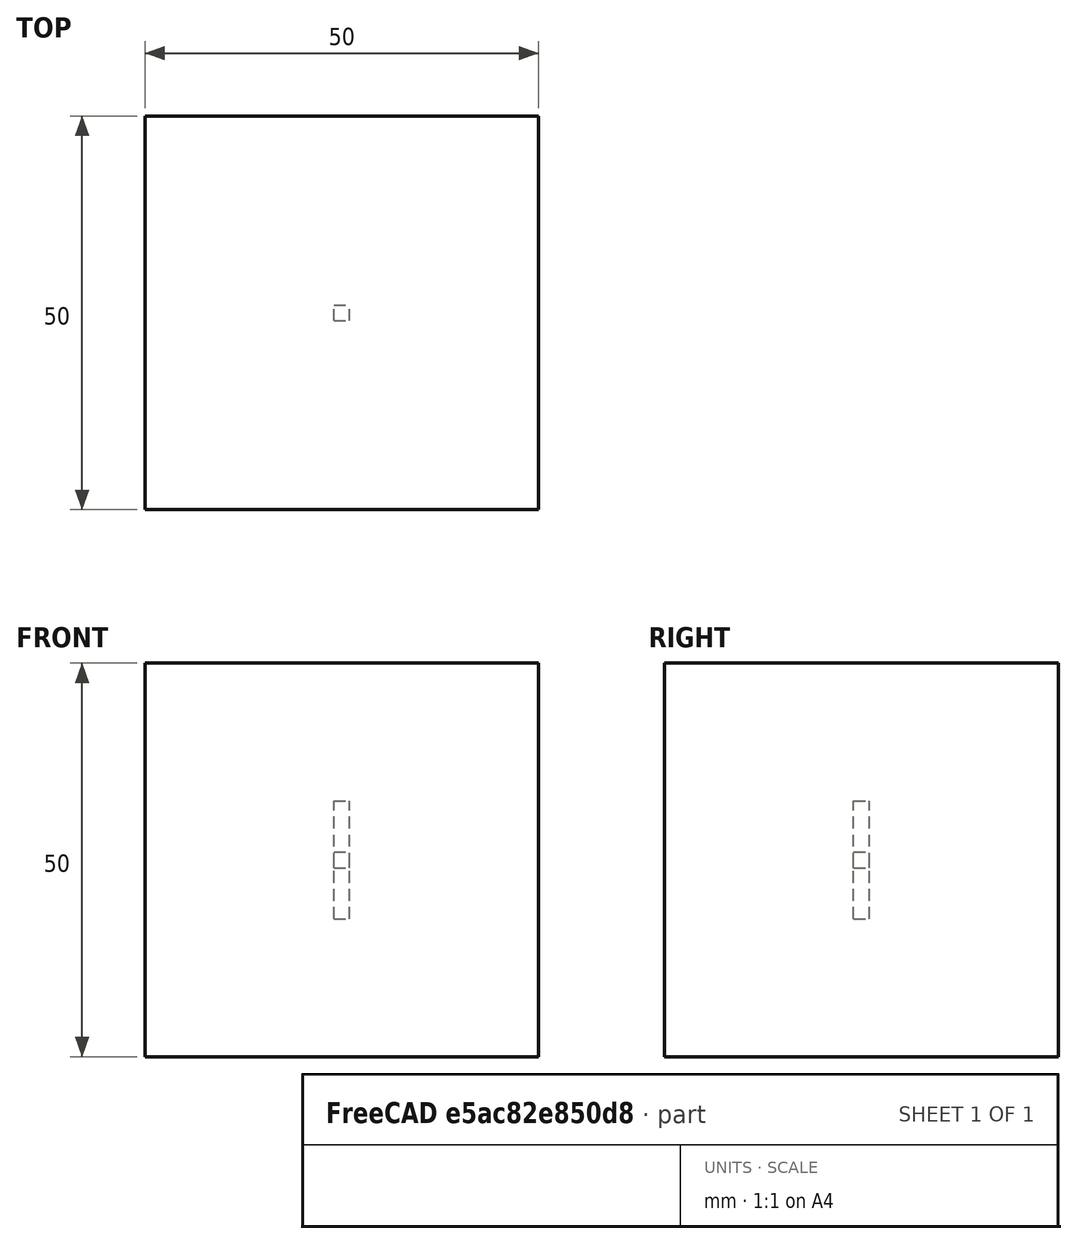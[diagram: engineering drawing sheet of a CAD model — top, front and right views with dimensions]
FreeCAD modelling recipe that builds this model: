
FCSTD DOCUMENT  (FreeCAD 1.0R39109 (Git))
Label: COG_Expanded_simple_array
License: All rights reserved
LicenseURL: http://en.wikipedia.org/wiki/All_rights_reserved
objects: App::DocumentObjectGroupPython×1269, App::Part×7, Part::FeaturePython×6, App::Link×4, App::FeaturePython×2
note: 5 computed .brp shape members not serialized (recipe doc carries the construction recipe); baked Part::Feature solids carry a one-line shape summary decoded from their .brp

FEATURE [App::DocumentObjectGroupPython] Constants  # scripted group (container) (typed FeaturePython)
FEATURE [App::DocumentObjectGroupPython] Variables  # scripted group (container) (typed FeaturePython)
FEATURE [App::DocumentObjectGroupPython] Quantities  # scripted group (container) (typed FeaturePython)
FEATURE [App::DocumentObjectGroupPython] Isotopes  # scripted group (container) (typed FeaturePython)
FEATURE [App::DocumentObjectGroupPython] Elements  # scripted group (container) (typed FeaturePython)
FEATURE [App::DocumentObjectGroupPython] G4_CESIUM_IODIDE  label="G4_CESIUM_IODIDE : 1.000"  # scripted group (container) (typed FeaturePython)
  n = 1
FEATURE [App::DocumentObjectGroupPython] LYSO  # scripted group (container) (typed FeaturePython)
  ABSLENGTH = ABSLENGTHLAR
  Dunit = g/cm3
  Dvalue = 7.1
  FASTCOMPONENT = SCINTLAR
  Group = -> [G4_CESIUM_IODIDE]
  RAYLEIGH = RAYLEIGHLAR
  REEMISSIONPROB = SCINTLAR
  RESOLUTIONSCALE = RS
  RINDEX = RINDEXLAR
  SCINTILLATIONCOMPONENT1 = SCINTLAR
  SCINTILLATIONCOMPONENT2 = SCINTLAR
  SCINTILLATIONTIMECONSTANT1 = FTC
  SCINTILLATIONTIMECONSTANT2 = STC
  SCINTILLATIONYIELD = SY
  SCINTILLATIONYIELD1 = RY1
  SCINTILLATIONYIELD2 = RY2
  SLOWCOMPONENT = SCINTLAR
  YIELDRATIO = YR
  conduct = 2
  density = 1
  expand = 3
  name = LYSO
  specific = 4
FEATURE [App::DocumentObjectGroupPython] G4_AIR  label="G4_AIR : 1.000"  # scripted group (container) (typed FeaturePython)
  n = 1
FEATURE [App::DocumentObjectGroupPython] Air  # scripted group (container) (typed FeaturePython)
  Dunit = mg/cm3
  Dvalue = 1.29
  Group = -> [G4_AIR]
  RINDEX = AirRINDEX
  conduct = 2
  density = 1
  expand = 3
  name = Air
  specific = 4
FEATURE [App::DocumentObjectGroupPython] G4_SILICON_DIOXIDE  label="G4_SILICON_DIOXIDE : 1.000"  # scripted group (container) (typed FeaturePython)
  n = 1
FEATURE [App::DocumentObjectGroupPython] Glass  # scripted group (container) (typed FeaturePython)
  Dunit = g/cm3
  Dvalue = 2.32
  Group = -> [G4_SILICON_DIOXIDE]
  RINDEX = RINDEXLAR
  conduct = 2
  density = 1
  expand = 3
  name = Glass
  specific = 4
FEATURE [App::DocumentObjectGroupPython] SY  # scripted group (container) (typed FeaturePython)
  coldim = 1
  values = 100000
FEATURE [App::DocumentObjectGroupPython] RS  # scripted group (container) (typed FeaturePython)
  coldim = 1
  values = 1
FEATURE [App::DocumentObjectGroupPython] FTC  # scripted group (container) (typed FeaturePython)
  coldim = 1
  values = 21.5*ns
FEATURE [App::DocumentObjectGroupPython] STC  # scripted group (container) (typed FeaturePython)
  coldim = 1
  values = 43.8*ns
FEATURE [App::DocumentObjectGroupPython] RY1  # scripted group (container) (typed FeaturePython)
  coldim = 1
  values = 95
FEATURE [App::DocumentObjectGroupPython] RY2  # scripted group (container) (typed FeaturePython)
  coldim = 1
  values = 5
FEATURE [App::DocumentObjectGroupPython] YR  # scripted group (container) (typed FeaturePython)
  coldim = 1
  values = 0.8
FEATURE [App::DocumentObjectGroupPython] SCINTLAR  # scripted group (container) (typed FeaturePython)
  coldim = 2
  values = <blob: 2358 chars omitted>
FEATURE [App::DocumentObjectGroupPython] RINDEXLAR  # scripted group (container) (typed FeaturePython)
  coldim = 2
  values = <blob: 9384 chars omitted>
FEATURE [App::DocumentObjectGroupPython] ABSLENGTHLAR  # scripted group (container) (typed FeaturePython)
  coldim = 2
  values = 7.74901*eV 10.0*m 7.77525*eV 10.0*m 7.80167*eV 10.0*m 7.82827*eV 10.0*m 7.85506*eV 10.0*m 7.88202*eV 10.0*m 7.90917*eV 10.0*m 7.93651*eV 10.0*m 7.96404*eV 10.0*m 7.99176*eV 10.0*m 8.01968*eV 10.0*m 8.04779*eV 10.0*m 8.07609*eV 10.0*m 8.1046*eV 10.0*m 8.13331*eV 10.0*m 8.16222*eV 10.0*m 8.19134*eV 10.0*m 8.22067*eV 10.0*m 8.25021*eV 10.0*m 8.27996*eV 10.0*m 8.30993*eV 10.0*m 8.34012*eV 10.0*m 8.37052*eV 10.0*m 8.40115*eV 10.0*m 8.432*eV 10.0*m 8.46308*eV 10.0*m 8.4944*eV 10.0*m 8.52594*eV 10.0*m 8.55772*eV 10.0*m 8.58973*eV 10.0*m 8.62199*eV 10.0*m 8.65449*eV 10.0*m 8.68723*eV 10.0*m 8.72023*eV 10.0*m 8.75347*eV 10.0*m 8.78697*eV 10.0*m 8.82073*eV 10.0*m 8.85475*eV 10.0*m 8.88903*eV 10.0*m 8.92358*eV 10.0*m 8.9584*eV 10.0*m 8.99349*eV 10.0*m 9.02885*eV 10.0*m 9.0645*eV 10.0*m 9.10043*eV 10.0*m 9.13664*eV 10.0*m 9.17314*eV 10.0*m 9.20994*eV 10.0*m 9.24703*eV 10.0*m 9.28442*eV 10.0*m 9.32212*eV 10.0*m 9.36012*eV 10.0*m 9.39844*eV 10.0*m 9.43707*eV 10.0*m 9.47602*eV 10.0*m 9.51529*eV 10.0*m 9.55489*eV 10.0*m 9.59481*eV 10.0*m 9.63508*eV 10.0*m 9.67568*eV 10.0*m 9.71663*eV 10.0*m 9.75792*eV 10.0*m 9.79957*eV 10.0*m 9.84158*eV 10.0*m 9.88394*eV 10.0*m 9.92668*eV 10.0*m 9.96978*eV 10.0*m 10.0133*eV 10.0*m 10.0571*eV 10.0*m 10.1014*eV 10.0*m 10.146*eV 10.0*m 10.191*eV 10.0*m 10.2365*eV 10.0*m 10.2823*eV 10.0*m 10.3286*eV 10.0*m 10.3752*eV 10.0*m 10.4223*eV 10.0*m 10.4699*eV 10.0*m 10.5178*eV 10.0*m 10.5662*eV 10.0*m 10.6151*eV 10.0*m 10.6644*eV 10.0*m 10.7142*eV 10.0*m 10.7644*eV 10.0*m 10.8151*eV 10.0*m 10.8663*eV 10.0*m 10.9179*eV 10.0*m 10.9701*eV 10.0*m 11.0228*eV 10.0*m 11.076*eV 10.0*m 11.1296*eV 10.0*m 11.1839*eV 10.0*m 11.2386*eV 10.0*m 11.2939*eV 10.0*m 11.3497*eV 10.0*m 11.4061*eV 10.0*m 11.463*eV 10.0*m 11.5206*eV 10.0*m 11.5787*eV 10.0*m 11.6373*eV 10.0*m
FEATURE [App::DocumentObjectGroupPython] RAYLEIGHLAR  # scripted group (container) (typed FeaturePython)
  coldim = 2
  values = 7.74901*eV 90.0*cm 7.77525*eV 90.0*cm 7.80167*eV 90.0*cm 7.82827*eV 90.0*cm 7.85506*eV 90.0*cm 7.88202*eV 90.0*cm 7.90917*eV 90.0*cm 7.93651*eV 90.0*cm 7.96404*eV 90.0*cm 7.99176*eV 90.0*cm 8.01968*eV 90.0*cm 8.04779*eV 90.0*cm 8.07609*eV 90.0*cm 8.1046*eV 90.0*cm 8.13331*eV 90.0*cm 8.16222*eV 90.0*cm 8.19134*eV 90.0*cm 8.22067*eV 90.0*cm 8.25021*eV 90.0*cm 8.27996*eV 90.0*cm 8.30993*eV 90.0*cm 8.34012*eV 90.0*cm 8.37052*eV 90.0*cm 8.40115*eV 90.0*cm 8.432*eV 90.0*cm 8.46308*eV 90.0*cm 8.4944*eV 90.0*cm 8.52594*eV 90.0*cm 8.55772*eV 90.0*cm 8.58973*eV 90.0*cm 8.62199*eV 90.0*cm 8.65449*eV 90.0*cm 8.68723*eV 90.0*cm 8.72023*eV 90.0*cm 8.75347*eV 90.0*cm 8.78697*eV 90.0*cm 8.82073*eV 90.0*cm 8.85475*eV 90.0*cm 8.88903*eV 90.0*cm 8.92358*eV 90.0*cm 8.9584*eV 90.0*cm 8.99349*eV 90.0*cm 9.02885*eV 90.0*cm 9.0645*eV 90.0*cm 9.10043*eV 90.0*cm 9.13664*eV 90.0*cm 9.17314*eV 90.0*cm 9.20994*eV 90.0*cm 9.24703*eV 90.0*cm 9.28442*eV 90.0*cm 9.32212*eV 90.0*cm 9.36012*eV 90.0*cm 9.39844*eV 90.0*cm 9.43707*eV 90.0*cm 9.47602*eV 90.0*cm 9.51529*eV 90.0*cm 9.55489*eV 90.0*cm 9.59481*eV 90.0*cm 9.63508*eV 90.0*cm 9.67568*eV 90.0*cm 9.71663*eV 90.0*cm 9.75792*eV 90.0*cm 9.79957*eV 90.0*cm 9.84158*eV 90.0*cm 9.88394*eV 90.0*cm 9.92668*eV 90.0*cm 9.96978*eV 90.0*cm 10.0133*eV 90.0*cm 10.0571*eV 90.0*cm 10.1014*eV 90.0*cm 10.146*eV 90.0*cm 10.191*eV 90.0*cm 10.2365*eV 90.0*cm 10.2823*eV 90.0*cm 10.3286*eV 90.0*cm 10.3752*eV 90.0*cm 10.4223*eV 90.0*cm 10.4699*eV 90.0*cm 10.5178*eV 90.0*cm 10.5662*eV 90.0*cm 10.6151*eV 90.0*cm 10.6644*eV 90.0*cm 10.7142*eV 90.0*cm 10.7644*eV 90.0*cm 10.8151*eV 90.0*cm 10.8663*eV 90.0*cm 10.9179*eV 90.0*cm 10.9701*eV 90.0*cm 11.0228*eV 90.0*cm 11.076*eV 90.0*cm 11.1296*eV 90.0*cm 11.1839*eV 90.0*cm 11.2386*eV 90.0*cm 11.2939*eV 90.0*cm 11.3497*eV 90.0*cm 11.4061*eV 90.0*cm 11.463*eV 90.0*cm 11.5206*eV 90.0*cm 11.5787*eV 90.0*cm 11.6373*eV 90.0*cm
FEATURE [App::DocumentObjectGroupPython] REFLECTIVITY  # scripted group (container) (typed FeaturePython)
  coldim = 2
  values = 2.034*eV 0.98 2.068*eV 0.98 2.103*eV 0.98 2.139*eV 0.98 2.177*eV 0.98 2.216*eV 0.98 2.256*eV 0.98 2.298*eV 0.98 2.341*eV 0.98 2.386*eV 0.98 2.433*eV 0.98 2.481*eV 0.98 2.532*eV 0.98 2.585*eV 0.98 2.64*eV 0.98 2.697*eV 0.98 2.757*eV 0.98 2.82*eV 0.98 2.885*eV 0.98 2.954*eV 0.98 3.026*eV 0.98 3.102*eV 0.98 3.181*eV 0.98 3.265*eV 0.98 3.353*eV 0.98 3.446*eV 0.98 3.545*eV 0.98 3.649*eV 0.98 3.76*eV 0.98 3.877*eV 0.98 4.002*eV 0.98 4.136*eV 0.98 5.0*eV 0.98 6.0*eV 0.98 7.0*eV 0.98 8.0*eV 0.98 9.0*eV 0.98 9.0*eV 0.98 10.0*eV 0.98 11.0*eV 0.98 11.6*eV 0.98
FEATURE [App::DocumentObjectGroupPython] EFFICIENCY  # scripted group (container) (typed FeaturePython)
  coldim = 2
  values = 2.034*eV 1 2.068*eV 1 2.103*eV 1 2.139*eV 1 2.177*eV 1 2.216*eV 1 2.256*eV 1 2.298*eV 1 2.341*eV 1 2.386*eV 1 2.433*eV 1 2.481*eV 1 2.532*eV 1 2.585*eV 1 2.64*eV 1 2.697*eV 1 2.757*eV 1 2.82*eV 1 2.885*eV 1 2.954*eV 1 3.026*eV 1 3.102*eV 1 3.181*eV  1 3.265*eV 1 3.353*eV 1 3.446*eV 1 3.545*eV 1 3.649*eV 1 3.76*eV 1 3.877*eV 1 4.002*eV 1 4.136*eV 1 5.0*eV 1 6.0*eV 1 7.0*eV 1 8.0*eV 1 9.0*eV 1 9.0*eV 1 10.0*eV 1 11.0*eV 1 11.6*eV 1
FEATURE [App::DocumentObjectGroupPython] AirRINDEX  # scripted group (container) (typed FeaturePython)
  coldim = 2
  values = 2.034*eV 1 2.068*eV 1 2.103*eV 1 2.139*eV 1 2.177*eV 1 2.216*eV 1 2.256*eV 1 2.298*eV 1 2.341*eV 1 2.386*eV 1 2.433*eV 1 2.481*eV 1 2.532*eV 1 2.585*eV 1 2.64*eV 1 2.697*eV 1 2.757*eV 1 2.82*eV 1 2.885*eV 1 2.954*eV 1 3.026*eV 1 3.102*eV 1 3.181*eV 1 3.265*eV 1 3.353*eV 1 3.446*eV 1 3.545*eV 1 3.649*eV 1 3.76*eV 1 3.877*eV 1 4.002*eV 1 4.136*eV 1 5.0*eV 1 6.0*eV 1 7.0*eV 1 8.0*eV 1 9.0*eV 1 10.0*eV 1 11.0*eV 1 11.6*eV 1
FEATURE [App::DocumentObjectGroupPython] Matrix  # scripted group (container) (typed FeaturePython)
  Group = -> [SY,RS,FTC,STC,RY1,RY2,YR,SCINTLAR,RINDEXLAR,ABSLENGTHLAR,RAYLEIGHLAR,REFLECTIVITY,EFFICIENCY,AirRINDEX]
FEATURE [App::DocumentObjectGroupPython] ScintWrap  # scripted group (container) (typed FeaturePython)
  EFFICIENCY = EFFICIENCY
  REFLECTIVITY = REFLECTIVITY
  finish = 39
  model = 0
  type = 2
  value = 1
FEATURE [App::DocumentObjectGroupPython] Surfaces  # scripted group (container) (typed FeaturePython)
  Group = -> [ScintWrap]
FEATURE [App::DocumentObjectGroupPython] Opticals  # scripted group (container) (typed FeaturePython)
  Group = -> [Matrix,Surfaces]
FEATURE [App::DocumentObjectGroupPython] G4Isotopes  # scripted group (container) (typed FeaturePython)
FEATURE [App::DocumentObjectGroupPython] H_element  # scripted group (container) (typed FeaturePython)
  Z = 1
  atom_value = 1.008
  formula = H
  name = H_element
FEATURE [App::DocumentObjectGroupPython] He_element  # scripted group (container) (typed FeaturePython)
  Z = 2
  atom_value = 4.0026
  formula = He
  name = He_element
FEATURE [App::DocumentObjectGroupPython] Li_element  # scripted group (container) (typed FeaturePython)
  Z = 3
  atom_value = 6.94
  formula = Li
  name = Li_element
FEATURE [App::DocumentObjectGroupPython] Be_element  # scripted group (container) (typed FeaturePython)
  Z = 4
  atom_value = 9.01218
  formula = Be
  name = Be_element
FEATURE [App::DocumentObjectGroupPython] B_element  # scripted group (container) (typed FeaturePython)
  Z = 5
  atom_value = 10.81
  formula = B
  name = B_element
FEATURE [App::DocumentObjectGroupPython] C_element  # scripted group (container) (typed FeaturePython)
  Z = 6
  atom_value = 12.011
  formula = C
  name = C_element
FEATURE [App::DocumentObjectGroupPython] N_element  # scripted group (container) (typed FeaturePython)
  Z = 7
  atom_value = 14.007
  formula = N
  name = N_element
FEATURE [App::DocumentObjectGroupPython] O_element  # scripted group (container) (typed FeaturePython)
  Z = 8
  atom_value = 15.999
  formula = O
  name = O_element
FEATURE [App::DocumentObjectGroupPython] F_element  # scripted group (container) (typed FeaturePython)
  Z = 9
  atom_value = 18.9984
  formula = F
  name = F_element
FEATURE [App::DocumentObjectGroupPython] Ne_element  # scripted group (container) (typed FeaturePython)
  Z = 10
  atom_value = 20.1797
  formula = Ne
  name = Ne_element
FEATURE [App::DocumentObjectGroupPython] Na_element  # scripted group (container) (typed FeaturePython)
  Z = 11
  atom_value = 22.9898
  formula = Na
  name = Na_element
FEATURE [App::DocumentObjectGroupPython] Mg_element  # scripted group (container) (typed FeaturePython)
  Z = 12
  atom_value = 24.305
  formula = Mg
  name = Mg_element
FEATURE [App::DocumentObjectGroupPython] Al_element  # scripted group (container) (typed FeaturePython)
  Z = 13
  atom_value = 26.9815
  formula = Al
  name = Al_element
FEATURE [App::DocumentObjectGroupPython] Si_element  # scripted group (container) (typed FeaturePython)
  Z = 14
  atom_value = 28.085
  formula = Si
  name = Si_element
FEATURE [App::DocumentObjectGroupPython] P_element  # scripted group (container) (typed FeaturePython)
  Z = 15
  atom_value = 30.9738
  formula = P
  name = P_element
FEATURE [App::DocumentObjectGroupPython] S_element  # scripted group (container) (typed FeaturePython)
  Z = 16
  atom_value = 32.06
  formula = S
  name = S_element
FEATURE [App::DocumentObjectGroupPython] Cl_element  # scripted group (container) (typed FeaturePython)
  Z = 17
  atom_value = 35.45
  formula = Cl
  name = Cl_element
FEATURE [App::DocumentObjectGroupPython] Ar_element  # scripted group (container) (typed FeaturePython)
  Z = 18
  atom_value = 39.95
  formula = Ar
  name = Ar_element
FEATURE [App::DocumentObjectGroupPython] K_element  # scripted group (container) (typed FeaturePython)
  Z = 19
  atom_value = 39.0983
  formula = K
  name = K_element
FEATURE [App::DocumentObjectGroupPython] Ca_element  # scripted group (container) (typed FeaturePython)
  Z = 20
  atom_value = 40.078
  formula = Ca
  name = Ca_element
FEATURE [App::DocumentObjectGroupPython] Sc_element  # scripted group (container) (typed FeaturePython)
  Z = 21
  atom_value = 44.9559
  formula = Sc
  name = Sc_element
FEATURE [App::DocumentObjectGroupPython] Ti_element  # scripted group (container) (typed FeaturePython)
  Z = 22
  atom_value = 47.867
  formula = Ti
  name = Ti_element
FEATURE [App::DocumentObjectGroupPython] V_element  # scripted group (container) (typed FeaturePython)
  Z = 23
  atom_value = 50.9415
  formula = V
  name = V_element
FEATURE [App::DocumentObjectGroupPython] Cr_element  # scripted group (container) (typed FeaturePython)
  Z = 24
  atom_value = 51.9961
  formula = Cr
  name = Cr_element
FEATURE [App::DocumentObjectGroupPython] Mn_element  # scripted group (container) (typed FeaturePython)
  Z = 25
  atom_value = 54.938
  formula = Mn
  name = Mn_element
FEATURE [App::DocumentObjectGroupPython] Fe_element  # scripted group (container) (typed FeaturePython)
  Z = 26
  atom_value = 55.845
  formula = Fe
  name = Fe_element
FEATURE [App::DocumentObjectGroupPython] Co_element  # scripted group (container) (typed FeaturePython)
  Z = 27
  atom_value = 58.9332
  formula = Co
  name = Co_element
FEATURE [App::DocumentObjectGroupPython] Ni_element  # scripted group (container) (typed FeaturePython)
  Z = 28
  atom_value = 58.6934
  formula = Ni
  name = Ni_element
FEATURE [App::DocumentObjectGroupPython] Cu_element  # scripted group (container) (typed FeaturePython)
  Z = 29
  atom_value = 63.546
  formula = Cu
  name = Cu_element
FEATURE [App::DocumentObjectGroupPython] Zn_element  # scripted group (container) (typed FeaturePython)
  Z = 30
  atom_value = 65.38
  formula = Zn
  name = Zn_element
FEATURE [App::DocumentObjectGroupPython] Ga_element  # scripted group (container) (typed FeaturePython)
  Z = 31
  atom_value = 69.723
  formula = Ga
  name = Ga_element
FEATURE [App::DocumentObjectGroupPython] Ge_element  # scripted group (container) (typed FeaturePython)
  Z = 32
  atom_value = 72.63
  formula = Ge
  name = Ge_element
FEATURE [App::DocumentObjectGroupPython] As_element  # scripted group (container) (typed FeaturePython)
  Z = 33
  atom_value = 74.9216
  formula = As
  name = As_element
FEATURE [App::DocumentObjectGroupPython] Se_element  # scripted group (container) (typed FeaturePython)
  Z = 34
  atom_value = 78.971
  formula = Se
  name = Se_element
FEATURE [App::DocumentObjectGroupPython] Br_element  # scripted group (container) (typed FeaturePython)
  Z = 35
  atom_value = 79.904
  formula = Br
  name = Br_element
FEATURE [App::DocumentObjectGroupPython] Kr_element  # scripted group (container) (typed FeaturePython)
  Z = 36
  atom_value = 83.798
  formula = Kr
  name = Kr_element
FEATURE [App::DocumentObjectGroupPython] Rb_element  # scripted group (container) (typed FeaturePython)
  Z = 37
  atom_value = 85.4678
  formula = Rb
  name = Rb_element
FEATURE [App::DocumentObjectGroupPython] Sr_element  # scripted group (container) (typed FeaturePython)
  Z = 38
  atom_value = 87.62
  formula = Sr
  name = Sr_element
FEATURE [App::DocumentObjectGroupPython] Y_element  # scripted group (container) (typed FeaturePython)
  Z = 39
  atom_value = 88.9058
  formula = Y
  name = Y_element
FEATURE [App::DocumentObjectGroupPython] Zr_element  # scripted group (container) (typed FeaturePython)
  Z = 40
  atom_value = 91.224
  formula = Zr
  name = Zr_element
FEATURE [App::DocumentObjectGroupPython] Nb_element  # scripted group (container) (typed FeaturePython)
  Z = 41
  atom_value = 92.9064
  formula = Nb
  name = Nb_element
FEATURE [App::DocumentObjectGroupPython] Mo_element  # scripted group (container) (typed FeaturePython)
  Z = 42
  atom_value = 95.95
  formula = Mo
  name = Mo_element
FEATURE [App::DocumentObjectGroupPython] Tc_element  # scripted group (container) (typed FeaturePython)
  Z = 43
  atom_value = 97
  formula = Tc
  name = Tc_element
FEATURE [App::DocumentObjectGroupPython] Ru_element  # scripted group (container) (typed FeaturePython)
  Z = 44
  atom_value = 101.07
  formula = Ru
  name = Ru_element
FEATURE [App::DocumentObjectGroupPython] Rh_element  # scripted group (container) (typed FeaturePython)
  Z = 45
  atom_value = 102.905
  formula = Rh
  name = Rh_element
FEATURE [App::DocumentObjectGroupPython] Pd_element  # scripted group (container) (typed FeaturePython)
  Z = 46
  atom_value = 106.42
  formula = Pd
  name = Pd_element
FEATURE [App::DocumentObjectGroupPython] Ag_element  # scripted group (container) (typed FeaturePython)
  Z = 47
  atom_value = 107.868
  formula = Ag
  name = Ag_element
FEATURE [App::DocumentObjectGroupPython] Cd_element  # scripted group (container) (typed FeaturePython)
  Z = 48
  atom_value = 112.414
  formula = Cd
  name = Cd_element
FEATURE [App::DocumentObjectGroupPython] In_element  # scripted group (container) (typed FeaturePython)
  Z = 49
  atom_value = 114.818
  formula = In
  name = In_element
FEATURE [App::DocumentObjectGroupPython] Sn_element  # scripted group (container) (typed FeaturePython)
  Z = 50
  atom_value = 118.71
  formula = Sn
  name = Sn_element
FEATURE [App::DocumentObjectGroupPython] Sb_element  # scripted group (container) (typed FeaturePython)
  Z = 51
  atom_value = 121.76
  formula = Sb
  name = Sb_element
FEATURE [App::DocumentObjectGroupPython] Te_element  # scripted group (container) (typed FeaturePython)
  Z = 52
  atom_value = 127.6
  formula = Te
  name = Te_element
FEATURE [App::DocumentObjectGroupPython] I_element  # scripted group (container) (typed FeaturePython)
  Z = 53
  atom_value = 126.904
  formula = I
  name = I_element
FEATURE [App::DocumentObjectGroupPython] Xe_element  # scripted group (container) (typed FeaturePython)
  Z = 54
  atom_value = 131.293
  formula = Xe
  name = Xe_element
FEATURE [App::DocumentObjectGroupPython] Cs_element  # scripted group (container) (typed FeaturePython)
  Z = 55
  atom_value = 132.905
  formula = Cs
  name = Cs_element
FEATURE [App::DocumentObjectGroupPython] Ba_element  # scripted group (container) (typed FeaturePython)
  Z = 56
  atom_value = 137.327
  formula = Ba
  name = Ba_element
FEATURE [App::DocumentObjectGroupPython] La_element  # scripted group (container) (typed FeaturePython)
  Z = 57
  atom_value = 138.905
  formula = La
  name = La_element
FEATURE [App::DocumentObjectGroupPython] Ce_element  # scripted group (container) (typed FeaturePython)
  Z = 58
  atom_value = 140.116
  formula = Ce
  name = Ce_element
FEATURE [App::DocumentObjectGroupPython] Pr_element  # scripted group (container) (typed FeaturePython)
  Z = 59
  atom_value = 140.908
  formula = Pr
  name = Pr_element
FEATURE [App::DocumentObjectGroupPython] Nd_element  # scripted group (container) (typed FeaturePython)
  Z = 60
  atom_value = 144.242
  formula = Nd
  name = Nd_element
FEATURE [App::DocumentObjectGroupPython] Pm_element  # scripted group (container) (typed FeaturePython)
  Z = 61
  atom_value = 145
  formula = Pm
  name = Pm_element
FEATURE [App::DocumentObjectGroupPython] Sm_element  # scripted group (container) (typed FeaturePython)
  Z = 62
  atom_value = 150.36
  formula = Sm
  name = Sm_element
FEATURE [App::DocumentObjectGroupPython] Eu_element  # scripted group (container) (typed FeaturePython)
  Z = 63
  atom_value = 151.964
  formula = Eu
  name = Eu_element
FEATURE [App::DocumentObjectGroupPython] Gd_element  # scripted group (container) (typed FeaturePython)
  Z = 64
  atom_value = 157.25
  formula = Gd
  name = Gd_element
FEATURE [App::DocumentObjectGroupPython] Tb_element  # scripted group (container) (typed FeaturePython)
  Z = 65
  atom_value = 158.925
  formula = Tb
  name = Tb_element
FEATURE [App::DocumentObjectGroupPython] Dy_element  # scripted group (container) (typed FeaturePython)
  Z = 66
  atom_value = 162.5
  formula = Dy
  name = Dy_element
FEATURE [App::DocumentObjectGroupPython] Ho_element  # scripted group (container) (typed FeaturePython)
  Z = 67
  atom_value = 164.93
  formula = Ho
  name = Ho_element
FEATURE [App::DocumentObjectGroupPython] Er_element  # scripted group (container) (typed FeaturePython)
  Z = 68
  atom_value = 167.259
  formula = Er
  name = Er_element
FEATURE [App::DocumentObjectGroupPython] Tm_element  # scripted group (container) (typed FeaturePython)
  Z = 69
  atom_value = 168.934
  formula = Tm
  name = Tm_element
FEATURE [App::DocumentObjectGroupPython] Yb_element  # scripted group (container) (typed FeaturePython)
  Z = 70
  atom_value = 173.045
  formula = Yb
  name = Yb_element
FEATURE [App::DocumentObjectGroupPython] Lu_element  # scripted group (container) (typed FeaturePython)
  Z = 71
  atom_value = 174.967
  formula = Lu
  name = Lu_element
FEATURE [App::DocumentObjectGroupPython] Hf_element  # scripted group (container) (typed FeaturePython)
  Z = 72
  atom_value = 178.49
  formula = Hf
  name = Hf_element
FEATURE [App::DocumentObjectGroupPython] Ta_element  # scripted group (container) (typed FeaturePython)
  Z = 73
  atom_value = 180.948
  formula = Ta
  name = Ta_element
FEATURE [App::DocumentObjectGroupPython] W_element  # scripted group (container) (typed FeaturePython)
  Z = 74
  atom_value = 183.84
  formula = W
  name = W_element
FEATURE [App::DocumentObjectGroupPython] Re_element  # scripted group (container) (typed FeaturePython)
  Z = 75
  atom_value = 186.207
  formula = Re
  name = Re_element
FEATURE [App::DocumentObjectGroupPython] Os_element  # scripted group (container) (typed FeaturePython)
  Z = 76
  atom_value = 190.23
  formula = Os
  name = Os_element
FEATURE [App::DocumentObjectGroupPython] Ir_element  # scripted group (container) (typed FeaturePython)
  Z = 77
  atom_value = 192.217
  formula = Ir
  name = Ir_element
FEATURE [App::DocumentObjectGroupPython] Pt_element  # scripted group (container) (typed FeaturePython)
  Z = 78
  atom_value = 195.084
  formula = Pt
  name = Pt_element
FEATURE [App::DocumentObjectGroupPython] Au_element  # scripted group (container) (typed FeaturePython)
  Z = 79
  atom_value = 196.967
  formula = Au
  name = Au_element
FEATURE [App::DocumentObjectGroupPython] Hg_element  # scripted group (container) (typed FeaturePython)
  Z = 80
  atom_value = 200.592
  formula = Hg
  name = Hg_element
FEATURE [App::DocumentObjectGroupPython] Tl_element  # scripted group (container) (typed FeaturePython)
  Z = 81
  atom_value = 204.38
  formula = Tl
  name = Tl_element
FEATURE [App::DocumentObjectGroupPython] Pb_element  # scripted group (container) (typed FeaturePython)
  Z = 82
  atom_value = 207.2
  formula = Pb
  name = Pb_element
FEATURE [App::DocumentObjectGroupPython] Bi_element  # scripted group (container) (typed FeaturePython)
  Z = 83
  atom_value = 208.98
  formula = Bi
  name = Bi_element
FEATURE [App::DocumentObjectGroupPython] Po_element  # scripted group (container) (typed FeaturePython)
  Z = 84
  atom_value = 209
  formula = Po
  name = Po_element
FEATURE [App::DocumentObjectGroupPython] At_element  # scripted group (container) (typed FeaturePython)
  Z = 85
  atom_value = 210
  formula = At
  name = At_element
FEATURE [App::DocumentObjectGroupPython] Rn_element  # scripted group (container) (typed FeaturePython)
  Z = 86
  atom_value = 222
  formula = Rn
  name = Rn_element
FEATURE [App::DocumentObjectGroupPython] Fr_element  # scripted group (container) (typed FeaturePython)
  Z = 87
  atom_value = 223
  formula = Fr
  name = Fr_element
FEATURE [App::DocumentObjectGroupPython] Ra_element  # scripted group (container) (typed FeaturePython)
  Z = 88
  atom_value = 226
  formula = Ra
  name = Ra_element
FEATURE [App::DocumentObjectGroupPython] Ac_element  # scripted group (container) (typed FeaturePython)
  Z = 89
  atom_value = 227
  formula = Ac
  name = Ac_element
FEATURE [App::DocumentObjectGroupPython] Th_element  # scripted group (container) (typed FeaturePython)
  Z = 90
  atom_value = 232.038
  formula = Th
  name = Th_element
FEATURE [App::DocumentObjectGroupPython] Pa_element  # scripted group (container) (typed FeaturePython)
  Z = 91
  atom_value = 231.036
  formula = Pa
  name = Pa_element
FEATURE [App::DocumentObjectGroupPython] U_element  # scripted group (container) (typed FeaturePython)
  Z = 92
  atom_value = 238.029
  formula = U
  name = U_element
FEATURE [App::DocumentObjectGroupPython] Np_element  # scripted group (container) (typed FeaturePython)
  Z = 93
  atom_value = 237
  formula = Np
  name = Np_element
FEATURE [App::DocumentObjectGroupPython] Pu_element  # scripted group (container) (typed FeaturePython)
  Z = 94
  atom_value = 244
  formula = Pu
  name = Pu_element
FEATURE [App::DocumentObjectGroupPython] Am_element  # scripted group (container) (typed FeaturePython)
  Z = 95
  atom_value = 243
  formula = Am
  name = Am_element
FEATURE [App::DocumentObjectGroupPython] Cm_element  # scripted group (container) (typed FeaturePython)
  Z = 96
  atom_value = 247
  formula = Cm
  name = Cm_element
FEATURE [App::DocumentObjectGroupPython] Bk_element  # scripted group (container) (typed FeaturePython)
  Z = 97
  atom_value = 247
  formula = Bk
  name = Bk_element
FEATURE [App::DocumentObjectGroupPython] Cf_element  # scripted group (container) (typed FeaturePython)
  Z = 98
  atom_value = 251
  formula = Cf
  name = Cf_element
FEATURE [App::DocumentObjectGroupPython] G4Elements  # scripted group (container) (typed FeaturePython)
  Group = -> [H_element,He_element,Li_element,Be_element,B_element,C_element,N_element,O_element,F_element,Ne_element,Na_element,Mg_element,Al_element,Si_element,P_element,S_element,Cl_element,Ar_element,K_element,Ca_element,Sc_element,Ti_element,V_element,Cr_element,Mn_element,Fe_element,Co_element,Ni_element,Cu_element,Zn_element,Ga_element,Ge_element,As_element,Se_element,Br_element,Kr_element,Rb_element,+61 more]
FEATURE [App::DocumentObjectGroupPython] H_element001  label="H_element : 0.101"  # scripted group (container) (typed FeaturePython)
  n = 0.101327
FEATURE [App::DocumentObjectGroupPython] C_element001  label="C_element : 0.775"  # scripted group (container) (typed FeaturePython)
  n = 0.7755
FEATURE [App::DocumentObjectGroupPython] N_element001  label="N_element : 0.035"  # scripted group (container) (typed FeaturePython)
  n = 0.035057
FEATURE [App::DocumentObjectGroupPython] O_element001  label="O_element : 0.052"  # scripted group (container) (typed FeaturePython)
  n = 0.0523159
FEATURE [App::DocumentObjectGroupPython] F_element001  label="F_element : 0.017"  # scripted group (container) (typed FeaturePython)
  n = 0.017422
FEATURE [App::DocumentObjectGroupPython] Ca_element001  label="Ca_element : 0.018"  # scripted group (container) (typed FeaturePython)
  n = 0.018378
FEATURE [App::DocumentObjectGroupPython] G4_A_150_TISSUE  label="G4_A-150_TISSUE"  # scripted group (container) (typed FeaturePython)
  Dunit = g/cm3
  Dvalue = 1.127
  Group = -> [H_element001,C_element001,N_element001,O_element001,F_element001,Ca_element001]
  conduct = 2
  density = 1
  expand = 3
  formula = G4_A-150_TISSUE
  name = G4_A-150_TISSUE
  specific = 4
FEATURE [App::DocumentObjectGroupPython] C_element002  label="C_element : 3"  # scripted group (container) (typed FeaturePython)
  n = 3
  ref = C_element
FEATURE [App::DocumentObjectGroupPython] H_element002  label="H_element : 6"  # scripted group (container) (typed FeaturePython)
  n = 6
  ref = H_element
FEATURE [App::DocumentObjectGroupPython] O_element002  label="O_element : 1"  # scripted group (container) (typed FeaturePython)
  n = 1
  ref = O_element
FEATURE [App::DocumentObjectGroupPython] G4_ACETONE  # scripted group (container) (typed FeaturePython)
  Dunit = g/cm3
  Dvalue = 0.7899
  Group = -> [C_element002,H_element002,O_element002]
  conduct = 2
  density = 1
  expand = 3
  formula = G4_ACETONE
  name = G4_ACETONE
  specific = 4
FEATURE [App::DocumentObjectGroupPython] C_element003  label="C_element : 2"  # scripted group (container) (typed FeaturePython)
  n = 2
  ref = C_element
FEATURE [App::DocumentObjectGroupPython] H_element003  label="H_element : 2"  # scripted group (container) (typed FeaturePython)
  n = 2
  ref = H_element
FEATURE [App::DocumentObjectGroupPython] G4_ACETYLENE  # scripted group (container) (typed FeaturePython)
  Dunit = g/cm3
  Dvalue = 0.0010967
  Group = -> [C_element003,H_element003]
  conduct = 2
  density = 1
  expand = 3
  formula = G4_ACETYLENE
  name = G4_ACETYLENE
  specific = 4
FEATURE [App::DocumentObjectGroupPython] C_element004  label="C_element : 5"  # scripted group (container) (typed FeaturePython)
  n = 5
  ref = C_element
FEATURE [App::DocumentObjectGroupPython] H_element004  label="H_element : 5"  # scripted group (container) (typed FeaturePython)
  n = 5
  ref = H_element
FEATURE [App::DocumentObjectGroupPython] N_element002  label="N_element : 5"  # scripted group (container) (typed FeaturePython)
  n = 5
  ref = N_element
FEATURE [App::DocumentObjectGroupPython] G4_ADENINE  # scripted group (container) (typed FeaturePython)
  Dunit = g/cm3
  Dvalue = 1.6
  Group = -> [C_element004,H_element004,N_element002]
  conduct = 2
  density = 1
  expand = 3
  formula = G4_ADENINE
  name = G4_ADENINE
  specific = 4
FEATURE [App::DocumentObjectGroupPython] H_element005  label="H_element : 0.114"  # scripted group (container) (typed FeaturePython)
  n = 0.114
FEATURE [App::DocumentObjectGroupPython] C_element005  label="C_element : 0.598"  # scripted group (container) (typed FeaturePython)
  n = 0.598
FEATURE [App::DocumentObjectGroupPython] N_element003  label="N_element : 0.007"  # scripted group (container) (typed FeaturePython)
  n = 0.007
FEATURE [App::DocumentObjectGroupPython] O_element003  label="O_element : 0.278"  # scripted group (container) (typed FeaturePython)
  n = 0.278
FEATURE [App::DocumentObjectGroupPython] Na_element001  label="Na_element : 0.001"  # scripted group (container) (typed FeaturePython)
  n = 0.001
FEATURE [App::DocumentObjectGroupPython] S_element001  label="S_element : 0.001"  # scripted group (container) (typed FeaturePython)
  n = 0.001
FEATURE [App::DocumentObjectGroupPython] Cl_element001  label="Cl_element : 0.001"  # scripted group (container) (typed FeaturePython)
  n = 0.001
FEATURE [App::DocumentObjectGroupPython] G4_ADIPOSE_TISSUE_ICRP  # scripted group (container) (typed FeaturePython)
  Dunit = g/cm3
  Dvalue = 0.95
  Group = -> [H_element005,C_element005,N_element003,O_element003,Na_element001,S_element001,Cl_element001]
  conduct = 2
  density = 1
  expand = 3
  formula = G4_ADIPOSE_TISSUE_ICRP
  name = G4_ADIPOSE_TISSUE_ICRP
  specific = 4
FEATURE [App::DocumentObjectGroupPython] C_element006  label="C_element : 0.000"  # scripted group (container) (typed FeaturePython)
  n = 0.000124
FEATURE [App::DocumentObjectGroupPython] N_element004  label="N_element : 0.755"  # scripted group (container) (typed FeaturePython)
  n = 0.755268
FEATURE [App::DocumentObjectGroupPython] O_element004  label="O_element : 0.232"  # scripted group (container) (typed FeaturePython)
  n = 0.231781
FEATURE [App::DocumentObjectGroupPython] Ar_element001  label="Ar_element : 0.013"  # scripted group (container) (typed FeaturePython)
  n = 0.012827
FEATURE [App::DocumentObjectGroupPython] G4_AIR001  label="G4_AIR"  # scripted group (container) (typed FeaturePython)
  Dunit = g/cm3
  Dvalue = 0.00120479
  Group = -> [C_element006,N_element004,O_element004,Ar_element001]
  conduct = 2
  density = 1
  expand = 3
  formula = G4_AIR
  name = G4_AIR
  specific = 4
FEATURE [App::DocumentObjectGroupPython] C_element007  label="C_element : 006"  # scripted group (container) (typed FeaturePython)
  n = 3
  ref = C_element
FEATURE [App::DocumentObjectGroupPython] H_element006  label="H_element : 7"  # scripted group (container) (typed FeaturePython)
  n = 7
  ref = H_element
FEATURE [App::DocumentObjectGroupPython] N_element005  label="N_element : 1"  # scripted group (container) (typed FeaturePython)
  n = 1
  ref = N_element
FEATURE [App::DocumentObjectGroupPython] O_element005  label="O_element : 2"  # scripted group (container) (typed FeaturePython)
  n = 2
  ref = O_element
FEATURE [App::DocumentObjectGroupPython] G4_ALANINE  # scripted group (container) (typed FeaturePython)
  Dunit = g/cm3
  Dvalue = 1.42
  Group = -> [C_element007,H_element006,N_element005,O_element005]
  conduct = 2
  density = 1
  expand = 3
  formula = G4_ALANINE
  name = G4_ALANINE
  specific = 4
FEATURE [App::DocumentObjectGroupPython] Al_element001  label="Al_element : 2"  # scripted group (container) (typed FeaturePython)
  n = 2
  ref = Al_element
FEATURE [App::DocumentObjectGroupPython] O_element006  label="O_element : 3"  # scripted group (container) (typed FeaturePython)
  n = 3
  ref = O_element
FEATURE [App::DocumentObjectGroupPython] G4_ALUMINUM_OXIDE  # scripted group (container) (typed FeaturePython)
  Dunit = g/cm3
  Dvalue = 3.97
  Group = -> [Al_element001,O_element006]
  conduct = 2
  density = 1
  expand = 3
  formula = G4_ALUMINUM_OXIDE
  name = G4_ALUMINUM_OXIDE
  specific = 4
FEATURE [App::DocumentObjectGroupPython] H_element007  label="H_element : 0.106"  # scripted group (container) (typed FeaturePython)
  n = 0.10593
FEATURE [App::DocumentObjectGroupPython] C_element008  label="C_element : 0.789"  # scripted group (container) (typed FeaturePython)
  n = 0.788974
FEATURE [App::DocumentObjectGroupPython] O_element007  label="O_element : 0.105"  # scripted group (container) (typed FeaturePython)
  n = 0.105096
FEATURE [App::DocumentObjectGroupPython] G4_AMBER  # scripted group (container) (typed FeaturePython)
  Dunit = g/cm3
  Dvalue = 1.1
  Group = -> [H_element007,C_element008,O_element007]
  conduct = 2
  density = 1
  expand = 3
  formula = G4_AMBER
  name = G4_AMBER
  specific = 4
FEATURE [App::DocumentObjectGroupPython] N_element006  label="N_element : 006"  # scripted group (container) (typed FeaturePython)
  n = 1
  ref = N_element
FEATURE [App::DocumentObjectGroupPython] H_element008  label="H_element : 3"  # scripted group (container) (typed FeaturePython)
  n = 3
  ref = H_element
FEATURE [App::DocumentObjectGroupPython] G4_AMMONIA  # scripted group (container) (typed FeaturePython)
  Dunit = g/cm3
  Dvalue = 0.000826019
  Group = -> [N_element006,H_element008]
  conduct = 2
  density = 1
  expand = 3
  formula = G4_AMMONIA
  name = G4_AMMONIA
  specific = 4
FEATURE [App::DocumentObjectGroupPython] C_element009  label="C_element : 6"  # scripted group (container) (typed FeaturePython)
  n = 6
  ref = C_element
FEATURE [App::DocumentObjectGroupPython] H_element009  label="H_element : 008"  # scripted group (container) (typed FeaturePython)
  n = 7
  ref = H_element
FEATURE [App::DocumentObjectGroupPython] N_element007  label="N_element : 007"  # scripted group (container) (typed FeaturePython)
  n = 1
  ref = N_element
FEATURE [App::DocumentObjectGroupPython] G4_ANILINE  # scripted group (container) (typed FeaturePython)
  Dunit = g/cm3
  Dvalue = 1.0235
  Group = -> [C_element009,H_element009,N_element007]
  conduct = 2
  density = 1
  expand = 3
  formula = G4_ANILINE
  name = G4_ANILINE
  specific = 4
FEATURE [App::DocumentObjectGroupPython] C_element010  label="C_element : 14"  # scripted group (container) (typed FeaturePython)
  n = 14
  ref = C_element
FEATURE [App::DocumentObjectGroupPython] H_element010  label="H_element : 10"  # scripted group (container) (typed FeaturePython)
  n = 10
  ref = H_element
FEATURE [App::DocumentObjectGroupPython] G4_ANTHRACENE  # scripted group (container) (typed FeaturePython)
  Dunit = g/cm3
  Dvalue = 1.283
  Group = -> [C_element010,H_element010]
  conduct = 2
  density = 1
  expand = 3
  formula = G4_ANTHRACENE
  name = G4_ANTHRACENE
  specific = 4
FEATURE [App::DocumentObjectGroupPython] H_element011  label="H_element : 0.065"  # scripted group (container) (typed FeaturePython)
  n = 0.0654709
FEATURE [App::DocumentObjectGroupPython] C_element011  label="C_element : 0.537"  # scripted group (container) (typed FeaturePython)
  n = 0.536944
FEATURE [App::DocumentObjectGroupPython] N_element008  label="N_element : 0.021"  # scripted group (container) (typed FeaturePython)
  n = 0.0215
FEATURE [App::DocumentObjectGroupPython] O_element008  label="O_element : 0.032"  # scripted group (container) (typed FeaturePython)
  n = 0.032085
FEATURE [App::DocumentObjectGroupPython] F_element002  label="F_element : 0.167"  # scripted group (container) (typed FeaturePython)
  n = 0.167411
FEATURE [App::DocumentObjectGroupPython] Ca_element002  label="Ca_element : 0.177"  # scripted group (container) (typed FeaturePython)
  n = 0.176589
FEATURE [App::DocumentObjectGroupPython] G4_B_100_BONE  label="G4_B-100_BONE"  # scripted group (container) (typed FeaturePython)
  Dunit = g/cm3
  Dvalue = 1.45
  Group = -> [H_element011,C_element011,N_element008,O_element008,F_element002,Ca_element002]
  conduct = 2
  density = 1
  expand = 3
  formula = G4_B-100_BONE
  name = G4_B-100_BONE
  specific = 4
FEATURE [App::DocumentObjectGroupPython] H_element012  label="H_element : 0.057"  # scripted group (container) (typed FeaturePython)
  n = 0.057441
FEATURE [App::DocumentObjectGroupPython] C_element012  label="C_element : 0.790"  # scripted group (container) (typed FeaturePython)
  n = 0.774591
FEATURE [App::DocumentObjectGroupPython] O_element009  label="O_element : 0.168"  # scripted group (container) (typed FeaturePython)
  n = 0.167968
FEATURE [App::DocumentObjectGroupPython] G4_BAKELITE  # scripted group (container) (typed FeaturePython)
  Dunit = g/cm3
  Dvalue = 1.25
  Group = -> [H_element012,C_element012,O_element009]
  conduct = 2
  density = 1
  expand = 3
  formula = G4_BAKELITE
  name = G4_BAKELITE
  specific = 4
FEATURE [App::DocumentObjectGroupPython] Ba_element001  label="Ba_element : 1"  # scripted group (container) (typed FeaturePython)
  n = 1
  ref = Ba_element
FEATURE [App::DocumentObjectGroupPython] F_element003  label="F_element : 2"  # scripted group (container) (typed FeaturePython)
  n = 2
  ref = F_element
FEATURE [App::DocumentObjectGroupPython] G4_BARIUM_FLUORIDE  # scripted group (container) (typed FeaturePython)
  Dunit = g/cm3
  Dvalue = 4.89
  Group = -> [Ba_element001,F_element003]
  conduct = 2
  density = 1
  expand = 3
  formula = G4_BARIUM_FLUORIDE
  name = G4_BARIUM_FLUORIDE
  specific = 4
FEATURE [App::DocumentObjectGroupPython] Ba_element002  label="Ba_element : 002"  # scripted group (container) (typed FeaturePython)
  n = 1
  ref = Ba_element
FEATURE [App::DocumentObjectGroupPython] S_element002  label="S_element : 1"  # scripted group (container) (typed FeaturePython)
  n = 1
  ref = S_element
FEATURE [App::DocumentObjectGroupPython] O_element010  label="O_element : 4"  # scripted group (container) (typed FeaturePython)
  n = 4
  ref = O_element
FEATURE [App::DocumentObjectGroupPython] G4_BARIUM_SULFATE  # scripted group (container) (typed FeaturePython)
  Dunit = g/cm3
  Dvalue = 4.5
  Group = -> [Ba_element002,S_element002,O_element010]
  conduct = 2
  density = 1
  expand = 3
  formula = G4_BARIUM_SULFATE
  name = G4_BARIUM_SULFATE
  specific = 4
FEATURE [App::DocumentObjectGroupPython] C_element013  label="C_element : 007"  # scripted group (container) (typed FeaturePython)
  n = 6
  ref = C_element
FEATURE [App::DocumentObjectGroupPython] H_element013  label="H_element : 009"  # scripted group (container) (typed FeaturePython)
  n = 6
  ref = H_element
FEATURE [App::DocumentObjectGroupPython] G4_BENZENE  # scripted group (container) (typed FeaturePython)
  Dunit = g/cm3
  Dvalue = 0.87865
  Group = -> [C_element013,H_element013]
  conduct = 2
  density = 1
  expand = 3
  formula = G4_BENZENE
  name = G4_BENZENE
  specific = 4
FEATURE [App::DocumentObjectGroupPython] Be_element001  label="Be_element : 1"  # scripted group (container) (typed FeaturePython)
  n = 1
  ref = Be_element
FEATURE [App::DocumentObjectGroupPython] O_element011  label="O_element : 005"  # scripted group (container) (typed FeaturePython)
  n = 1
  ref = O_element
FEATURE [App::DocumentObjectGroupPython] G4_BERYLLIUM_OXIDE  # scripted group (container) (typed FeaturePython)
  Dunit = g/cm3
  Dvalue = 3.01
  Group = -> [Be_element001,O_element011]
  conduct = 2
  density = 1
  expand = 3
  formula = G4_BERYLLIUM_OXIDE
  name = G4_BERYLLIUM_OXIDE
  specific = 4
FEATURE [App::DocumentObjectGroupPython] Bi_element001  label="Bi_element : 4"  # scripted group (container) (typed FeaturePython)
  n = 4
  ref = Bi_element
FEATURE [App::DocumentObjectGroupPython] Ge_element001  label="Ge_element : 3"  # scripted group (container) (typed FeaturePython)
  n = 3
  ref = Ge_element
FEATURE [App::DocumentObjectGroupPython] O_element012  label="O_element : 12"  # scripted group (container) (typed FeaturePython)
  n = 12
  ref = O_element
FEATURE [App::DocumentObjectGroupPython] G4_BGO  # scripted group (container) (typed FeaturePython)
  Dunit = g/cm3
  Dvalue = 7.13
  Group = -> [Bi_element001,Ge_element001,O_element012]
  conduct = 2
  density = 1
  expand = 3
  formula = G4_BGO
  name = G4_BGO
  specific = 4
FEATURE [App::DocumentObjectGroupPython] H_element014  label="H_element : 0.102"  # scripted group (container) (typed FeaturePython)
  n = 0.102
FEATURE [App::DocumentObjectGroupPython] C_element014  label="C_element : 0.110"  # scripted group (container) (typed FeaturePython)
  n = 0.11
FEATURE [App::DocumentObjectGroupPython] N_element009  label="N_element : 0.033"  # scripted group (container) (typed FeaturePython)
  n = 0.033
FEATURE [App::DocumentObjectGroupPython] O_element013  label="O_element : 0.745"  # scripted group (container) (typed FeaturePython)
  n = 0.745
FEATURE [App::DocumentObjectGroupPython] Na_element002  label="Na_element : 0.002"  # scripted group (container) (typed FeaturePython)
  n = 0.001
FEATURE [App::DocumentObjectGroupPython] P_element001  label="P_element : 0.001"  # scripted group (container) (typed FeaturePython)
  n = 0.001
FEATURE [App::DocumentObjectGroupPython] S_element003  label="S_element : 0.002"  # scripted group (container) (typed FeaturePython)
  n = 0.002
FEATURE [App::DocumentObjectGroupPython] Cl_element002  label="Cl_element : 0.003"  # scripted group (container) (typed FeaturePython)
  n = 0.003
FEATURE [App::DocumentObjectGroupPython] K_element001  label="K_element : 0.002"  # scripted group (container) (typed FeaturePython)
  n = 0.002
FEATURE [App::DocumentObjectGroupPython] Fe_element001  label="Fe_element : 0.001"  # scripted group (container) (typed FeaturePython)
  n = 0.001
FEATURE [App::DocumentObjectGroupPython] G4_BLOOD_ICRP  # scripted group (container) (typed FeaturePython)
  Dunit = g/cm3
  Dvalue = 1.06
  Group = -> [H_element014,C_element014,N_element009,O_element013,Na_element002,P_element001,S_element003,Cl_element002,K_element001,Fe_element001]
  conduct = 2
  density = 1
  expand = 3
  formula = G4_BLOOD_ICRP
  name = G4_BLOOD_ICRP
  specific = 4
FEATURE [App::DocumentObjectGroupPython] H_element015  label="H_element : 0.064"  # scripted group (container) (typed FeaturePython)
  n = 0.064
FEATURE [App::DocumentObjectGroupPython] C_element015  label="C_element : 0.278"  # scripted group (container) (typed FeaturePython)
  n = 0.278
FEATURE [App::DocumentObjectGroupPython] N_element010  label="N_element : 0.027"  # scripted group (container) (typed FeaturePython)
  n = 0.027
FEATURE [App::DocumentObjectGroupPython] O_element014  label="O_element : 0.410"  # scripted group (container) (typed FeaturePython)
  n = 0.41
FEATURE [App::DocumentObjectGroupPython] Mg_element001  label="Mg_element : 0.002"  # scripted group (container) (typed FeaturePython)
  n = 0.002
FEATURE [App::DocumentObjectGroupPython] P_element002  label="P_element : 0.070"  # scripted group (container) (typed FeaturePython)
  n = 0.07
FEATURE [App::DocumentObjectGroupPython] S_element004  label="S_element : 0.003"  # scripted group (container) (typed FeaturePython)
  n = 0.002
FEATURE [App::DocumentObjectGroupPython] Ca_element003  label="Ca_element : 0.147"  # scripted group (container) (typed FeaturePython)
  n = 0.147
FEATURE [App::DocumentObjectGroupPython] G4_BONE_COMPACT_ICRU  # scripted group (container) (typed FeaturePython)
  Dunit = g/cm3
  Dvalue = 1.85
  Group = -> [H_element015,C_element015,N_element010,O_element014,Mg_element001,P_element002,S_element004,Ca_element003]
  conduct = 2
  density = 1
  expand = 3
  formula = G4_BONE_COMPACT_ICRU
  name = G4_BONE_COMPACT_ICRU
  specific = 4
FEATURE [App::DocumentObjectGroupPython] H_element016  label="H_element : 0.034"  # scripted group (container) (typed FeaturePython)
  n = 0.034
FEATURE [App::DocumentObjectGroupPython] C_element016  label="C_element : 0.155"  # scripted group (container) (typed FeaturePython)
  n = 0.155
FEATURE [App::DocumentObjectGroupPython] N_element011  label="N_element : 0.042"  # scripted group (container) (typed FeaturePython)
  n = 0.042
FEATURE [App::DocumentObjectGroupPython] O_element015  label="O_element : 0.435"  # scripted group (container) (typed FeaturePython)
  n = 0.435
FEATURE [App::DocumentObjectGroupPython] Na_element003  label="Na_element : 0.003"  # scripted group (container) (typed FeaturePython)
  n = 0.001
FEATURE [App::DocumentObjectGroupPython] Mg_element002  label="Mg_element : 0.003"  # scripted group (container) (typed FeaturePython)
  n = 0.002
FEATURE [App::DocumentObjectGroupPython] P_element003  label="P_element : 0.103"  # scripted group (container) (typed FeaturePython)
  n = 0.103
FEATURE [App::DocumentObjectGroupPython] S_element005  label="S_element : 0.004"  # scripted group (container) (typed FeaturePython)
  n = 0.003
FEATURE [App::DocumentObjectGroupPython] Ca_element004  label="Ca_element : 0.225"  # scripted group (container) (typed FeaturePython)
  n = 0.225
FEATURE [App::DocumentObjectGroupPython] G4_BONE_CORTICAL_ICRP  # scripted group (container) (typed FeaturePython)
  Dunit = g/cm3
  Dvalue = 1.92
  Group = -> [H_element016,C_element016,N_element011,O_element015,Na_element003,Mg_element002,P_element003,S_element005,Ca_element004]
  conduct = 2
  density = 1
  expand = 3
  formula = G4_BONE_CORTICAL_ICRP
  name = G4_BONE_CORTICAL_ICRP
  specific = 4
FEATURE [App::DocumentObjectGroupPython] B_element001  label="B_element : 4"  # scripted group (container) (typed FeaturePython)
  n = 4
  ref = B_element
FEATURE [App::DocumentObjectGroupPython] C_element017  label="C_element : 1"  # scripted group (container) (typed FeaturePython)
  n = 1
  ref = C_element
FEATURE [App::DocumentObjectGroupPython] G4_BORON_CARBIDE  # scripted group (container) (typed FeaturePython)
  Dunit = g/cm3
  Dvalue = 2.52
  Group = -> [B_element001,C_element017]
  conduct = 2
  density = 1
  expand = 3
  formula = G4_BORON_CARBIDE
  name = G4_BORON_CARBIDE
  specific = 4
FEATURE [App::DocumentObjectGroupPython] B_element002  label="B_element : 2"  # scripted group (container) (typed FeaturePython)
  n = 2
  ref = B_element
FEATURE [App::DocumentObjectGroupPython] O_element016  label="O_element : 006"  # scripted group (container) (typed FeaturePython)
  n = 3
  ref = O_element
FEATURE [App::DocumentObjectGroupPython] G4_BORON_OXIDE  # scripted group (container) (typed FeaturePython)
  Dunit = g/cm3
  Dvalue = 1.812
  Group = -> [B_element002,O_element016]
  conduct = 2
  density = 1
  expand = 3
  formula = G4_BORON_OXIDE
  name = G4_BORON_OXIDE
  specific = 4
FEATURE [App::DocumentObjectGroupPython] H_element017  label="H_element : 0.107"  # scripted group (container) (typed FeaturePython)
  n = 0.107
FEATURE [App::DocumentObjectGroupPython] C_element018  label="C_element : 0.145"  # scripted group (container) (typed FeaturePython)
  n = 0.145
FEATURE [App::DocumentObjectGroupPython] N_element012  label="N_element : 0.022"  # scripted group (container) (typed FeaturePython)
  n = 0.022
FEATURE [App::DocumentObjectGroupPython] O_element017  label="O_element : 0.712"  # scripted group (container) (typed FeaturePython)
  n = 0.712
FEATURE [App::DocumentObjectGroupPython] Na_element004  label="Na_element : 0.004"  # scripted group (container) (typed FeaturePython)
  n = 0.002
FEATURE [App::DocumentObjectGroupPython] P_element004  label="P_element : 0.004"  # scripted group (container) (typed FeaturePython)
  n = 0.004
FEATURE [App::DocumentObjectGroupPython] S_element006  label="S_element : 0.005"  # scripted group (container) (typed FeaturePython)
  n = 0.002
FEATURE [App::DocumentObjectGroupPython] Cl_element003  label="Cl_element : 0.004"  # scripted group (container) (typed FeaturePython)
  n = 0.003
FEATURE [App::DocumentObjectGroupPython] K_element002  label="K_element : 0.003"  # scripted group (container) (typed FeaturePython)
  n = 0.003
FEATURE [App::DocumentObjectGroupPython] G4_BRAIN_ICRP  # scripted group (container) (typed FeaturePython)
  Dunit = g/cm3
  Dvalue = 1.04
  Group = -> [H_element017,C_element018,N_element012,O_element017,Na_element004,P_element004,S_element006,Cl_element003,K_element002]
  conduct = 2
  density = 1
  expand = 3
  formula = G4_BRAIN_ICRP
  name = G4_BRAIN_ICRP
  specific = 4
FEATURE [App::DocumentObjectGroupPython] C_element019  label="C_element : 4"  # scripted group (container) (typed FeaturePython)
  n = 4
  ref = C_element
FEATURE [App::DocumentObjectGroupPython] H_element018  label="H_element : 010"  # scripted group (container) (typed FeaturePython)
  n = 10
  ref = H_element
FEATURE [App::DocumentObjectGroupPython] G4_BUTANE  # scripted group (container) (typed FeaturePython)
  Dunit = g/cm3
  Dvalue = 0.00249343
  Group = -> [C_element019,H_element018]
  conduct = 2
  density = 1
  expand = 3
  formula = G4_BUTANE
  name = G4_BUTANE
  specific = 4
FEATURE [App::DocumentObjectGroupPython] C_element020  label="C_element : 008"  # scripted group (container) (typed FeaturePython)
  n = 4
  ref = C_element
FEATURE [App::DocumentObjectGroupPython] H_element019  label="H_element : 011"  # scripted group (container) (typed FeaturePython)
  n = 10
  ref = H_element
FEATURE [App::DocumentObjectGroupPython] O_element018  label="O_element : 007"  # scripted group (container) (typed FeaturePython)
  n = 1
  ref = O_element
FEATURE [App::DocumentObjectGroupPython] G4_N_BUTYL_ALCOHOL  label="G4_N-BUTYL_ALCOHOL"  # scripted group (container) (typed FeaturePython)
  Dunit = g/cm3
  Dvalue = 0.8098
  Group = -> [C_element020,H_element019,O_element018]
  conduct = 2
  density = 1
  expand = 3
  formula = G4_N-BUTYL_ALCOHOL
  name = G4_N-BUTYL_ALCOHOL
  specific = 4
FEATURE [App::DocumentObjectGroupPython] H_element020  label="H_element : 0.025"  # scripted group (container) (typed FeaturePython)
  n = 0.02468
FEATURE [App::DocumentObjectGroupPython] C_element021  label="C_element : 0.502"  # scripted group (container) (typed FeaturePython)
  n = 0.501611
FEATURE [App::DocumentObjectGroupPython] O_element019  label="O_element : 0.005"  # scripted group (container) (typed FeaturePython)
  n = 0.004527
FEATURE [App::DocumentObjectGroupPython] F_element004  label="F_element : 0.465"  # scripted group (container) (typed FeaturePython)
  n = 0.465209
FEATURE [App::DocumentObjectGroupPython] Si_element001  label="Si_element : 0.004"  # scripted group (container) (typed FeaturePython)
  n = 0.003973
FEATURE [App::DocumentObjectGroupPython] G4_C_552  label="G4_C-552"  # scripted group (container) (typed FeaturePython)
  Dunit = g/cm3
  Dvalue = 1.76
  Group = -> [H_element020,C_element021,O_element019,F_element004,Si_element001]
  conduct = 2
  density = 1
  expand = 3
  formula = G4_C-552
  name = G4_C-552
  specific = 4
FEATURE [App::DocumentObjectGroupPython] Cd_element001  label="Cd_element : 1"  # scripted group (container) (typed FeaturePython)
  n = 1
  ref = Cd_element
FEATURE [App::DocumentObjectGroupPython] Te_element001  label="Te_element : 1"  # scripted group (container) (typed FeaturePython)
  n = 1
  ref = Te_element
FEATURE [App::DocumentObjectGroupPython] G4_CADMIUM_TELLURIDE  # scripted group (container) (typed FeaturePython)
  Dunit = g/cm3
  Dvalue = 6.2
  Group = -> [Cd_element001,Te_element001]
  conduct = 2
  density = 1
  expand = 3
  formula = G4_CADMIUM_TELLURIDE
  name = G4_CADMIUM_TELLURIDE
  specific = 4
FEATURE [App::DocumentObjectGroupPython] Cd_element002  label="Cd_element : 002"  # scripted group (container) (typed FeaturePython)
  n = 1
  ref = Cd_element
FEATURE [App::DocumentObjectGroupPython] W_element001  label="W_element : 1"  # scripted group (container) (typed FeaturePython)
  n = 1
  ref = W_element
FEATURE [App::DocumentObjectGroupPython] O_element020  label="O_element : 008"  # scripted group (container) (typed FeaturePython)
  n = 4
  ref = O_element
FEATURE [App::DocumentObjectGroupPython] G4_CADMIUM_TUNGSTATE  # scripted group (container) (typed FeaturePython)
  Dunit = g/cm3
  Dvalue = 7.9
  Group = -> [Cd_element002,W_element001,O_element020]
  conduct = 2
  density = 1
  expand = 3
  formula = G4_CADMIUM_TUNGSTATE
  name = G4_CADMIUM_TUNGSTATE
  specific = 4
FEATURE [App::DocumentObjectGroupPython] Ca_element005  label="Ca_element : 1"  # scripted group (container) (typed FeaturePython)
  n = 1
  ref = Ca_element
FEATURE [App::DocumentObjectGroupPython] C_element022  label="C_element : 009"  # scripted group (container) (typed FeaturePython)
  n = 1
  ref = C_element
FEATURE [App::DocumentObjectGroupPython] O_element021  label="O_element : 009"  # scripted group (container) (typed FeaturePython)
  n = 3
  ref = O_element
FEATURE [App::DocumentObjectGroupPython] G4_CALCIUM_CARBONATE  # scripted group (container) (typed FeaturePython)
  Dunit = g/cm3
  Dvalue = 2.8
  Group = -> [Ca_element005,C_element022,O_element021]
  conduct = 2
  density = 1
  expand = 3
  formula = G4_CALCIUM_CARBONATE
  name = G4_CALCIUM_CARBONATE
  specific = 4
FEATURE [App::DocumentObjectGroupPython] Ca_element006  label="Ca_element : 002"  # scripted group (container) (typed FeaturePython)
  n = 1
  ref = Ca_element
FEATURE [App::DocumentObjectGroupPython] F_element005  label="F_element : 003"  # scripted group (container) (typed FeaturePython)
  n = 2
  ref = F_element
FEATURE [App::DocumentObjectGroupPython] G4_CALCIUM_FLUORIDE  # scripted group (container) (typed FeaturePython)
  Dunit = g/cm3
  Dvalue = 3.18
  Group = -> [Ca_element006,F_element005]
  conduct = 2
  density = 1
  expand = 3
  formula = G4_CALCIUM_FLUORIDE
  name = G4_CALCIUM_FLUORIDE
  specific = 4
FEATURE [App::DocumentObjectGroupPython] Ca_element007  label="Ca_element : 003"  # scripted group (container) (typed FeaturePython)
  n = 1
  ref = Ca_element
FEATURE [App::DocumentObjectGroupPython] O_element022  label="O_element : 010"  # scripted group (container) (typed FeaturePython)
  n = 1
  ref = O_element
FEATURE [App::DocumentObjectGroupPython] G4_CALCIUM_OXIDE  # scripted group (container) (typed FeaturePython)
  Dunit = g/cm3
  Dvalue = 3.3
  Group = -> [Ca_element007,O_element022]
  conduct = 2
  density = 1
  expand = 3
  formula = G4_CALCIUM_OXIDE
  name = G4_CALCIUM_OXIDE
  specific = 4
FEATURE [App::DocumentObjectGroupPython] Ca_element008  label="Ca_element : 004"  # scripted group (container) (typed FeaturePython)
  n = 1
  ref = Ca_element
FEATURE [App::DocumentObjectGroupPython] S_element007  label="S_element : 002"  # scripted group (container) (typed FeaturePython)
  n = 1
  ref = S_element
FEATURE [App::DocumentObjectGroupPython] O_element023  label="O_element : 011"  # scripted group (container) (typed FeaturePython)
  n = 4
  ref = O_element
FEATURE [App::DocumentObjectGroupPython] G4_CALCIUM_SULFATE  # scripted group (container) (typed FeaturePython)
  Dunit = g/cm3
  Dvalue = 2.96
  Group = -> [Ca_element008,S_element007,O_element023]
  conduct = 2
  density = 1
  expand = 3
  formula = G4_CALCIUM_SULFATE
  name = G4_CALCIUM_SULFATE
  specific = 4
FEATURE [App::DocumentObjectGroupPython] Ca_element009  label="Ca_element : 005"  # scripted group (container) (typed FeaturePython)
  n = 1
  ref = Ca_element
FEATURE [App::DocumentObjectGroupPython] W_element002  label="W_element : 002"  # scripted group (container) (typed FeaturePython)
  n = 1
  ref = W_element
FEATURE [App::DocumentObjectGroupPython] O_element024  label="O_element : 012"  # scripted group (container) (typed FeaturePython)
  n = 4
  ref = O_element
FEATURE [App::DocumentObjectGroupPython] G4_CALCIUM_TUNGSTATE  # scripted group (container) (typed FeaturePython)
  Dunit = g/cm3
  Dvalue = 6.062
  Group = -> [Ca_element009,W_element002,O_element024]
  conduct = 2
  density = 1
  expand = 3
  formula = G4_CALCIUM_TUNGSTATE
  name = G4_CALCIUM_TUNGSTATE
  specific = 4
FEATURE [App::DocumentObjectGroupPython] C_element023  label="C_element : 010"  # scripted group (container) (typed FeaturePython)
  n = 1
  ref = C_element
FEATURE [App::DocumentObjectGroupPython] O_element025  label="O_element : 013"  # scripted group (container) (typed FeaturePython)
  n = 2
  ref = O_element
FEATURE [App::DocumentObjectGroupPython] G4_CARBON_DIOXIDE  # scripted group (container) (typed FeaturePython)
  Dunit = g/cm3
  Dvalue = 0.00184212
  Group = -> [C_element023,O_element025]
  conduct = 2
  density = 1
  expand = 3
  formula = G4_CARBON_DIOXIDE
  name = G4_CARBON_DIOXIDE
  specific = 4
FEATURE [App::DocumentObjectGroupPython] C_element024  label="C_element : 011"  # scripted group (container) (typed FeaturePython)
  n = 1
  ref = C_element
FEATURE [App::DocumentObjectGroupPython] Cl_element004  label="Cl_element : 4"  # scripted group (container) (typed FeaturePython)
  n = 4
  ref = Cl_element
FEATURE [App::DocumentObjectGroupPython] G4_CARBON_TETRACHLORIDE  # scripted group (container) (typed FeaturePython)
  Dunit = g/cm3
  Dvalue = 1.594
  Group = -> [C_element024,Cl_element004]
  conduct = 2
  density = 1
  expand = 3
  formula = G4_CARBON_TETRACHLORIDE
  name = G4_CARBON_TETRACHLORIDE
  specific = 4
FEATURE [App::DocumentObjectGroupPython] C_element025  label="C_element : 012"  # scripted group (container) (typed FeaturePython)
  n = 6
  ref = C_element
FEATURE [App::DocumentObjectGroupPython] H_element021  label="H_element : 012"  # scripted group (container) (typed FeaturePython)
  n = 10
  ref = H_element
FEATURE [App::DocumentObjectGroupPython] O_element026  label="O_element : 5"  # scripted group (container) (typed FeaturePython)
  n = 5
  ref = O_element
FEATURE [App::DocumentObjectGroupPython] G4_CELLULOSE_CELLOPHANE  # scripted group (container) (typed FeaturePython)
  Dunit = g/cm3
  Dvalue = 1.42
  Group = -> [C_element025,H_element021,O_element026]
  conduct = 2
  density = 1
  expand = 3
  formula = G4_CELLULOSE_CELLOPHANE
  name = G4_CELLULOSE_CELLOPHANE
  specific = 4
FEATURE [App::DocumentObjectGroupPython] H_element022  label="H_element : 0.067"  # scripted group (container) (typed FeaturePython)
  n = 0.067125
FEATURE [App::DocumentObjectGroupPython] C_element026  label="C_element : 0.545"  # scripted group (container) (typed FeaturePython)
  n = 0.545403
FEATURE [App::DocumentObjectGroupPython] O_element027  label="O_element : 0.387"  # scripted group (container) (typed FeaturePython)
  n = 0.387472
FEATURE [App::DocumentObjectGroupPython] G4_CELLULOSE_BUTYRATE  # scripted group (container) (typed FeaturePython)
  Dunit = g/cm3
  Dvalue = 1.2
  Group = -> [H_element022,C_element026,O_element027]
  conduct = 2
  density = 1
  expand = 3
  formula = G4_CELLULOSE_BUTYRATE
  name = G4_CELLULOSE_BUTYRATE
  specific = 4
FEATURE [App::DocumentObjectGroupPython] H_element023  label="H_element : 0.029"  # scripted group (container) (typed FeaturePython)
  n = 0.029216
FEATURE [App::DocumentObjectGroupPython] C_element027  label="C_element : 0.271"  # scripted group (container) (typed FeaturePython)
  n = 0.271296
FEATURE [App::DocumentObjectGroupPython] N_element013  label="N_element : 0.121"  # scripted group (container) (typed FeaturePython)
  n = 0.121276
FEATURE [App::DocumentObjectGroupPython] O_element028  label="O_element : 0.578"  # scripted group (container) (typed FeaturePython)
  n = 0.578212
FEATURE [App::DocumentObjectGroupPython] G4_CELLULOSE_NITRATE  # scripted group (container) (typed FeaturePython)
  Dunit = g/cm3
  Dvalue = 1.49
  Group = -> [H_element023,C_element027,N_element013,O_element028]
  conduct = 2
  density = 1
  expand = 3
  formula = G4_CELLULOSE_NITRATE
  name = G4_CELLULOSE_NITRATE
  specific = 4
FEATURE [App::DocumentObjectGroupPython] H_element024  label="H_element : 0.108"  # scripted group (container) (typed FeaturePython)
  n = 0.107596
FEATURE [App::DocumentObjectGroupPython] N_element014  label="N_element : 0.001"  # scripted group (container) (typed FeaturePython)
  n = 0.0008
FEATURE [App::DocumentObjectGroupPython] O_element029  label="O_element : 0.875"  # scripted group (container) (typed FeaturePython)
  n = 0.874976
FEATURE [App::DocumentObjectGroupPython] S_element008  label="S_element : 0.015"  # scripted group (container) (typed FeaturePython)
  n = 0.014627
FEATURE [App::DocumentObjectGroupPython] Ce_element001  label="Ce_element : 0.002"  # scripted group (container) (typed FeaturePython)
  n = 0.002001
FEATURE [App::DocumentObjectGroupPython] G4_CERIC_SULFATE  # scripted group (container) (typed FeaturePython)
  Dunit = g/cm3
  Dvalue = 1.03
  Group = -> [H_element024,N_element014,O_element029,S_element008,Ce_element001]
  conduct = 2
  density = 1
  expand = 3
  formula = G4_CERIC_SULFATE
  name = G4_CERIC_SULFATE
  specific = 4
FEATURE [App::DocumentObjectGroupPython] Cs_element001  label="Cs_element : 1"  # scripted group (container) (typed FeaturePython)
  n = 1
  ref = Cs_element
FEATURE [App::DocumentObjectGroupPython] F_element006  label="F_element : 1"  # scripted group (container) (typed FeaturePython)
  n = 1
  ref = F_element
FEATURE [App::DocumentObjectGroupPython] G4_CESIUM_FLUORIDE  # scripted group (container) (typed FeaturePython)
  Dunit = g/cm3
  Dvalue = 4.115
  Group = -> [Cs_element001,F_element006]
  conduct = 2
  density = 1
  expand = 3
  formula = G4_CESIUM_FLUORIDE
  name = G4_CESIUM_FLUORIDE
  specific = 4
FEATURE [App::DocumentObjectGroupPython] Cs_element002  label="Cs_element : 002"  # scripted group (container) (typed FeaturePython)
  n = 1
  ref = Cs_element
FEATURE [App::DocumentObjectGroupPython] I_element001  label="I_element : 1"  # scripted group (container) (typed FeaturePython)
  n = 1
  ref = I_element
FEATURE [App::DocumentObjectGroupPython] G4_CESIUM_IODIDE001  label="G4_CESIUM_IODIDE"  # scripted group (container) (typed FeaturePython)
  Dunit = g/cm3
  Dvalue = 4.51
  Group = -> [Cs_element002,I_element001]
  conduct = 2
  density = 1
  expand = 3
  formula = G4_CESIUM_IODIDE
  name = G4_CESIUM_IODIDE
  specific = 4
FEATURE [App::DocumentObjectGroupPython] C_element028  label="C_element : 013"  # scripted group (container) (typed FeaturePython)
  n = 6
  ref = C_element
FEATURE [App::DocumentObjectGroupPython] H_element025  label="H_element : 013"  # scripted group (container) (typed FeaturePython)
  n = 5
  ref = H_element
FEATURE [App::DocumentObjectGroupPython] Cl_element005  label="Cl_element : 1"  # scripted group (container) (typed FeaturePython)
  n = 1
  ref = Cl_element
FEATURE [App::DocumentObjectGroupPython] G4_CHLOROBENZENE  # scripted group (container) (typed FeaturePython)
  Dunit = g/cm3
  Dvalue = 1.1058
  Group = -> [C_element028,H_element025,Cl_element005]
  conduct = 2
  density = 1
  expand = 3
  formula = G4_CHLOROBENZENE
  name = G4_CHLOROBENZENE
  specific = 4
FEATURE [App::DocumentObjectGroupPython] C_element029  label="C_element : 014"  # scripted group (container) (typed FeaturePython)
  n = 1
  ref = C_element
FEATURE [App::DocumentObjectGroupPython] H_element026  label="H_element : 1"  # scripted group (container) (typed FeaturePython)
  n = 1
  ref = H_element
FEATURE [App::DocumentObjectGroupPython] Cl_element006  label="Cl_element : 3"  # scripted group (container) (typed FeaturePython)
  n = 3
  ref = Cl_element
FEATURE [App::DocumentObjectGroupPython] G4_CHLOROFORM  # scripted group (container) (typed FeaturePython)
  Dunit = g/cm3
  Dvalue = 1.4832
  Group = -> [C_element029,H_element026,Cl_element006]
  conduct = 2
  density = 1
  expand = 3
  formula = G4_CHLOROFORM
  name = G4_CHLOROFORM
  specific = 4
FEATURE [App::DocumentObjectGroupPython] H_element027  label="H_element : 0.010"  # scripted group (container) (typed FeaturePython)
  n = 0.01
FEATURE [App::DocumentObjectGroupPython] C_element030  label="C_element : 0.001"  # scripted group (container) (typed FeaturePython)
  n = 0.001
FEATURE [App::DocumentObjectGroupPython] O_element030  label="O_element : 0.529"  # scripted group (container) (typed FeaturePython)
  n = 0.529107
FEATURE [App::DocumentObjectGroupPython] Na_element005  label="Na_element : 0.016"  # scripted group (container) (typed FeaturePython)
  n = 0.016
FEATURE [App::DocumentObjectGroupPython] Mg_element003  label="Mg_element : 0.004"  # scripted group (container) (typed FeaturePython)
  n = 0.002
FEATURE [App::DocumentObjectGroupPython] Al_element002  label="Al_element : 0.034"  # scripted group (container) (typed FeaturePython)
  n = 0.033872
FEATURE [App::DocumentObjectGroupPython] Si_element002  label="Si_element : 0.337"  # scripted group (container) (typed FeaturePython)
  n = 0.337021
FEATURE [App::DocumentObjectGroupPython] K_element003  label="K_element : 0.013"  # scripted group (container) (typed FeaturePython)
  n = 0.013
FEATURE [App::DocumentObjectGroupPython] Ca_element010  label="Ca_element : 0.044"  # scripted group (container) (typed FeaturePython)
  n = 0.044
FEATURE [App::DocumentObjectGroupPython] Fe_element002  label="Fe_element : 0.014"  # scripted group (container) (typed FeaturePython)
  n = 0.014
FEATURE [App::DocumentObjectGroupPython] G4_CONCRETE  # scripted group (container) (typed FeaturePython)
  Dunit = g/cm3
  Dvalue = 2.3
  Group = -> [H_element027,C_element030,O_element030,Na_element005,Mg_element003,Al_element002,Si_element002,K_element003,Ca_element010,Fe_element002]
  conduct = 2
  density = 1
  expand = 3
  formula = G4_CONCRETE
  name = G4_CONCRETE
  specific = 4
FEATURE [App::DocumentObjectGroupPython] C_element031  label="C_element : 015"  # scripted group (container) (typed FeaturePython)
  n = 6
  ref = C_element
FEATURE [App::DocumentObjectGroupPython] H_element028  label="H_element : 12"  # scripted group (container) (typed FeaturePython)
  n = 12
  ref = H_element
FEATURE [App::DocumentObjectGroupPython] G4_CYCLOHEXANE  # scripted group (container) (typed FeaturePython)
  Dunit = g/cm3
  Dvalue = 0.779
  Group = -> [C_element031,H_element028]
  conduct = 2
  density = 1
  expand = 3
  formula = G4_CYCLOHEXANE
  name = G4_CYCLOHEXANE
  specific = 4
FEATURE [App::DocumentObjectGroupPython] C_element032  label="C_element : 016"  # scripted group (container) (typed FeaturePython)
  n = 6
  ref = C_element
FEATURE [App::DocumentObjectGroupPython] H_element029  label="H_element : 4"  # scripted group (container) (typed FeaturePython)
  n = 4
  ref = H_element
FEATURE [App::DocumentObjectGroupPython] Cl_element007  label="Cl_element : 2"  # scripted group (container) (typed FeaturePython)
  n = 2
  ref = Cl_element
FEATURE [App::DocumentObjectGroupPython] G4_1_2_DICHLOROBENZENE  label="G4_1.2-DICHLOROBENZENE"  # scripted group (container) (typed FeaturePython)
  Dunit = g/cm3
  Dvalue = 1.3048
  Group = -> [C_element032,H_element029,Cl_element007]
  conduct = 2
  density = 1
  expand = 3
  formula = G4_1.2-DICHLOROBENZENE
  name = G4_1.2-DICHLOROBENZENE
  specific = 4
FEATURE [App::DocumentObjectGroupPython] C_element033  label="C_element : 017"  # scripted group (container) (typed FeaturePython)
  n = 4
  ref = C_element
FEATURE [App::DocumentObjectGroupPython] H_element030  label="H_element : 8"  # scripted group (container) (typed FeaturePython)
  n = 8
  ref = H_element
FEATURE [App::DocumentObjectGroupPython] O_element031  label="O_element : 014"  # scripted group (container) (typed FeaturePython)
  n = 1
  ref = O_element
FEATURE [App::DocumentObjectGroupPython] Cl_element008  label="Cl_element : 005"  # scripted group (container) (typed FeaturePython)
  n = 2
  ref = Cl_element
FEATURE [App::DocumentObjectGroupPython] G4_DICHLORODIETHYL_ETHER  # scripted group (container) (typed FeaturePython)
  Dunit = g/cm3
  Dvalue = 1.2199
  Group = -> [C_element033,H_element030,O_element031,Cl_element008]
  conduct = 2
  density = 1
  expand = 3
  formula = G4_DICHLORODIETHYL_ETHER
  name = G4_DICHLORODIETHYL_ETHER
  specific = 4
FEATURE [App::DocumentObjectGroupPython] C_element034  label="C_element : 018"  # scripted group (container) (typed FeaturePython)
  n = 2
  ref = C_element
FEATURE [App::DocumentObjectGroupPython] H_element031  label="H_element : 014"  # scripted group (container) (typed FeaturePython)
  n = 4
  ref = H_element
FEATURE [App::DocumentObjectGroupPython] Cl_element009  label="Cl_element : 006"  # scripted group (container) (typed FeaturePython)
  n = 2
  ref = Cl_element
FEATURE [App::DocumentObjectGroupPython] G4_1_2_DICHLOROETHANE  label="G4_1.2-DICHLOROETHANE"  # scripted group (container) (typed FeaturePython)
  Dunit = g/cm3
  Dvalue = 1.2351
  Group = -> [C_element034,H_element031,Cl_element009]
  conduct = 2
  density = 1
  expand = 3
  formula = G4_1.2-DICHLOROETHANE
  name = G4_1.2-DICHLOROETHANE
  specific = 4
FEATURE [App::DocumentObjectGroupPython] C_element035  label="C_element : 019"  # scripted group (container) (typed FeaturePython)
  n = 4
  ref = C_element
FEATURE [App::DocumentObjectGroupPython] H_element032  label="H_element : 015"  # scripted group (container) (typed FeaturePython)
  n = 10
  ref = H_element
FEATURE [App::DocumentObjectGroupPython] O_element032  label="O_element : 015"  # scripted group (container) (typed FeaturePython)
  n = 1
  ref = O_element
FEATURE [App::DocumentObjectGroupPython] G4_DIETHYL_ETHER  # scripted group (container) (typed FeaturePython)
  Dunit = g/cm3
  Dvalue = 0.71378
  Group = -> [C_element035,H_element032,O_element032]
  conduct = 2
  density = 1
  expand = 3
  formula = G4_DIETHYL_ETHER
  name = G4_DIETHYL_ETHER
  specific = 4
FEATURE [App::DocumentObjectGroupPython] C_element036  label="C_element : 020"  # scripted group (container) (typed FeaturePython)
  n = 3
  ref = C_element
FEATURE [App::DocumentObjectGroupPython] H_element033  label="H_element : 016"  # scripted group (container) (typed FeaturePython)
  n = 7
  ref = H_element
FEATURE [App::DocumentObjectGroupPython] N_element015  label="N_element : 008"  # scripted group (container) (typed FeaturePython)
  n = 1
  ref = N_element
FEATURE [App::DocumentObjectGroupPython] O_element033  label="O_element : 016"  # scripted group (container) (typed FeaturePython)
  n = 1
  ref = O_element
FEATURE [App::DocumentObjectGroupPython] G4_N_N_DIMETHYL_FORMAMIDE  label="G4_N.N-DIMETHYL_FORMAMIDE"  # scripted group (container) (typed FeaturePython)
  Dunit = g/cm3
  Dvalue = 0.9487
  Group = -> [C_element036,H_element033,N_element015,O_element033]
  conduct = 2
  density = 1
  expand = 3
  formula = G4_N.N-DIMETHYL_FORMAMIDE
  name = G4_N.N-DIMETHYL_FORMAMIDE
  specific = 4
FEATURE [App::DocumentObjectGroupPython] C_element037  label="C_element : 021"  # scripted group (container) (typed FeaturePython)
  n = 2
  ref = C_element
FEATURE [App::DocumentObjectGroupPython] H_element034  label="H_element : 017"  # scripted group (container) (typed FeaturePython)
  n = 6
  ref = H_element
FEATURE [App::DocumentObjectGroupPython] O_element034  label="O_element : 017"  # scripted group (container) (typed FeaturePython)
  n = 1
  ref = O_element
FEATURE [App::DocumentObjectGroupPython] S_element009  label="S_element : 003"  # scripted group (container) (typed FeaturePython)
  n = 1
  ref = S_element
FEATURE [App::DocumentObjectGroupPython] G4_DIMETHYL_SULFOXIDE  # scripted group (container) (typed FeaturePython)
  Dunit = g/cm3
  Dvalue = 1.1014
  Group = -> [C_element037,H_element034,O_element034,S_element009]
  conduct = 2
  density = 1
  expand = 3
  formula = G4_DIMETHYL_SULFOXIDE
  name = G4_DIMETHYL_SULFOXIDE
  specific = 4
FEATURE [App::DocumentObjectGroupPython] C_element038  label="C_element : 022"  # scripted group (container) (typed FeaturePython)
  n = 2
  ref = C_element
FEATURE [App::DocumentObjectGroupPython] H_element035  label="H_element : 018"  # scripted group (container) (typed FeaturePython)
  n = 6
  ref = H_element
FEATURE [App::DocumentObjectGroupPython] G4_ETHANE  # scripted group (container) (typed FeaturePython)
  Dunit = g/cm3
  Dvalue = 0.00125324
  Group = -> [C_element038,H_element035]
  conduct = 2
  density = 1
  expand = 3
  formula = G4_ETHANE
  name = G4_ETHANE
  specific = 4
FEATURE [App::DocumentObjectGroupPython] C_element039  label="C_element : 023"  # scripted group (container) (typed FeaturePython)
  n = 2
  ref = C_element
FEATURE [App::DocumentObjectGroupPython] H_element036  label="H_element : 019"  # scripted group (container) (typed FeaturePython)
  n = 6
  ref = H_element
FEATURE [App::DocumentObjectGroupPython] O_element035  label="O_element : 018"  # scripted group (container) (typed FeaturePython)
  n = 1
  ref = O_element
FEATURE [App::DocumentObjectGroupPython] G4_ETHYL_ALCOHOL  # scripted group (container) (typed FeaturePython)
  Dunit = g/cm3
  Dvalue = 0.7893
  Group = -> [C_element039,H_element036,O_element035]
  conduct = 2
  density = 1
  expand = 3
  formula = G4_ETHYL_ALCOHOL
  name = G4_ETHYL_ALCOHOL
  specific = 4
FEATURE [App::DocumentObjectGroupPython] H_element037  label="H_element : 0.090"  # scripted group (container) (typed FeaturePython)
  n = 0.090027
FEATURE [App::DocumentObjectGroupPython] C_element040  label="C_element : 0.585"  # scripted group (container) (typed FeaturePython)
  n = 0.585182
FEATURE [App::DocumentObjectGroupPython] O_element036  label="O_element : 0.325"  # scripted group (container) (typed FeaturePython)
  n = 0.324791
FEATURE [App::DocumentObjectGroupPython] G4_ETHYL_CELLULOSE  # scripted group (container) (typed FeaturePython)
  Dunit = g/cm3
  Dvalue = 1.13
  Group = -> [H_element037,C_element040,O_element036]
  conduct = 2
  density = 1
  expand = 3
  formula = G4_ETHYL_CELLULOSE
  name = G4_ETHYL_CELLULOSE
  specific = 4
FEATURE [App::DocumentObjectGroupPython] C_element041  label="C_element : 024"  # scripted group (container) (typed FeaturePython)
  n = 2
  ref = C_element
FEATURE [App::DocumentObjectGroupPython] H_element038  label="H_element : 020"  # scripted group (container) (typed FeaturePython)
  n = 4
  ref = H_element
FEATURE [App::DocumentObjectGroupPython] G4_ETHYLENE  # scripted group (container) (typed FeaturePython)
  Dunit = g/cm3
  Dvalue = 0.00117497
  Group = -> [C_element041,H_element038]
  conduct = 2
  density = 1
  expand = 3
  formula = G4_ETHYLENE
  name = G4_ETHYLENE
  specific = 4
FEATURE [App::DocumentObjectGroupPython] H_element039  label="H_element : 0.096"  # scripted group (container) (typed FeaturePython)
  n = 0.096
FEATURE [App::DocumentObjectGroupPython] C_element042  label="C_element : 0.195"  # scripted group (container) (typed FeaturePython)
  n = 0.195
FEATURE [App::DocumentObjectGroupPython] N_element016  label="N_element : 0.057"  # scripted group (container) (typed FeaturePython)
  n = 0.057
FEATURE [App::DocumentObjectGroupPython] O_element037  label="O_element : 0.646"  # scripted group (container) (typed FeaturePython)
  n = 0.646
FEATURE [App::DocumentObjectGroupPython] Na_element006  label="Na_element : 0.017"  # scripted group (container) (typed FeaturePython)
  n = 0.001
FEATURE [App::DocumentObjectGroupPython] P_element005  label="P_element : 0.104"  # scripted group (container) (typed FeaturePython)
  n = 0.001
FEATURE [App::DocumentObjectGroupPython] S_element010  label="S_element : 0.016"  # scripted group (container) (typed FeaturePython)
  n = 0.003
FEATURE [App::DocumentObjectGroupPython] Cl_element010  label="Cl_element : 0.005"  # scripted group (container) (typed FeaturePython)
  n = 0.001
FEATURE [App::DocumentObjectGroupPython] G4_EYE_LENS_ICRP  # scripted group (container) (typed FeaturePython)
  Dunit = g/cm3
  Dvalue = 1.07
  Group = -> [H_element039,C_element042,N_element016,O_element037,Na_element006,P_element005,S_element010,Cl_element010]
  conduct = 2
  density = 1
  expand = 3
  formula = G4_EYE_LENS_ICRP
  name = G4_EYE_LENS_ICRP
  specific = 4
FEATURE [App::DocumentObjectGroupPython] Fe_element003  label="Fe_element : 2"  # scripted group (container) (typed FeaturePython)
  n = 2
  ref = Fe_element
FEATURE [App::DocumentObjectGroupPython] O_element038  label="O_element : 019"  # scripted group (container) (typed FeaturePython)
  n = 3
  ref = O_element
FEATURE [App::DocumentObjectGroupPython] G4_FERRIC_OXIDE  # scripted group (container) (typed FeaturePython)
  Dunit = g/cm3
  Dvalue = 5.2
  Group = -> [Fe_element003,O_element038]
  conduct = 2
  density = 1
  expand = 3
  formula = G4_FERRIC_OXIDE
  name = G4_FERRIC_OXIDE
  specific = 4
FEATURE [App::DocumentObjectGroupPython] Fe_element004  label="Fe_element : 1"  # scripted group (container) (typed FeaturePython)
  n = 1
  ref = Fe_element
FEATURE [App::DocumentObjectGroupPython] B_element003  label="B_element : 1"  # scripted group (container) (typed FeaturePython)
  n = 1
  ref = B_element
FEATURE [App::DocumentObjectGroupPython] G4_FERROBORIDE  # scripted group (container) (typed FeaturePython)
  Dunit = g/cm3
  Dvalue = 7.15
  Group = -> [Fe_element004,B_element003]
  conduct = 2
  density = 1
  expand = 3
  formula = G4_FERROBORIDE
  name = G4_FERROBORIDE
  specific = 4
FEATURE [App::DocumentObjectGroupPython] Fe_element005  label="Fe_element : 003"  # scripted group (container) (typed FeaturePython)
  n = 1
  ref = Fe_element
FEATURE [App::DocumentObjectGroupPython] O_element039  label="O_element : 020"  # scripted group (container) (typed FeaturePython)
  n = 1
  ref = O_element
FEATURE [App::DocumentObjectGroupPython] G4_FERROUS_OXIDE  # scripted group (container) (typed FeaturePython)
  Dunit = g/cm3
  Dvalue = 5.7
  Group = -> [Fe_element005,O_element039]
  conduct = 2
  density = 1
  expand = 3
  formula = G4_FERROUS_OXIDE
  name = G4_FERROUS_OXIDE
  specific = 4
FEATURE [App::DocumentObjectGroupPython] H_element040  label="H_element : 0.115"  # scripted group (container) (typed FeaturePython)
  n = 0.108259
FEATURE [App::DocumentObjectGroupPython] N_element017  label="N_element : 0.000"  # scripted group (container) (typed FeaturePython)
  n = 2.7e-05
FEATURE [App::DocumentObjectGroupPython] O_element040  label="O_element : 0.879"  # scripted group (container) (typed FeaturePython)
  n = 0.878636
FEATURE [App::DocumentObjectGroupPython] Na_element007  label="Na_element : 0.000"  # scripted group (container) (typed FeaturePython)
  n = 2.2e-05
FEATURE [App::DocumentObjectGroupPython] S_element011  label="S_element : 0.013"  # scripted group (container) (typed FeaturePython)
  n = 0.012968
FEATURE [App::DocumentObjectGroupPython] Cl_element011  label="Cl_element : 0.000"  # scripted group (container) (typed FeaturePython)
  n = 3.4e-05
FEATURE [App::DocumentObjectGroupPython] Fe_element006  label="Fe_element : 0.000"  # scripted group (container) (typed FeaturePython)
  n = 5.4e-05
FEATURE [App::DocumentObjectGroupPython] G4_FERROUS_SULFATE  # scripted group (container) (typed FeaturePython)
  Dunit = g/cm3
  Dvalue = 1.024
  Group = -> [H_element040,N_element017,O_element040,Na_element007,S_element011,Cl_element011,Fe_element006]
  conduct = 2
  density = 1
  expand = 3
  formula = G4_FERROUS_SULFATE
  name = G4_FERROUS_SULFATE
  specific = 4
FEATURE [App::DocumentObjectGroupPython] C_element043  label="C_element : 0.099"  # scripted group (container) (typed FeaturePython)
  n = 0.099335
FEATURE [App::DocumentObjectGroupPython] F_element007  label="F_element : 0.314"  # scripted group (container) (typed FeaturePython)
  n = 0.314247
FEATURE [App::DocumentObjectGroupPython] Cl_element012  label="Cl_element : 0.586"  # scripted group (container) (typed FeaturePython)
  n = 0.586418
FEATURE [App::DocumentObjectGroupPython] G4_FREON_12  label="G4_FREON-12"  # scripted group (container) (typed FeaturePython)
  Dunit = g/cm3
  Dvalue = 1.12
  Group = -> [C_element043,F_element007,Cl_element012]
  conduct = 2
  density = 1
  expand = 3
  formula = G4_FREON-12
  name = G4_FREON-12
  specific = 4
FEATURE [App::DocumentObjectGroupPython] C_element044  label="C_element : 0.057"  # scripted group (container) (typed FeaturePython)
  n = 0.057245
FEATURE [App::DocumentObjectGroupPython] F_element008  label="F_element : 0.181"  # scripted group (container) (typed FeaturePython)
  n = 0.181096
FEATURE [App::DocumentObjectGroupPython] Br_element001  label="Br_element : 0.762"  # scripted group (container) (typed FeaturePython)
  n = 0.761659
FEATURE [App::DocumentObjectGroupPython] G4_FREON_12B2  label="G4_FREON-12B2"  # scripted group (container) (typed FeaturePython)
  Dunit = g/cm3
  Dvalue = 1.8
  Group = -> [C_element044,F_element008,Br_element001]
  conduct = 2
  density = 1
  expand = 3
  formula = G4_FREON-12B2
  name = G4_FREON-12B2
  specific = 4
FEATURE [App::DocumentObjectGroupPython] C_element045  label="C_element : 0.115"  # scripted group (container) (typed FeaturePython)
  n = 0.114983
FEATURE [App::DocumentObjectGroupPython] F_element009  label="F_element : 0.546"  # scripted group (container) (typed FeaturePython)
  n = 0.545621
FEATURE [App::DocumentObjectGroupPython] Cl_element013  label="Cl_element : 0.339"  # scripted group (container) (typed FeaturePython)
  n = 0.339396
FEATURE [App::DocumentObjectGroupPython] G4_FREON_13  label="G4_FREON-13"  # scripted group (container) (typed FeaturePython)
  Dunit = g/cm3
  Dvalue = 0.95
  Group = -> [C_element045,F_element009,Cl_element013]
  conduct = 2
  density = 1
  expand = 3
  formula = G4_FREON-13
  name = G4_FREON-13
  specific = 4
FEATURE [App::DocumentObjectGroupPython] C_element046  label="C_element : 025"  # scripted group (container) (typed FeaturePython)
  n = 1
  ref = C_element
FEATURE [App::DocumentObjectGroupPython] F_element010  label="F_element : 3"  # scripted group (container) (typed FeaturePython)
  n = 3
  ref = F_element
FEATURE [App::DocumentObjectGroupPython] Br_element002  label="Br_element : 1"  # scripted group (container) (typed FeaturePython)
  n = 1
  ref = Br_element
FEATURE [App::DocumentObjectGroupPython] G4_FREON_13B1  label="G4_FREON-13B1"  # scripted group (container) (typed FeaturePython)
  Dunit = g/cm3
  Dvalue = 1.5
  Group = -> [C_element046,F_element010,Br_element002]
  conduct = 2
  density = 1
  expand = 3
  formula = G4_FREON-13B1
  name = G4_FREON-13B1
  specific = 4
FEATURE [App::DocumentObjectGroupPython] C_element047  label="C_element : 0.061"  # scripted group (container) (typed FeaturePython)
  n = 0.061309
FEATURE [App::DocumentObjectGroupPython] F_element011  label="F_element : 0.291"  # scripted group (container) (typed FeaturePython)
  n = 0.290924
FEATURE [App::DocumentObjectGroupPython] I_element002  label="I_element : 0.648"  # scripted group (container) (typed FeaturePython)
  n = 0.647767
FEATURE [App::DocumentObjectGroupPython] G4_FREON_13I1  label="G4_FREON-13I1"  # scripted group (container) (typed FeaturePython)
  Dunit = g/cm3
  Dvalue = 1.8
  Group = -> [C_element047,F_element011,I_element002]
  conduct = 2
  density = 1
  expand = 3
  formula = G4_FREON-13I1
  name = G4_FREON-13I1
  specific = 4
FEATURE [App::DocumentObjectGroupPython] Gd_element001  label="Gd_element : 2"  # scripted group (container) (typed FeaturePython)
  n = 2
  ref = Gd_element
FEATURE [App::DocumentObjectGroupPython] O_element041  label="O_element : 021"  # scripted group (container) (typed FeaturePython)
  n = 2
  ref = O_element
FEATURE [App::DocumentObjectGroupPython] S_element012  label="S_element : 004"  # scripted group (container) (typed FeaturePython)
  n = 1
  ref = S_element
FEATURE [App::DocumentObjectGroupPython] G4_GADOLINIUM_OXYSULFIDE  # scripted group (container) (typed FeaturePython)
  Dunit = g/cm3
  Dvalue = 7.44
  Group = -> [Gd_element001,O_element041,S_element012]
  conduct = 2
  density = 1
  expand = 3
  formula = G4_GADOLINIUM_OXYSULFIDE
  name = G4_GADOLINIUM_OXYSULFIDE
  specific = 4
FEATURE [App::DocumentObjectGroupPython] Ga_element001  label="Ga_element : 1"  # scripted group (container) (typed FeaturePython)
  n = 1
  ref = Ga_element
FEATURE [App::DocumentObjectGroupPython] As_element001  label="As_element : 1"  # scripted group (container) (typed FeaturePython)
  n = 1
  ref = As_element
FEATURE [App::DocumentObjectGroupPython] G4_GALLIUM_ARSENIDE  # scripted group (container) (typed FeaturePython)
  Dunit = g/cm3
  Dvalue = 5.31
  Group = -> [Ga_element001,As_element001]
  conduct = 2
  density = 1
  expand = 3
  formula = G4_GALLIUM_ARSENIDE
  name = G4_GALLIUM_ARSENIDE
  specific = 4
FEATURE [App::DocumentObjectGroupPython] H_element041  label="H_element : 0.081"  # scripted group (container) (typed FeaturePython)
  n = 0.08118
FEATURE [App::DocumentObjectGroupPython] C_element048  label="C_element : 0.416"  # scripted group (container) (typed FeaturePython)
  n = 0.41606
FEATURE [App::DocumentObjectGroupPython] N_element018  label="N_element : 0.111"  # scripted group (container) (typed FeaturePython)
  n = 0.11124
FEATURE [App::DocumentObjectGroupPython] O_element042  label="O_element : 0.381"  # scripted group (container) (typed FeaturePython)
  n = 0.38064
FEATURE [App::DocumentObjectGroupPython] S_element013  label="S_element : 0.011"  # scripted group (container) (typed FeaturePython)
  n = 0.01088
FEATURE [App::DocumentObjectGroupPython] G4_GEL_PHOTO_EMULSION  # scripted group (container) (typed FeaturePython)
  Dunit = g/cm3
  Dvalue = 1.2914
  Group = -> [H_element041,C_element048,N_element018,O_element042,S_element013]
  conduct = 2
  density = 1
  expand = 3
  formula = G4_GEL_PHOTO_EMULSION
  name = G4_GEL_PHOTO_EMULSION
  specific = 4
FEATURE [App::DocumentObjectGroupPython] B_element004  label="B_element : 0.040"  # scripted group (container) (typed FeaturePython)
  n = 0.0400639
FEATURE [App::DocumentObjectGroupPython] O_element043  label="O_element : 0.540"  # scripted group (container) (typed FeaturePython)
  n = 0.539561
FEATURE [App::DocumentObjectGroupPython] Na_element008  label="Na_element : 0.028"  # scripted group (container) (typed FeaturePython)
  n = 0.0281909
FEATURE [App::DocumentObjectGroupPython] Al_element003  label="Al_element : 0.012"  # scripted group (container) (typed FeaturePython)
  n = 0.011644
FEATURE [App::DocumentObjectGroupPython] Si_element003  label="Si_element : 0.377"  # scripted group (container) (typed FeaturePython)
  n = 0.377219
FEATURE [App::DocumentObjectGroupPython] K_element004  label="K_element : 0.014"  # scripted group (container) (typed FeaturePython)
  n = 0.00332099
FEATURE [App::DocumentObjectGroupPython] G4_Pyrex_Glass  # scripted group (container) (typed FeaturePython)
  Dunit = g/cm3
  Dvalue = 2.23
  Group = -> [B_element004,O_element043,Na_element008,Al_element003,Si_element003,K_element004]
  conduct = 2
  density = 1
  expand = 3
  formula = G4_Pyrex_Glass
  name = G4_Pyrex_Glass
  specific = 4
FEATURE [App::DocumentObjectGroupPython] O_element044  label="O_element : 0.156"  # scripted group (container) (typed FeaturePython)
  n = 0.156453
FEATURE [App::DocumentObjectGroupPython] Si_element004  label="Si_element : 0.081"  # scripted group (container) (typed FeaturePython)
  n = 0.080866
FEATURE [App::DocumentObjectGroupPython] Ti_element001  label="Ti_element : 0.008"  # scripted group (container) (typed FeaturePython)
  n = 0.008092
FEATURE [App::DocumentObjectGroupPython] As_element002  label="As_element : 0.003"  # scripted group (container) (typed FeaturePython)
  n = 0.002651
FEATURE [App::DocumentObjectGroupPython] Pb_element001  label="Pb_element : 0.752"  # scripted group (container) (typed FeaturePython)
  n = 0.751938
FEATURE [App::DocumentObjectGroupPython] G4_GLASS_LEAD  # scripted group (container) (typed FeaturePython)
  Dunit = g/cm3
  Dvalue = 6.22
  Group = -> [O_element044,Si_element004,Ti_element001,As_element002,Pb_element001]
  conduct = 2
  density = 1
  expand = 3
  formula = G4_GLASS_LEAD
  name = G4_GLASS_LEAD
  specific = 4
FEATURE [App::DocumentObjectGroupPython] O_element045  label="O_element : 0.460"  # scripted group (container) (typed FeaturePython)
  n = 0.4598
FEATURE [App::DocumentObjectGroupPython] Na_element009  label="Na_element : 0.096"  # scripted group (container) (typed FeaturePython)
  n = 0.0964411
FEATURE [App::DocumentObjectGroupPython] Si_element005  label="Si_element : 0.378"  # scripted group (container) (typed FeaturePython)
  n = 0.336553
FEATURE [App::DocumentObjectGroupPython] Ca_element011  label="Ca_element : 0.107"  # scripted group (container) (typed FeaturePython)
  n = 0.107205
FEATURE [App::DocumentObjectGroupPython] G4_GLASS_PLATE  # scripted group (container) (typed FeaturePython)
  Dunit = g/cm3
  Dvalue = 2.4
  Group = -> [O_element045,Na_element009,Si_element005,Ca_element011]
  conduct = 2
  density = 1
  expand = 3
  formula = G4_GLASS_PLATE
  name = G4_GLASS_PLATE
  specific = 4
FEATURE [App::DocumentObjectGroupPython] C_element049  label="C_element : 026"  # scripted group (container) (typed FeaturePython)
  n = 5
  ref = C_element
FEATURE [App::DocumentObjectGroupPython] H_element042  label="H_element : 021"  # scripted group (container) (typed FeaturePython)
  n = 10
  ref = H_element
FEATURE [App::DocumentObjectGroupPython] N_element019  label="N_element : 2"  # scripted group (container) (typed FeaturePython)
  n = 2
  ref = N_element
FEATURE [App::DocumentObjectGroupPython] O_element046  label="O_element : 022"  # scripted group (container) (typed FeaturePython)
  n = 3
  ref = O_element
FEATURE [App::DocumentObjectGroupPython] G4_GLUTAMINE  # scripted group (container) (typed FeaturePython)
  Dunit = g/cm3
  Dvalue = 1.46
  Group = -> [C_element049,H_element042,N_element019,O_element046]
  conduct = 2
  density = 1
  expand = 3
  formula = G4_GLUTAMINE
  name = G4_GLUTAMINE
  specific = 4
FEATURE [App::DocumentObjectGroupPython] C_element050  label="C_element : 027"  # scripted group (container) (typed FeaturePython)
  n = 3
  ref = C_element
FEATURE [App::DocumentObjectGroupPython] H_element043  label="H_element : 022"  # scripted group (container) (typed FeaturePython)
  n = 8
  ref = H_element
FEATURE [App::DocumentObjectGroupPython] O_element047  label="O_element : 023"  # scripted group (container) (typed FeaturePython)
  n = 3
  ref = O_element
FEATURE [App::DocumentObjectGroupPython] G4_GLYCEROL  # scripted group (container) (typed FeaturePython)
  Dunit = g/cm3
  Dvalue = 1.2613
  Group = -> [C_element050,H_element043,O_element047]
  conduct = 2
  density = 1
  expand = 3
  formula = G4_GLYCEROL
  name = G4_GLYCEROL
  specific = 4
FEATURE [App::DocumentObjectGroupPython] C_element051  label="C_element : 028"  # scripted group (container) (typed FeaturePython)
  n = 5
  ref = C_element
FEATURE [App::DocumentObjectGroupPython] H_element044  label="H_element : 023"  # scripted group (container) (typed FeaturePython)
  n = 5
  ref = H_element
FEATURE [App::DocumentObjectGroupPython] N_element020  label="N_element : 009"  # scripted group (container) (typed FeaturePython)
  n = 5
  ref = N_element
FEATURE [App::DocumentObjectGroupPython] O_element048  label="O_element : 024"  # scripted group (container) (typed FeaturePython)
  n = 1
  ref = O_element
FEATURE [App::DocumentObjectGroupPython] G4_GUANINE  # scripted group (container) (typed FeaturePython)
  Dunit = g/cm3
  Dvalue = 2.2
  Group = -> [C_element051,H_element044,N_element020,O_element048]
  conduct = 2
  density = 1
  expand = 3
  formula = G4_GUANINE
  name = G4_GUANINE
  specific = 4
FEATURE [App::DocumentObjectGroupPython] Ca_element012  label="Ca_element : 006"  # scripted group (container) (typed FeaturePython)
  n = 1
  ref = Ca_element
FEATURE [App::DocumentObjectGroupPython] S_element014  label="S_element : 005"  # scripted group (container) (typed FeaturePython)
  n = 1
  ref = S_element
FEATURE [App::DocumentObjectGroupPython] O_element049  label="O_element : 6"  # scripted group (container) (typed FeaturePython)
  n = 6
  ref = O_element
FEATURE [App::DocumentObjectGroupPython] H_element045  label="H_element : 024"  # scripted group (container) (typed FeaturePython)
  n = 4
  ref = H_element
FEATURE [App::DocumentObjectGroupPython] G4_GYPSUM  # scripted group (container) (typed FeaturePython)
  Dunit = g/cm3
  Dvalue = 2.32
  Group = -> [Ca_element012,S_element014,O_element049,H_element045]
  conduct = 2
  density = 1
  expand = 3
  formula = G4_GYPSUM
  name = G4_GYPSUM
  specific = 4
FEATURE [App::DocumentObjectGroupPython] C_element052  label="C_element : 7"  # scripted group (container) (typed FeaturePython)
  n = 7
  ref = C_element
FEATURE [App::DocumentObjectGroupPython] H_element046  label="H_element : 16"  # scripted group (container) (typed FeaturePython)
  n = 16
  ref = H_element
FEATURE [App::DocumentObjectGroupPython] G4_N_HEPTANE  label="G4_N-HEPTANE"  # scripted group (container) (typed FeaturePython)
  Dunit = g/cm3
  Dvalue = 0.68376
  Group = -> [C_element052,H_element046]
  conduct = 2
  density = 1
  expand = 3
  formula = G4_N-HEPTANE
  name = G4_N-HEPTANE
  specific = 4
FEATURE [App::DocumentObjectGroupPython] C_element053  label="C_element : 029"  # scripted group (container) (typed FeaturePython)
  n = 6
  ref = C_element
FEATURE [App::DocumentObjectGroupPython] H_element047  label="H_element : 14"  # scripted group (container) (typed FeaturePython)
  n = 14
  ref = H_element
FEATURE [App::DocumentObjectGroupPython] G4_N_HEXANE  label="G4_N-HEXANE"  # scripted group (container) (typed FeaturePython)
  Dunit = g/cm3
  Dvalue = 0.6603
  Group = -> [C_element053,H_element047]
  conduct = 2
  density = 1
  expand = 3
  formula = G4_N-HEXANE
  name = G4_N-HEXANE
  specific = 4
FEATURE [App::DocumentObjectGroupPython] C_element054  label="C_element : 22"  # scripted group (container) (typed FeaturePython)
  n = 22
  ref = C_element
FEATURE [App::DocumentObjectGroupPython] H_element048  label="H_element : 025"  # scripted group (container) (typed FeaturePython)
  n = 10
  ref = H_element
FEATURE [App::DocumentObjectGroupPython] N_element021  label="N_element : 010"  # scripted group (container) (typed FeaturePython)
  n = 2
  ref = N_element
FEATURE [App::DocumentObjectGroupPython] O_element050  label="O_element : 025"  # scripted group (container) (typed FeaturePython)
  n = 5
  ref = O_element
FEATURE [App::DocumentObjectGroupPython] G4_KAPTON  # scripted group (container) (typed FeaturePython)
  Dunit = g/cm3
  Dvalue = 1.42
  Group = -> [C_element054,H_element048,N_element021,O_element050]
  conduct = 2
  density = 1
  expand = 3
  formula = G4_KAPTON
  name = G4_KAPTON
  specific = 4
FEATURE [App::DocumentObjectGroupPython] La_element001  label="La_element : 1"  # scripted group (container) (typed FeaturePython)
  n = 1
  ref = La_element
FEATURE [App::DocumentObjectGroupPython] Br_element003  label="Br_element : 002"  # scripted group (container) (typed FeaturePython)
  n = 1
  ref = Br_element
FEATURE [App::DocumentObjectGroupPython] O_element051  label="O_element : 026"  # scripted group (container) (typed FeaturePython)
  n = 1
  ref = O_element
FEATURE [App::DocumentObjectGroupPython] G4_LANTHANUM_OXYBROMIDE  # scripted group (container) (typed FeaturePython)
  Dunit = g/cm3
  Dvalue = 6.28
  Group = -> [La_element001,Br_element003,O_element051]
  conduct = 2
  density = 1
  expand = 3
  formula = G4_LANTHANUM_OXYBROMIDE
  name = G4_LANTHANUM_OXYBROMIDE
  specific = 4
FEATURE [App::DocumentObjectGroupPython] La_element002  label="La_element : 2"  # scripted group (container) (typed FeaturePython)
  n = 2
  ref = La_element
FEATURE [App::DocumentObjectGroupPython] O_element052  label="O_element : 027"  # scripted group (container) (typed FeaturePython)
  n = 2
  ref = O_element
FEATURE [App::DocumentObjectGroupPython] S_element015  label="S_element : 006"  # scripted group (container) (typed FeaturePython)
  n = 1
  ref = S_element
FEATURE [App::DocumentObjectGroupPython] G4_LANTHANUM_OXYSULFIDE  # scripted group (container) (typed FeaturePython)
  Dunit = g/cm3
  Dvalue = 5.86
  Group = -> [La_element002,O_element052,S_element015]
  conduct = 2
  density = 1
  expand = 3
  formula = G4_LANTHANUM_OXYSULFIDE
  name = G4_LANTHANUM_OXYSULFIDE
  specific = 4
FEATURE [App::DocumentObjectGroupPython] O_element053  label="O_element : 0.072"  # scripted group (container) (typed FeaturePython)
  n = 0.071682
FEATURE [App::DocumentObjectGroupPython] Pb_element002  label="Pb_element : 0.928"  # scripted group (container) (typed FeaturePython)
  n = 0.928318
FEATURE [App::DocumentObjectGroupPython] G4_LEAD_OXIDE  # scripted group (container) (typed FeaturePython)
  Dunit = g/cm3
  Dvalue = 9.53
  Group = -> [O_element053,Pb_element002]
  conduct = 2
  density = 1
  expand = 3
  formula = G4_LEAD_OXIDE
  name = G4_LEAD_OXIDE
  specific = 4
FEATURE [App::DocumentObjectGroupPython] Li_element001  label="Li_element : 1"  # scripted group (container) (typed FeaturePython)
  n = 1
  ref = Li_element
FEATURE [App::DocumentObjectGroupPython] N_element022  label="N_element : 011"  # scripted group (container) (typed FeaturePython)
  n = 1
  ref = N_element
FEATURE [App::DocumentObjectGroupPython] H_element049  label="H_element : 026"  # scripted group (container) (typed FeaturePython)
  n = 2
  ref = H_element
FEATURE [App::DocumentObjectGroupPython] G4_LITHIUM_AMIDE  # scripted group (container) (typed FeaturePython)
  Dunit = g/cm3
  Dvalue = 1.178
  Group = -> [Li_element001,N_element022,H_element049]
  conduct = 2
  density = 1
  expand = 3
  formula = G4_LITHIUM_AMIDE
  name = G4_LITHIUM_AMIDE
  specific = 4
FEATURE [App::DocumentObjectGroupPython] Li_element002  label="Li_element : 2"  # scripted group (container) (typed FeaturePython)
  n = 2
  ref = Li_element
FEATURE [App::DocumentObjectGroupPython] C_element055  label="C_element : 030"  # scripted group (container) (typed FeaturePython)
  n = 1
  ref = C_element
FEATURE [App::DocumentObjectGroupPython] O_element054  label="O_element : 028"  # scripted group (container) (typed FeaturePython)
  n = 3
  ref = O_element
FEATURE [App::DocumentObjectGroupPython] G4_LITHIUM_CARBONATE  # scripted group (container) (typed FeaturePython)
  Dunit = g/cm3
  Dvalue = 2.11
  Group = -> [Li_element002,C_element055,O_element054]
  conduct = 2
  density = 1
  expand = 3
  formula = G4_LITHIUM_CARBONATE
  name = G4_LITHIUM_CARBONATE
  specific = 4
FEATURE [App::DocumentObjectGroupPython] Li_element003  label="Li_element : 003"  # scripted group (container) (typed FeaturePython)
  n = 1
  ref = Li_element
FEATURE [App::DocumentObjectGroupPython] F_element012  label="F_element : 004"  # scripted group (container) (typed FeaturePython)
  n = 1
  ref = F_element
FEATURE [App::DocumentObjectGroupPython] G4_LITHIUM_FLUORIDE  # scripted group (container) (typed FeaturePython)
  Dunit = g/cm3
  Dvalue = 2.635
  Group = -> [Li_element003,F_element012]
  conduct = 2
  density = 1
  expand = 3
  formula = G4_LITHIUM_FLUORIDE
  name = G4_LITHIUM_FLUORIDE
  specific = 4
FEATURE [App::DocumentObjectGroupPython] Li_element004  label="Li_element : 004"  # scripted group (container) (typed FeaturePython)
  n = 1
  ref = Li_element
FEATURE [App::DocumentObjectGroupPython] H_element050  label="H_element : 027"  # scripted group (container) (typed FeaturePython)
  n = 1
  ref = H_element
FEATURE [App::DocumentObjectGroupPython] G4_LITHIUM_HYDRIDE  # scripted group (container) (typed FeaturePython)
  Dunit = g/cm3
  Dvalue = 0.82
  Group = -> [Li_element004,H_element050]
  conduct = 2
  density = 1
  expand = 3
  formula = G4_LITHIUM_HYDRIDE
  name = G4_LITHIUM_HYDRIDE
  specific = 4
FEATURE [App::DocumentObjectGroupPython] Li_element005  label="Li_element : 005"  # scripted group (container) (typed FeaturePython)
  n = 1
  ref = Li_element
FEATURE [App::DocumentObjectGroupPython] I_element003  label="I_element : 002"  # scripted group (container) (typed FeaturePython)
  n = 1
  ref = I_element
FEATURE [App::DocumentObjectGroupPython] G4_LITHIUM_IODIDE  # scripted group (container) (typed FeaturePython)
  Dunit = g/cm3
  Dvalue = 3.494
  Group = -> [Li_element005,I_element003]
  conduct = 2
  density = 1
  expand = 3
  formula = G4_LITHIUM_IODIDE
  name = G4_LITHIUM_IODIDE
  specific = 4
FEATURE [App::DocumentObjectGroupPython] Li_element006  label="Li_element : 006"  # scripted group (container) (typed FeaturePython)
  n = 2
  ref = Li_element
FEATURE [App::DocumentObjectGroupPython] O_element055  label="O_element : 029"  # scripted group (container) (typed FeaturePython)
  n = 1
  ref = O_element
FEATURE [App::DocumentObjectGroupPython] G4_LITHIUM_OXIDE  # scripted group (container) (typed FeaturePython)
  Dunit = g/cm3
  Dvalue = 2.013
  Group = -> [Li_element006,O_element055]
  conduct = 2
  density = 1
  expand = 3
  formula = G4_LITHIUM_OXIDE
  name = G4_LITHIUM_OXIDE
  specific = 4
FEATURE [App::DocumentObjectGroupPython] Li_element007  label="Li_element : 007"  # scripted group (container) (typed FeaturePython)
  n = 2
  ref = Li_element
FEATURE [App::DocumentObjectGroupPython] B_element005  label="B_element : 005"  # scripted group (container) (typed FeaturePython)
  n = 4
  ref = B_element
FEATURE [App::DocumentObjectGroupPython] O_element056  label="O_element : 7"  # scripted group (container) (typed FeaturePython)
  n = 7
  ref = O_element
FEATURE [App::DocumentObjectGroupPython] G4_LITHIUM_TETRABORATE  # scripted group (container) (typed FeaturePython)
  Dunit = g/cm3
  Dvalue = 2.44
  Group = -> [Li_element007,B_element005,O_element056]
  conduct = 2
  density = 1
  expand = 3
  formula = G4_LITHIUM_TETRABORATE
  name = G4_LITHIUM_TETRABORATE
  specific = 4
FEATURE [App::DocumentObjectGroupPython] H_element051  label="H_element : 0.105"  # scripted group (container) (typed FeaturePython)
  n = 0.105
FEATURE [App::DocumentObjectGroupPython] C_element056  label="C_element : 0.083"  # scripted group (container) (typed FeaturePython)
  n = 0.083
FEATURE [App::DocumentObjectGroupPython] N_element023  label="N_element : 0.023"  # scripted group (container) (typed FeaturePython)
  n = 0.023
FEATURE [App::DocumentObjectGroupPython] O_element057  label="O_element : 0.779"  # scripted group (container) (typed FeaturePython)
  n = 0.779
FEATURE [App::DocumentObjectGroupPython] Na_element010  label="Na_element : 0.097"  # scripted group (container) (typed FeaturePython)
  n = 0.002
FEATURE [App::DocumentObjectGroupPython] P_element006  label="P_element : 0.105"  # scripted group (container) (typed FeaturePython)
  n = 0.001
FEATURE [App::DocumentObjectGroupPython] S_element016  label="S_element : 0.017"  # scripted group (container) (typed FeaturePython)
  n = 0.002
FEATURE [App::DocumentObjectGroupPython] Cl_element014  label="Cl_element : 0.587"  # scripted group (container) (typed FeaturePython)
  n = 0.003
FEATURE [App::DocumentObjectGroupPython] K_element005  label="K_element : 0.015"  # scripted group (container) (typed FeaturePython)
  n = 0.002
FEATURE [App::DocumentObjectGroupPython] G4_LUNG_ICRP  # scripted group (container) (typed FeaturePython)
  Dunit = g/cm3
  Dvalue = 1.04
  Group = -> [H_element051,C_element056,N_element023,O_element057,Na_element010,P_element006,S_element016,Cl_element014,K_element005]
  conduct = 2
  density = 1
  expand = 3
  formula = G4_LUNG_ICRP
  name = G4_LUNG_ICRP
  specific = 4
FEATURE [App::DocumentObjectGroupPython] H_element052  label="H_element : 0.116"  # scripted group (container) (typed FeaturePython)
  n = 0.114318
FEATURE [App::DocumentObjectGroupPython] C_element057  label="C_element : 0.656"  # scripted group (container) (typed FeaturePython)
  n = 0.655824
FEATURE [App::DocumentObjectGroupPython] O_element058  label="O_element : 0.092"  # scripted group (container) (typed FeaturePython)
  n = 0.0921831
FEATURE [App::DocumentObjectGroupPython] Mg_element004  label="Mg_element : 0.135"  # scripted group (container) (typed FeaturePython)
  n = 0.134792
FEATURE [App::DocumentObjectGroupPython] Ca_element013  label="Ca_element : 0.003"  # scripted group (container) (typed FeaturePython)
  n = 0.002883
FEATURE [App::DocumentObjectGroupPython] G4_M3_WAX  # scripted group (container) (typed FeaturePython)
  Dunit = g/cm3
  Dvalue = 1.05
  Group = -> [H_element052,C_element057,O_element058,Mg_element004,Ca_element013]
  conduct = 2
  density = 1
  expand = 3
  formula = G4_M3_WAX
  name = G4_M3_WAX
  specific = 4
FEATURE [App::DocumentObjectGroupPython] Mg_element005  label="Mg_element : 1"  # scripted group (container) (typed FeaturePython)
  n = 1
  ref = Mg_element
FEATURE [App::DocumentObjectGroupPython] C_element058  label="C_element : 031"  # scripted group (container) (typed FeaturePython)
  n = 1
  ref = C_element
FEATURE [App::DocumentObjectGroupPython] O_element059  label="O_element : 030"  # scripted group (container) (typed FeaturePython)
  n = 3
  ref = O_element
FEATURE [App::DocumentObjectGroupPython] G4_MAGNESIUM_CARBONATE  # scripted group (container) (typed FeaturePython)
  Dunit = g/cm3
  Dvalue = 2.958
  Group = -> [Mg_element005,C_element058,O_element059]
  conduct = 2
  density = 1
  expand = 3
  formula = G4_MAGNESIUM_CARBONATE
  name = G4_MAGNESIUM_CARBONATE
  specific = 4
FEATURE [App::DocumentObjectGroupPython] Mg_element006  label="Mg_element : 002"  # scripted group (container) (typed FeaturePython)
  n = 1
  ref = Mg_element
FEATURE [App::DocumentObjectGroupPython] F_element013  label="F_element : 005"  # scripted group (container) (typed FeaturePython)
  n = 2
  ref = F_element
FEATURE [App::DocumentObjectGroupPython] G4_MAGNESIUM_FLUORIDE  # scripted group (container) (typed FeaturePython)
  Dunit = g/cm3
  Dvalue = 3
  Group = -> [Mg_element006,F_element013]
  conduct = 2
  density = 1
  expand = 3
  formula = G4_MAGNESIUM_FLUORIDE
  name = G4_MAGNESIUM_FLUORIDE
  specific = 4
FEATURE [App::DocumentObjectGroupPython] Mg_element007  label="Mg_element : 003"  # scripted group (container) (typed FeaturePython)
  n = 1
  ref = Mg_element
FEATURE [App::DocumentObjectGroupPython] O_element060  label="O_element : 031"  # scripted group (container) (typed FeaturePython)
  n = 1
  ref = O_element
FEATURE [App::DocumentObjectGroupPython] G4_MAGNESIUM_OXIDE  # scripted group (container) (typed FeaturePython)
  Dunit = g/cm3
  Dvalue = 3.58
  Group = -> [Mg_element007,O_element060]
  conduct = 2
  density = 1
  expand = 3
  formula = G4_MAGNESIUM_OXIDE
  name = G4_MAGNESIUM_OXIDE
  specific = 4
FEATURE [App::DocumentObjectGroupPython] Mg_element008  label="Mg_element : 004"  # scripted group (container) (typed FeaturePython)
  n = 1
  ref = Mg_element
FEATURE [App::DocumentObjectGroupPython] B_element006  label="B_element : 006"  # scripted group (container) (typed FeaturePython)
  n = 4
  ref = B_element
FEATURE [App::DocumentObjectGroupPython] O_element061  label="O_element : 032"  # scripted group (container) (typed FeaturePython)
  n = 7
  ref = O_element
FEATURE [App::DocumentObjectGroupPython] G4_MAGNESIUM_TETRABORATE  # scripted group (container) (typed FeaturePython)
  Dunit = g/cm3
  Dvalue = 2.53
  Group = -> [Mg_element008,B_element006,O_element061]
  conduct = 2
  density = 1
  expand = 3
  formula = G4_MAGNESIUM_TETRABORATE
  name = G4_MAGNESIUM_TETRABORATE
  specific = 4
FEATURE [App::DocumentObjectGroupPython] Hg_element001  label="Hg_element : 1"  # scripted group (container) (typed FeaturePython)
  n = 1
  ref = Hg_element
FEATURE [App::DocumentObjectGroupPython] I_element004  label="I_element : 2"  # scripted group (container) (typed FeaturePython)
  n = 2
  ref = I_element
FEATURE [App::DocumentObjectGroupPython] G4_MERCURIC_IODIDE  # scripted group (container) (typed FeaturePython)
  Dunit = g/cm3
  Dvalue = 6.36
  Group = -> [Hg_element001,I_element004]
  conduct = 2
  density = 1
  expand = 3
  formula = G4_MERCURIC_IODIDE
  name = G4_MERCURIC_IODIDE
  specific = 4
FEATURE [App::DocumentObjectGroupPython] C_element059  label="C_element : 032"  # scripted group (container) (typed FeaturePython)
  n = 1
  ref = C_element
FEATURE [App::DocumentObjectGroupPython] H_element053  label="H_element : 028"  # scripted group (container) (typed FeaturePython)
  n = 4
  ref = H_element
FEATURE [App::DocumentObjectGroupPython] G4_METHANE  # scripted group (container) (typed FeaturePython)
  Dunit = g/cm3
  Dvalue = 0.000667151
  Group = -> [C_element059,H_element053]
  conduct = 2
  density = 1
  expand = 3
  formula = G4_METHANE
  name = G4_METHANE
  specific = 4
FEATURE [App::DocumentObjectGroupPython] C_element060  label="C_element : 033"  # scripted group (container) (typed FeaturePython)
  n = 1
  ref = C_element
FEATURE [App::DocumentObjectGroupPython] H_element054  label="H_element : 029"  # scripted group (container) (typed FeaturePython)
  n = 4
  ref = H_element
FEATURE [App::DocumentObjectGroupPython] O_element062  label="O_element : 033"  # scripted group (container) (typed FeaturePython)
  n = 1
  ref = O_element
FEATURE [App::DocumentObjectGroupPython] G4_METHANOL  # scripted group (container) (typed FeaturePython)
  Dunit = g/cm3
  Dvalue = 0.7914
  Group = -> [C_element060,H_element054,O_element062]
  conduct = 2
  density = 1
  expand = 3
  formula = G4_METHANOL
  name = G4_METHANOL
  specific = 4
FEATURE [App::DocumentObjectGroupPython] H_element055  label="H_element : 0.134"  # scripted group (container) (typed FeaturePython)
  n = 0.13404
FEATURE [App::DocumentObjectGroupPython] C_element061  label="C_element : 0.778"  # scripted group (container) (typed FeaturePython)
  n = 0.77796
FEATURE [App::DocumentObjectGroupPython] O_element063  label="O_element : 0.035"  # scripted group (container) (typed FeaturePython)
  n = 0.03502
FEATURE [App::DocumentObjectGroupPython] Mg_element009  label="Mg_element : 0.039"  # scripted group (container) (typed FeaturePython)
  n = 0.038594
FEATURE [App::DocumentObjectGroupPython] Ti_element002  label="Ti_element : 0.014"  # scripted group (container) (typed FeaturePython)
  n = 0.014386
FEATURE [App::DocumentObjectGroupPython] G4_MIX_D_WAX  # scripted group (container) (typed FeaturePython)
  Dunit = g/cm3
  Dvalue = 0.99
  Group = -> [H_element055,C_element061,O_element063,Mg_element009,Ti_element002]
  conduct = 2
  density = 1
  expand = 3
  formula = G4_MIX_D_WAX
  name = G4_MIX_D_WAX
  specific = 4
FEATURE [App::DocumentObjectGroupPython] H_element056  label="H_element : 0.135"  # scripted group (container) (typed FeaturePython)
  n = 0.081192
FEATURE [App::DocumentObjectGroupPython] C_element062  label="C_element : 0.583"  # scripted group (container) (typed FeaturePython)
  n = 0.583442
FEATURE [App::DocumentObjectGroupPython] N_element024  label="N_element : 0.018"  # scripted group (container) (typed FeaturePython)
  n = 0.017798
FEATURE [App::DocumentObjectGroupPython] O_element064  label="O_element : 0.186"  # scripted group (container) (typed FeaturePython)
  n = 0.186381
FEATURE [App::DocumentObjectGroupPython] Mg_element010  label="Mg_element : 0.130"  # scripted group (container) (typed FeaturePython)
  n = 0.130287
FEATURE [App::DocumentObjectGroupPython] Cl_element015  label="Cl_element : 0.588"  # scripted group (container) (typed FeaturePython)
  n = 0.0009
FEATURE [App::DocumentObjectGroupPython] G4_MS20_TISSUE  # scripted group (container) (typed FeaturePython)
  Dunit = g/cm3
  Dvalue = 1
  Group = -> [H_element056,C_element062,N_element024,O_element064,Mg_element010,Cl_element015]
  conduct = 2
  density = 1
  expand = 3
  formula = G4_MS20_TISSUE
  name = G4_MS20_TISSUE
  specific = 4
FEATURE [App::DocumentObjectGroupPython] H_element057  label="H_element : 0.136"  # scripted group (container) (typed FeaturePython)
  n = 0.102
FEATURE [App::DocumentObjectGroupPython] C_element063  label="C_element : 0.143"  # scripted group (container) (typed FeaturePython)
  n = 0.143
FEATURE [App::DocumentObjectGroupPython] N_element025  label="N_element : 0.034"  # scripted group (container) (typed FeaturePython)
  n = 0.034
FEATURE [App::DocumentObjectGroupPython] O_element065  label="O_element : 0.710"  # scripted group (container) (typed FeaturePython)
  n = 0.71
FEATURE [App::DocumentObjectGroupPython] Na_element011  label="Na_element : 0.098"  # scripted group (container) (typed FeaturePython)
  n = 0.001
FEATURE [App::DocumentObjectGroupPython] P_element007  label="P_element : 0.002"  # scripted group (container) (typed FeaturePython)
  n = 0.002
FEATURE [App::DocumentObjectGroupPython] S_element017  label="S_element : 0.018"  # scripted group (container) (typed FeaturePython)
  n = 0.003
FEATURE [App::DocumentObjectGroupPython] Cl_element016  label="Cl_element : 0.589"  # scripted group (container) (typed FeaturePython)
  n = 0.001
FEATURE [App::DocumentObjectGroupPython] K_element006  label="K_element : 0.004"  # scripted group (container) (typed FeaturePython)
  n = 0.004
FEATURE [App::DocumentObjectGroupPython] G4_MUSCLE_SKELETAL_ICRP  # scripted group (container) (typed FeaturePython)
  Dunit = g/cm3
  Dvalue = 1.05
  Group = -> [H_element057,C_element063,N_element025,O_element065,Na_element011,P_element007,S_element017,Cl_element016,K_element006]
  conduct = 2
  density = 1
  expand = 3
  formula = G4_MUSCLE_SKELETAL_ICRP
  name = G4_MUSCLE_SKELETAL_ICRP
  specific = 4
FEATURE [App::DocumentObjectGroupPython] H_element058  label="H_element : 0.137"  # scripted group (container) (typed FeaturePython)
  n = 0.102102
FEATURE [App::DocumentObjectGroupPython] C_element064  label="C_element : 0.123"  # scripted group (container) (typed FeaturePython)
  n = 0.123123
FEATURE [App::DocumentObjectGroupPython] N_element026  label="N_element : 0.756"  # scripted group (container) (typed FeaturePython)
  n = 0.035035
FEATURE [App::DocumentObjectGroupPython] O_element066  label="O_element : 0.730"  # scripted group (container) (typed FeaturePython)
  n = 0.72973
FEATURE [App::DocumentObjectGroupPython] Na_element012  label="Na_element : 0.099"  # scripted group (container) (typed FeaturePython)
  n = 0.001001
FEATURE [App::DocumentObjectGroupPython] P_element008  label="P_element : 0.106"  # scripted group (container) (typed FeaturePython)
  n = 0.002002
FEATURE [App::DocumentObjectGroupPython] S_element018  label="S_element : 0.019"  # scripted group (container) (typed FeaturePython)
  n = 0.004004
FEATURE [App::DocumentObjectGroupPython] K_element007  label="K_element : 0.016"  # scripted group (container) (typed FeaturePython)
  n = 0.003003
FEATURE [App::DocumentObjectGroupPython] G4_MUSCLE_STRIATED_ICRU  # scripted group (container) (typed FeaturePython)
  Dunit = g/cm3
  Dvalue = 1.04
  Group = -> [H_element058,C_element064,N_element026,O_element066,Na_element012,P_element008,S_element018,K_element007]
  conduct = 2
  density = 1
  expand = 3
  formula = G4_MUSCLE_STRIATED_ICRU
  name = G4_MUSCLE_STRIATED_ICRU
  specific = 4
FEATURE [App::DocumentObjectGroupPython] H_element059  label="H_element : 0.098"  # scripted group (container) (typed FeaturePython)
  n = 0.0982341
FEATURE [App::DocumentObjectGroupPython] C_element065  label="C_element : 0.156"  # scripted group (container) (typed FeaturePython)
  n = 0.156214
FEATURE [App::DocumentObjectGroupPython] N_element027  label="N_element : 0.757"  # scripted group (container) (typed FeaturePython)
  n = 0.035451
FEATURE [App::DocumentObjectGroupPython] O_element067  label="O_element : 0.880"  # scripted group (container) (typed FeaturePython)
  n = 0.710101
FEATURE [App::DocumentObjectGroupPython] G4_MUSCLE_WITH_SUCROSE  # scripted group (container) (typed FeaturePython)
  Dunit = g/cm3
  Dvalue = 1.11
  Group = -> [H_element059,C_element065,N_element027,O_element067]
  conduct = 2
  density = 1
  expand = 3
  formula = G4_MUSCLE_WITH_SUCROSE
  name = G4_MUSCLE_WITH_SUCROSE
  specific = 4
FEATURE [App::DocumentObjectGroupPython] H_element060  label="H_element : 0.138"  # scripted group (container) (typed FeaturePython)
  n = 0.101969
FEATURE [App::DocumentObjectGroupPython] C_element066  label="C_element : 0.120"  # scripted group (container) (typed FeaturePython)
  n = 0.120058
FEATURE [App::DocumentObjectGroupPython] N_element028  label="N_element : 0.758"  # scripted group (container) (typed FeaturePython)
  n = 0.035451
FEATURE [App::DocumentObjectGroupPython] O_element068  label="O_element : 0.743"  # scripted group (container) (typed FeaturePython)
  n = 0.742522
FEATURE [App::DocumentObjectGroupPython] G4_MUSCLE_WITHOUT_SUCROSE  # scripted group (container) (typed FeaturePython)
  Dunit = g/cm3
  Dvalue = 1.07
  Group = -> [H_element060,C_element066,N_element028,O_element068]
  conduct = 2
  density = 1
  expand = 3
  formula = G4_MUSCLE_WITHOUT_SUCROSE
  name = G4_MUSCLE_WITHOUT_SUCROSE
  specific = 4
FEATURE [App::DocumentObjectGroupPython] C_element067  label="C_element : 10"  # scripted group (container) (typed FeaturePython)
  n = 10
  ref = C_element
FEATURE [App::DocumentObjectGroupPython] H_element061  label="H_element : 030"  # scripted group (container) (typed FeaturePython)
  n = 8
  ref = H_element
FEATURE [App::DocumentObjectGroupPython] G4_NAPHTHALENE  # scripted group (container) (typed FeaturePython)
  Dunit = g/cm3
  Dvalue = 1.145
  Group = -> [C_element067,H_element061]
  conduct = 2
  density = 1
  expand = 3
  formula = G4_NAPHTHALENE
  name = G4_NAPHTHALENE
  specific = 4
FEATURE [App::DocumentObjectGroupPython] C_element068  label="C_element : 034"  # scripted group (container) (typed FeaturePython)
  n = 6
  ref = C_element
FEATURE [App::DocumentObjectGroupPython] H_element062  label="H_element : 031"  # scripted group (container) (typed FeaturePython)
  n = 5
  ref = H_element
FEATURE [App::DocumentObjectGroupPython] N_element029  label="N_element : 012"  # scripted group (container) (typed FeaturePython)
  n = 1
  ref = N_element
FEATURE [App::DocumentObjectGroupPython] O_element069  label="O_element : 034"  # scripted group (container) (typed FeaturePython)
  n = 2
  ref = O_element
FEATURE [App::DocumentObjectGroupPython] G4_NITROBENZENE  # scripted group (container) (typed FeaturePython)
  Dunit = g/cm3
  Dvalue = 1.19867
  Group = -> [C_element068,H_element062,N_element029,O_element069]
  conduct = 2
  density = 1
  expand = 3
  formula = G4_NITROBENZENE
  name = G4_NITROBENZENE
  specific = 4
FEATURE [App::DocumentObjectGroupPython] N_element030  label="N_element : 013"  # scripted group (container) (typed FeaturePython)
  n = 2
  ref = N_element
FEATURE [App::DocumentObjectGroupPython] O_element070  label="O_element : 035"  # scripted group (container) (typed FeaturePython)
  n = 1
  ref = O_element
FEATURE [App::DocumentObjectGroupPython] G4_NITROUS_OXIDE  # scripted group (container) (typed FeaturePython)
  Dunit = g/cm3
  Dvalue = 0.00183094
  Group = -> [N_element030,O_element070]
  conduct = 2
  density = 1
  expand = 3
  formula = G4_NITROUS_OXIDE
  name = G4_NITROUS_OXIDE
  specific = 4
FEATURE [App::DocumentObjectGroupPython] H_element063  label="H_element : 0.104"  # scripted group (container) (typed FeaturePython)
  n = 0.103509
FEATURE [App::DocumentObjectGroupPython] C_element069  label="C_element : 0.648"  # scripted group (container) (typed FeaturePython)
  n = 0.648416
FEATURE [App::DocumentObjectGroupPython] N_element031  label="N_element : 0.100"  # scripted group (container) (typed FeaturePython)
  n = 0.0995361
FEATURE [App::DocumentObjectGroupPython] O_element071  label="O_element : 0.149"  # scripted group (container) (typed FeaturePython)
  n = 0.148539
FEATURE [App::DocumentObjectGroupPython] G4_NYLON_8062  label="G4_NYLON-8062"  # scripted group (container) (typed FeaturePython)
  Dunit = g/cm3
  Dvalue = 1.08
  Group = -> [H_element063,C_element069,N_element031,O_element071]
  conduct = 2
  density = 1
  expand = 3
  formula = G4_NYLON-8062
  name = G4_NYLON-8062
  specific = 4
FEATURE [App::DocumentObjectGroupPython] C_element070  label="C_element : 035"  # scripted group (container) (typed FeaturePython)
  n = 6
  ref = C_element
FEATURE [App::DocumentObjectGroupPython] H_element064  label="H_element : 11"  # scripted group (container) (typed FeaturePython)
  n = 11
  ref = H_element
FEATURE [App::DocumentObjectGroupPython] N_element032  label="N_element : 014"  # scripted group (container) (typed FeaturePython)
  n = 1
  ref = N_element
FEATURE [App::DocumentObjectGroupPython] O_element072  label="O_element : 036"  # scripted group (container) (typed FeaturePython)
  n = 1
  ref = O_element
FEATURE [App::DocumentObjectGroupPython] G4_NYLON_6_6  label="G4_NYLON-6-6"  # scripted group (container) (typed FeaturePython)
  Dunit = g/cm3
  Dvalue = 1.14
  Group = -> [C_element070,H_element064,N_element032,O_element072]
  conduct = 2
  density = 1
  expand = 3
  formula = G4_NYLON-6-6
  name = G4_NYLON-6-6
  specific = 4
FEATURE [App::DocumentObjectGroupPython] H_element065  label="H_element : 0.139"  # scripted group (container) (typed FeaturePython)
  n = 0.107062
FEATURE [App::DocumentObjectGroupPython] C_element071  label="C_element : 0.680"  # scripted group (container) (typed FeaturePython)
  n = 0.680449
FEATURE [App::DocumentObjectGroupPython] N_element033  label="N_element : 0.099"  # scripted group (container) (typed FeaturePython)
  n = 0.099189
FEATURE [App::DocumentObjectGroupPython] O_element073  label="O_element : 0.113"  # scripted group (container) (typed FeaturePython)
  n = 0.1133
FEATURE [App::DocumentObjectGroupPython] G4_NYLON_6_10  label="G4_NYLON-6-10"  # scripted group (container) (typed FeaturePython)
  Dunit = g/cm3
  Dvalue = 1.14
  Group = -> [H_element065,C_element071,N_element033,O_element073]
  conduct = 2
  density = 1
  expand = 3
  formula = G4_NYLON-6-10
  name = G4_NYLON-6-10
  specific = 4
FEATURE [App::DocumentObjectGroupPython] H_element066  label="H_element : 0.140"  # scripted group (container) (typed FeaturePython)
  n = 0.115476
FEATURE [App::DocumentObjectGroupPython] C_element072  label="C_element : 0.721"  # scripted group (container) (typed FeaturePython)
  n = 0.720818
FEATURE [App::DocumentObjectGroupPython] N_element034  label="N_element : 0.076"  # scripted group (container) (typed FeaturePython)
  n = 0.0764169
FEATURE [App::DocumentObjectGroupPython] O_element074  label="O_element : 0.087"  # scripted group (container) (typed FeaturePython)
  n = 0.0872889
FEATURE [App::DocumentObjectGroupPython] G4_NYLON_11_RILSAN  label="G4_NYLON-11_RILSAN"  # scripted group (container) (typed FeaturePython)
  Dunit = g/cm3
  Dvalue = 1.425
  Group = -> [H_element066,C_element072,N_element034,O_element074]
  conduct = 2
  density = 1
  expand = 3
  formula = G4_NYLON-11_RILSAN
  name = G4_NYLON-11_RILSAN
  specific = 4
FEATURE [App::DocumentObjectGroupPython] C_element073  label="C_element : 8"  # scripted group (container) (typed FeaturePython)
  n = 8
  ref = C_element
FEATURE [App::DocumentObjectGroupPython] H_element067  label="H_element : 18"  # scripted group (container) (typed FeaturePython)
  n = 18
  ref = H_element
FEATURE [App::DocumentObjectGroupPython] G4_OCTANE  # scripted group (container) (typed FeaturePython)
  Dunit = g/cm3
  Dvalue = 0.7026
  Group = -> [C_element073,H_element067]
  conduct = 2
  density = 1
  expand = 3
  formula = G4_OCTANE
  name = G4_OCTANE
  specific = 4
FEATURE [App::DocumentObjectGroupPython] C_element074  label="C_element : 25"  # scripted group (container) (typed FeaturePython)
  n = 25
  ref = C_element
FEATURE [App::DocumentObjectGroupPython] H_element068  label="H_element : 52"  # scripted group (container) (typed FeaturePython)
  n = 52
  ref = H_element
FEATURE [App::DocumentObjectGroupPython] G4_PARAFFIN  # scripted group (container) (typed FeaturePython)
  Dunit = g/cm3
  Dvalue = 0.93
  Group = -> [C_element074,H_element068]
  conduct = 2
  density = 1
  expand = 3
  formula = G4_PARAFFIN
  name = G4_PARAFFIN
  specific = 4
FEATURE [App::DocumentObjectGroupPython] C_element075  label="C_element : 036"  # scripted group (container) (typed FeaturePython)
  n = 5
  ref = C_element
FEATURE [App::DocumentObjectGroupPython] H_element069  label="H_element : 032"  # scripted group (container) (typed FeaturePython)
  n = 12
  ref = H_element
FEATURE [App::DocumentObjectGroupPython] G4_N_PENTANE  label="G4_N-PENTANE"  # scripted group (container) (typed FeaturePython)
  Dunit = g/cm3
  Dvalue = 0.6262
  Group = -> [C_element075,H_element069]
  conduct = 2
  density = 1
  expand = 3
  formula = G4_N-PENTANE
  name = G4_N-PENTANE
  specific = 4
FEATURE [App::DocumentObjectGroupPython] H_element070  label="H_element : 0.014"  # scripted group (container) (typed FeaturePython)
  n = 0.0141
FEATURE [App::DocumentObjectGroupPython] C_element076  label="C_element : 0.072"  # scripted group (container) (typed FeaturePython)
  n = 0.072261
FEATURE [App::DocumentObjectGroupPython] N_element035  label="N_element : 0.019"  # scripted group (container) (typed FeaturePython)
  n = 0.01932
FEATURE [App::DocumentObjectGroupPython] O_element075  label="O_element : 0.066"  # scripted group (container) (typed FeaturePython)
  n = 0.066101
FEATURE [App::DocumentObjectGroupPython] S_element019  label="S_element : 0.020"  # scripted group (container) (typed FeaturePython)
  n = 0.00189
FEATURE [App::DocumentObjectGroupPython] Br_element004  label="Br_element : 0.349"  # scripted group (container) (typed FeaturePython)
  n = 0.349103
FEATURE [App::DocumentObjectGroupPython] Ag_element001  label="Ag_element : 0.474"  # scripted group (container) (typed FeaturePython)
  n = 0.474105
FEATURE [App::DocumentObjectGroupPython] I_element005  label="I_element : 0.003"  # scripted group (container) (typed FeaturePython)
  n = 0.00312
FEATURE [App::DocumentObjectGroupPython] G4_PHOTO_EMULSION  # scripted group (container) (typed FeaturePython)
  Dunit = g/cm3
  Dvalue = 3.815
  Group = -> [H_element070,C_element076,N_element035,O_element075,S_element019,Br_element004,Ag_element001,I_element005]
  conduct = 2
  density = 1
  expand = 3
  formula = G4_PHOTO_EMULSION
  name = G4_PHOTO_EMULSION
  specific = 4
FEATURE [App::DocumentObjectGroupPython] C_element077  label="C_element : 9"  # scripted group (container) (typed FeaturePython)
  n = 9
  ref = C_element
FEATURE [App::DocumentObjectGroupPython] H_element071  label="H_element : 033"  # scripted group (container) (typed FeaturePython)
  n = 10
  ref = H_element
FEATURE [App::DocumentObjectGroupPython] G4_PLASTIC_SC_VINYLTOLUENE  # scripted group (container) (typed FeaturePython)
  Dunit = g/cm3
  Dvalue = 1.032
  Group = -> [C_element077,H_element071]
  conduct = 2
  density = 1
  expand = 3
  formula = G4_PLASTIC_SC_VINYLTOLUENE
  name = G4_PLASTIC_SC_VINYLTOLUENE
  specific = 4
FEATURE [App::DocumentObjectGroupPython] Pu_element001  label="Pu_element : 1"  # scripted group (container) (typed FeaturePython)
  n = 1
  ref = Pu_element
FEATURE [App::DocumentObjectGroupPython] O_element076  label="O_element : 037"  # scripted group (container) (typed FeaturePython)
  n = 2
  ref = O_element
FEATURE [App::DocumentObjectGroupPython] G4_PLUTONIUM_DIOXIDE  # scripted group (container) (typed FeaturePython)
  Dunit = g/cm3
  Dvalue = 11.46
  Group = -> [Pu_element001,O_element076]
  conduct = 2
  density = 1
  expand = 3
  formula = G4_PLUTONIUM_DIOXIDE
  name = G4_PLUTONIUM_DIOXIDE
  specific = 4
FEATURE [App::DocumentObjectGroupPython] C_element078  label="C_element : 037"  # scripted group (container) (typed FeaturePython)
  n = 3
  ref = C_element
FEATURE [App::DocumentObjectGroupPython] H_element072  label="H_element : 034"  # scripted group (container) (typed FeaturePython)
  n = 3
  ref = H_element
FEATURE [App::DocumentObjectGroupPython] N_element036  label="N_element : 015"  # scripted group (container) (typed FeaturePython)
  n = 1
  ref = N_element
FEATURE [App::DocumentObjectGroupPython] G4_POLYACRYLONITRILE  # scripted group (container) (typed FeaturePython)
  Dunit = g/cm3
  Dvalue = 1.17
  Group = -> [C_element078,H_element072,N_element036]
  conduct = 2
  density = 1
  expand = 3
  formula = G4_POLYACRYLONITRILE
  name = G4_POLYACRYLONITRILE
  specific = 4
FEATURE [App::DocumentObjectGroupPython] C_element079  label="C_element : 16"  # scripted group (container) (typed FeaturePython)
  n = 16
  ref = C_element
FEATURE [App::DocumentObjectGroupPython] H_element073  label="H_element : 035"  # scripted group (container) (typed FeaturePython)
  n = 14
  ref = H_element
FEATURE [App::DocumentObjectGroupPython] O_element077  label="O_element : 038"  # scripted group (container) (typed FeaturePython)
  n = 3
  ref = O_element
FEATURE [App::DocumentObjectGroupPython] G4_POLYCARBONATE  # scripted group (container) (typed FeaturePython)
  Dunit = g/cm3
  Dvalue = 1.2
  Group = -> [C_element079,H_element073,O_element077]
  conduct = 2
  density = 1
  expand = 3
  formula = G4_POLYCARBONATE
  name = G4_POLYCARBONATE
  specific = 4
FEATURE [App::DocumentObjectGroupPython] C_element080  label="C_element : 038"  # scripted group (container) (typed FeaturePython)
  n = 8
  ref = C_element
FEATURE [App::DocumentObjectGroupPython] H_element074  label="H_element : 036"  # scripted group (container) (typed FeaturePython)
  n = 7
  ref = H_element
FEATURE [App::DocumentObjectGroupPython] Cl_element017  label="Cl_element : 007"  # scripted group (container) (typed FeaturePython)
  n = 1
  ref = Cl_element
FEATURE [App::DocumentObjectGroupPython] G4_POLYCHLOROSTYRENE  # scripted group (container) (typed FeaturePython)
  Dunit = g/cm3
  Dvalue = 1.3
  Group = -> [C_element080,H_element074,Cl_element017]
  conduct = 2
  density = 1
  expand = 3
  formula = G4_POLYCHLOROSTYRENE
  name = G4_POLYCHLOROSTYRENE
  specific = 4
FEATURE [App::DocumentObjectGroupPython] C_element081  label="C_element : 039"  # scripted group (container) (typed FeaturePython)
  n = 1
  ref = C_element
FEATURE [App::DocumentObjectGroupPython] H_element075  label="H_element : 037"  # scripted group (container) (typed FeaturePython)
  n = 2
  ref = H_element
FEATURE [App::DocumentObjectGroupPython] G4_POLYETHYLENE  # scripted group (container) (typed FeaturePython)
  Dunit = g/cm3
  Dvalue = 0.94
  Group = -> [C_element081,H_element075]
  conduct = 2
  density = 1
  expand = 3
  formula = G4_POLYETHYLENE
  name = G4_POLYETHYLENE
  specific = 4
FEATURE [App::DocumentObjectGroupPython] C_element082  label="C_element : 040"  # scripted group (container) (typed FeaturePython)
  n = 10
  ref = C_element
FEATURE [App::DocumentObjectGroupPython] H_element076  label="H_element : 038"  # scripted group (container) (typed FeaturePython)
  n = 8
  ref = H_element
FEATURE [App::DocumentObjectGroupPython] O_element078  label="O_element : 039"  # scripted group (container) (typed FeaturePython)
  n = 4
  ref = O_element
FEATURE [App::DocumentObjectGroupPython] G4_MYLAR  # scripted group (container) (typed FeaturePython)
  Dunit = g/cm3
  Dvalue = 1.4
  Group = -> [C_element082,H_element076,O_element078]
  conduct = 2
  density = 1
  expand = 3
  formula = G4_MYLAR
  name = G4_MYLAR
  specific = 4
FEATURE [App::DocumentObjectGroupPython] C_element083  label="C_element : 041"  # scripted group (container) (typed FeaturePython)
  n = 5
  ref = C_element
FEATURE [App::DocumentObjectGroupPython] H_element077  label="H_element : 039"  # scripted group (container) (typed FeaturePython)
  n = 8
  ref = H_element
FEATURE [App::DocumentObjectGroupPython] O_element079  label="O_element : 040"  # scripted group (container) (typed FeaturePython)
  n = 2
  ref = O_element
FEATURE [App::DocumentObjectGroupPython] G4_PLEXIGLASS  # scripted group (container) (typed FeaturePython)
  Dunit = g/cm3
  Dvalue = 1.19
  Group = -> [C_element083,H_element077,O_element079]
  conduct = 2
  density = 1
  expand = 3
  formula = G4_PLEXIGLASS
  name = G4_PLEXIGLASS
  specific = 4
FEATURE [App::DocumentObjectGroupPython] C_element084  label="C_element : 042"  # scripted group (container) (typed FeaturePython)
  n = 1
  ref = C_element
FEATURE [App::DocumentObjectGroupPython] H_element078  label="H_element : 040"  # scripted group (container) (typed FeaturePython)
  n = 2
  ref = H_element
FEATURE [App::DocumentObjectGroupPython] O_element080  label="O_element : 041"  # scripted group (container) (typed FeaturePython)
  n = 1
  ref = O_element
FEATURE [App::DocumentObjectGroupPython] G4_POLYOXYMETHYLENE  # scripted group (container) (typed FeaturePython)
  Dunit = g/cm3
  Dvalue = 1.425
  Group = -> [C_element084,H_element078,O_element080]
  conduct = 2
  density = 1
  expand = 3
  formula = G4_POLYOXYMETHYLENE
  name = G4_POLYOXYMETHYLENE
  specific = 4
FEATURE [App::DocumentObjectGroupPython] C_element085  label="C_element : 043"  # scripted group (container) (typed FeaturePython)
  n = 2
  ref = C_element
FEATURE [App::DocumentObjectGroupPython] H_element079  label="H_element : 041"  # scripted group (container) (typed FeaturePython)
  n = 4
  ref = H_element
FEATURE [App::DocumentObjectGroupPython] G4_POLYPROPYLENE  # scripted group (container) (typed FeaturePython)
  Dunit = g/cm3
  Dvalue = 0.9
  Group = -> [C_element085,H_element079]
  conduct = 2
  density = 1
  expand = 3
  formula = G4_POLYPROPYLENE
  name = G4_POLYPROPYLENE
  specific = 4
FEATURE [App::DocumentObjectGroupPython] C_element086  label="C_element : 044"  # scripted group (container) (typed FeaturePython)
  n = 8
  ref = C_element
FEATURE [App::DocumentObjectGroupPython] H_element080  label="H_element : 042"  # scripted group (container) (typed FeaturePython)
  n = 8
  ref = H_element
FEATURE [App::DocumentObjectGroupPython] G4_POLYSTYRENE  # scripted group (container) (typed FeaturePython)
  Dunit = g/cm3
  Dvalue = 1.06
  Group = -> [C_element086,H_element080]
  conduct = 2
  density = 1
  expand = 3
  formula = G4_POLYSTYRENE
  name = G4_POLYSTYRENE
  specific = 4
FEATURE [App::DocumentObjectGroupPython] C_element087  label="C_element : 045"  # scripted group (container) (typed FeaturePython)
  n = 2
  ref = C_element
FEATURE [App::DocumentObjectGroupPython] F_element014  label="F_element : 4"  # scripted group (container) (typed FeaturePython)
  n = 4
  ref = F_element
FEATURE [App::DocumentObjectGroupPython] G4_TEFLON  # scripted group (container) (typed FeaturePython)
  Dunit = g/cm3
  Dvalue = 2.2
  Group = -> [C_element087,F_element014]
  conduct = 2
  density = 1
  expand = 3
  formula = G4_TEFLON
  name = G4_TEFLON
  specific = 4
FEATURE [App::DocumentObjectGroupPython] C_element088  label="C_element : 046"  # scripted group (container) (typed FeaturePython)
  n = 2
  ref = C_element
FEATURE [App::DocumentObjectGroupPython] F_element015  label="F_element : 006"  # scripted group (container) (typed FeaturePython)
  n = 3
  ref = F_element
FEATURE [App::DocumentObjectGroupPython] Cl_element018  label="Cl_element : 008"  # scripted group (container) (typed FeaturePython)
  n = 1
  ref = Cl_element
FEATURE [App::DocumentObjectGroupPython] G4_POLYTRIFLUOROCHLOROETHYLENE  # scripted group (container) (typed FeaturePython)
  Dunit = g/cm3
  Dvalue = 2.1
  Group = -> [C_element088,F_element015,Cl_element018]
  conduct = 2
  density = 1
  expand = 3
  formula = G4_POLYTRIFLUOROCHLOROETHYLENE
  name = G4_POLYTRIFLUOROCHLOROETHYLENE
  specific = 4
FEATURE [App::DocumentObjectGroupPython] C_element089  label="C_element : 047"  # scripted group (container) (typed FeaturePython)
  n = 4
  ref = C_element
FEATURE [App::DocumentObjectGroupPython] H_element081  label="H_element : 043"  # scripted group (container) (typed FeaturePython)
  n = 6
  ref = H_element
FEATURE [App::DocumentObjectGroupPython] O_element081  label="O_element : 042"  # scripted group (container) (typed FeaturePython)
  n = 2
  ref = O_element
FEATURE [App::DocumentObjectGroupPython] G4_POLYVINYL_ACETATE  # scripted group (container) (typed FeaturePython)
  Dunit = g/cm3
  Dvalue = 1.19
  Group = -> [C_element089,H_element081,O_element081]
  conduct = 2
  density = 1
  expand = 3
  formula = G4_POLYVINYL_ACETATE
  name = G4_POLYVINYL_ACETATE
  specific = 4
FEATURE [App::DocumentObjectGroupPython] C_element090  label="C_element : 048"  # scripted group (container) (typed FeaturePython)
  n = 2
  ref = C_element
FEATURE [App::DocumentObjectGroupPython] H_element082  label="H_element : 044"  # scripted group (container) (typed FeaturePython)
  n = 4
  ref = H_element
FEATURE [App::DocumentObjectGroupPython] O_element082  label="O_element : 043"  # scripted group (container) (typed FeaturePython)
  n = 1
  ref = O_element
FEATURE [App::DocumentObjectGroupPython] G4_POLYVINYL_ALCOHOL  # scripted group (container) (typed FeaturePython)
  Dunit = g/cm3
  Dvalue = 1.3
  Group = -> [C_element090,H_element082,O_element082]
  conduct = 2
  density = 1
  expand = 3
  formula = G4_POLYVINYL_ALCOHOL
  name = G4_POLYVINYL_ALCOHOL
  specific = 4
FEATURE [App::DocumentObjectGroupPython] C_element091  label="C_element : 049"  # scripted group (container) (typed FeaturePython)
  n = 8
  ref = C_element
FEATURE [App::DocumentObjectGroupPython] H_element083  label="H_element : 045"  # scripted group (container) (typed FeaturePython)
  n = 14
  ref = H_element
FEATURE [App::DocumentObjectGroupPython] O_element083  label="O_element : 044"  # scripted group (container) (typed FeaturePython)
  n = 2
  ref = O_element
FEATURE [App::DocumentObjectGroupPython] G4_POLYVINYL_BUTYRAL  # scripted group (container) (typed FeaturePython)
  Dunit = g/cm3
  Dvalue = 1.12
  Group = -> [C_element091,H_element083,O_element083]
  conduct = 2
  density = 1
  expand = 3
  formula = G4_POLYVINYL_BUTYRAL
  name = G4_POLYVINYL_BUTYRAL
  specific = 4
FEATURE [App::DocumentObjectGroupPython] C_element092  label="C_element : 050"  # scripted group (container) (typed FeaturePython)
  n = 2
  ref = C_element
FEATURE [App::DocumentObjectGroupPython] H_element084  label="H_element : 046"  # scripted group (container) (typed FeaturePython)
  n = 3
  ref = H_element
FEATURE [App::DocumentObjectGroupPython] Cl_element019  label="Cl_element : 009"  # scripted group (container) (typed FeaturePython)
  n = 1
  ref = Cl_element
FEATURE [App::DocumentObjectGroupPython] G4_POLYVINYL_CHLORIDE  # scripted group (container) (typed FeaturePython)
  Dunit = g/cm3
  Dvalue = 1.3
  Group = -> [C_element092,H_element084,Cl_element019]
  conduct = 2
  density = 1
  expand = 3
  formula = G4_POLYVINYL_CHLORIDE
  name = G4_POLYVINYL_CHLORIDE
  specific = 4
FEATURE [App::DocumentObjectGroupPython] C_element093  label="C_element : 051"  # scripted group (container) (typed FeaturePython)
  n = 2
  ref = C_element
FEATURE [App::DocumentObjectGroupPython] H_element085  label="H_element : 047"  # scripted group (container) (typed FeaturePython)
  n = 2
  ref = H_element
FEATURE [App::DocumentObjectGroupPython] Cl_element020  label="Cl_element : 010"  # scripted group (container) (typed FeaturePython)
  n = 2
  ref = Cl_element
FEATURE [App::DocumentObjectGroupPython] G4_POLYVINYLIDENE_CHLORIDE  # scripted group (container) (typed FeaturePython)
  Dunit = g/cm3
  Dvalue = 1.7
  Group = -> [C_element093,H_element085,Cl_element020]
  conduct = 2
  density = 1
  expand = 3
  formula = G4_POLYVINYLIDENE_CHLORIDE
  name = G4_POLYVINYLIDENE_CHLORIDE
  specific = 4
FEATURE [App::DocumentObjectGroupPython] C_element094  label="C_element : 052"  # scripted group (container) (typed FeaturePython)
  n = 2
  ref = C_element
FEATURE [App::DocumentObjectGroupPython] H_element086  label="H_element : 048"  # scripted group (container) (typed FeaturePython)
  n = 2
  ref = H_element
FEATURE [App::DocumentObjectGroupPython] F_element016  label="F_element : 007"  # scripted group (container) (typed FeaturePython)
  n = 2
  ref = F_element
FEATURE [App::DocumentObjectGroupPython] G4_POLYVINYLIDENE_FLUORIDE  # scripted group (container) (typed FeaturePython)
  Dunit = g/cm3
  Dvalue = 1.76
  Group = -> [C_element094,H_element086,F_element016]
  conduct = 2
  density = 1
  expand = 3
  formula = G4_POLYVINYLIDENE_FLUORIDE
  name = G4_POLYVINYLIDENE_FLUORIDE
  specific = 4
FEATURE [App::DocumentObjectGroupPython] C_element095  label="C_element : 053"  # scripted group (container) (typed FeaturePython)
  n = 6
  ref = C_element
FEATURE [App::DocumentObjectGroupPython] H_element087  label="H_element : 9"  # scripted group (container) (typed FeaturePython)
  n = 9
  ref = H_element
FEATURE [App::DocumentObjectGroupPython] N_element037  label="N_element : 016"  # scripted group (container) (typed FeaturePython)
  n = 1
  ref = N_element
FEATURE [App::DocumentObjectGroupPython] O_element084  label="O_element : 045"  # scripted group (container) (typed FeaturePython)
  n = 1
  ref = O_element
FEATURE [App::DocumentObjectGroupPython] G4_POLYVINYL_PYRROLIDONE  # scripted group (container) (typed FeaturePython)
  Dunit = g/cm3
  Dvalue = 1.25
  Group = -> [C_element095,H_element087,N_element037,O_element084]
  conduct = 2
  density = 1
  expand = 3
  formula = G4_POLYVINYL_PYRROLIDONE
  name = G4_POLYVINYL_PYRROLIDONE
  specific = 4
FEATURE [App::DocumentObjectGroupPython] K_element008  label="K_element : 1"  # scripted group (container) (typed FeaturePython)
  n = 1
  ref = K_element
FEATURE [App::DocumentObjectGroupPython] I_element006  label="I_element : 003"  # scripted group (container) (typed FeaturePython)
  n = 1
  ref = I_element
FEATURE [App::DocumentObjectGroupPython] G4_POTASSIUM_IODIDE  # scripted group (container) (typed FeaturePython)
  Dunit = g/cm3
  Dvalue = 3.13
  Group = -> [K_element008,I_element006]
  conduct = 2
  density = 1
  expand = 3
  formula = G4_POTASSIUM_IODIDE
  name = G4_POTASSIUM_IODIDE
  specific = 4
FEATURE [App::DocumentObjectGroupPython] K_element009  label="K_element : 2"  # scripted group (container) (typed FeaturePython)
  n = 2
  ref = K_element
FEATURE [App::DocumentObjectGroupPython] O_element085  label="O_element : 046"  # scripted group (container) (typed FeaturePython)
  n = 1
  ref = O_element
FEATURE [App::DocumentObjectGroupPython] G4_POTASSIUM_OXIDE  # scripted group (container) (typed FeaturePython)
  Dunit = g/cm3
  Dvalue = 2.32
  Group = -> [K_element009,O_element085]
  conduct = 2
  density = 1
  expand = 3
  formula = G4_POTASSIUM_OXIDE
  name = G4_POTASSIUM_OXIDE
  specific = 4
FEATURE [App::DocumentObjectGroupPython] C_element096  label="C_element : 054"  # scripted group (container) (typed FeaturePython)
  n = 3
  ref = C_element
FEATURE [App::DocumentObjectGroupPython] H_element088  label="H_element : 049"  # scripted group (container) (typed FeaturePython)
  n = 8
  ref = H_element
FEATURE [App::DocumentObjectGroupPython] G4_PROPANE  # scripted group (container) (typed FeaturePython)
  Dunit = g/cm3
  Dvalue = 0.00187939
  Group = -> [C_element096,H_element088]
  conduct = 2
  density = 1
  expand = 3
  formula = G4_PROPANE
  name = G4_PROPANE
  specific = 4
FEATURE [App::DocumentObjectGroupPython] C_element097  label="C_element : 055"  # scripted group (container) (typed FeaturePython)
  n = 3
  ref = C_element
FEATURE [App::DocumentObjectGroupPython] H_element089  label="H_element : 050"  # scripted group (container) (typed FeaturePython)
  n = 8
  ref = H_element
FEATURE [App::DocumentObjectGroupPython] G4_lPROPANE  # scripted group (container) (typed FeaturePython)
  Dunit = g/cm3
  Dvalue = 0.43
  Group = -> [C_element097,H_element089]
  conduct = 2
  density = 1
  expand = 3
  formula = G4_lPROPANE
  name = G4_lPROPANE
  specific = 4
FEATURE [App::DocumentObjectGroupPython] C_element098  label="C_element : 056"  # scripted group (container) (typed FeaturePython)
  n = 3
  ref = C_element
FEATURE [App::DocumentObjectGroupPython] H_element090  label="H_element : 051"  # scripted group (container) (typed FeaturePython)
  n = 8
  ref = H_element
FEATURE [App::DocumentObjectGroupPython] O_element086  label="O_element : 047"  # scripted group (container) (typed FeaturePython)
  n = 1
  ref = O_element
FEATURE [App::DocumentObjectGroupPython] G4_N_PROPYL_ALCOHOL  label="G4_N-PROPYL_ALCOHOL"  # scripted group (container) (typed FeaturePython)
  Dunit = g/cm3
  Dvalue = 0.8035
  Group = -> [C_element098,H_element090,O_element086]
  conduct = 2
  density = 1
  expand = 3
  formula = G4_N-PROPYL_ALCOHOL
  name = G4_N-PROPYL_ALCOHOL
  specific = 4
FEATURE [App::DocumentObjectGroupPython] C_element099  label="C_element : 057"  # scripted group (container) (typed FeaturePython)
  n = 5
  ref = C_element
FEATURE [App::DocumentObjectGroupPython] H_element091  label="H_element : 052"  # scripted group (container) (typed FeaturePython)
  n = 5
  ref = H_element
FEATURE [App::DocumentObjectGroupPython] N_element038  label="N_element : 017"  # scripted group (container) (typed FeaturePython)
  n = 1
  ref = N_element
FEATURE [App::DocumentObjectGroupPython] G4_PYRIDINE  # scripted group (container) (typed FeaturePython)
  Dunit = g/cm3
  Dvalue = 0.9819
  Group = -> [C_element099,H_element091,N_element038]
  conduct = 2
  density = 1
  expand = 3
  formula = G4_PYRIDINE
  name = G4_PYRIDINE
  specific = 4
FEATURE [App::DocumentObjectGroupPython] H_element092  label="H_element : 0.144"  # scripted group (container) (typed FeaturePython)
  n = 0.143711
FEATURE [App::DocumentObjectGroupPython] C_element100  label="C_element : 0.856"  # scripted group (container) (typed FeaturePython)
  n = 0.856289
FEATURE [App::DocumentObjectGroupPython] G4_RUBBER_BUTYL  # scripted group (container) (typed FeaturePython)
  Dunit = g/cm3
  Dvalue = 0.92
  Group = -> [H_element092,C_element100]
  conduct = 2
  density = 1
  expand = 3
  formula = G4_RUBBER_BUTYL
  name = G4_RUBBER_BUTYL
  specific = 4
FEATURE [App::DocumentObjectGroupPython] H_element093  label="H_element : 0.118"  # scripted group (container) (typed FeaturePython)
  n = 0.118371
FEATURE [App::DocumentObjectGroupPython] C_element101  label="C_element : 0.882"  # scripted group (container) (typed FeaturePython)
  n = 0.881629
FEATURE [App::DocumentObjectGroupPython] G4_RUBBER_NATURAL  # scripted group (container) (typed FeaturePython)
  Dunit = g/cm3
  Dvalue = 0.92
  Group = -> [H_element093,C_element101]
  conduct = 2
  density = 1
  expand = 3
  formula = G4_RUBBER_NATURAL
  name = G4_RUBBER_NATURAL
  specific = 4
FEATURE [App::DocumentObjectGroupPython] H_element094  label="H_element : 0.145"  # scripted group (container) (typed FeaturePython)
  n = 0.05692
FEATURE [App::DocumentObjectGroupPython] C_element102  label="C_element : 0.543"  # scripted group (container) (typed FeaturePython)
  n = 0.542646
FEATURE [App::DocumentObjectGroupPython] Cl_element021  label="Cl_element : 0.400"  # scripted group (container) (typed FeaturePython)
  n = 0.400434
FEATURE [App::DocumentObjectGroupPython] G4_RUBBER_NEOPRENE  # scripted group (container) (typed FeaturePython)
  Dunit = g/cm3
  Dvalue = 1.23
  Group = -> [H_element094,C_element102,Cl_element021]
  conduct = 2
  density = 1
  expand = 3
  formula = G4_RUBBER_NEOPRENE
  name = G4_RUBBER_NEOPRENE
  specific = 4
FEATURE [App::DocumentObjectGroupPython] Si_element006  label="Si_element : 1"  # scripted group (container) (typed FeaturePython)
  n = 1
  ref = Si_element
FEATURE [App::DocumentObjectGroupPython] O_element087  label="O_element : 048"  # scripted group (container) (typed FeaturePython)
  n = 2
  ref = O_element
FEATURE [App::DocumentObjectGroupPython] G4_SILICON_DIOXIDE001  label="G4_SILICON_DIOXIDE"  # scripted group (container) (typed FeaturePython)
  Dunit = g/cm3
  Dvalue = 2.32
  Group = -> [Si_element006,O_element087]
  conduct = 2
  density = 1
  expand = 3
  formula = G4_SILICON_DIOXIDE
  name = G4_SILICON_DIOXIDE
  specific = 4
FEATURE [App::DocumentObjectGroupPython] Ag_element002  label="Ag_element : 1"  # scripted group (container) (typed FeaturePython)
  n = 1
  ref = Ag_element
FEATURE [App::DocumentObjectGroupPython] Br_element005  label="Br_element : 003"  # scripted group (container) (typed FeaturePython)
  n = 1
  ref = Br_element
FEATURE [App::DocumentObjectGroupPython] G4_SILVER_BROMIDE  # scripted group (container) (typed FeaturePython)
  Dunit = g/cm3
  Dvalue = 6.473
  Group = -> [Ag_element002,Br_element005]
  conduct = 2
  density = 1
  expand = 3
  formula = G4_SILVER_BROMIDE
  name = G4_SILVER_BROMIDE
  specific = 4
FEATURE [App::DocumentObjectGroupPython] Ag_element003  label="Ag_element : 002"  # scripted group (container) (typed FeaturePython)
  n = 1
  ref = Ag_element
FEATURE [App::DocumentObjectGroupPython] Cl_element022  label="Cl_element : 011"  # scripted group (container) (typed FeaturePython)
  n = 1
  ref = Cl_element
FEATURE [App::DocumentObjectGroupPython] G4_SILVER_CHLORIDE  # scripted group (container) (typed FeaturePython)
  Dunit = g/cm3
  Dvalue = 5.56
  Group = -> [Ag_element003,Cl_element022]
  conduct = 2
  density = 1
  expand = 3
  formula = G4_SILVER_CHLORIDE
  name = G4_SILVER_CHLORIDE
  specific = 4
FEATURE [App::DocumentObjectGroupPython] Br_element006  label="Br_element : 0.423"  # scripted group (container) (typed FeaturePython)
  n = 0.422895
FEATURE [App::DocumentObjectGroupPython] Ag_element004  label="Ag_element : 0.574"  # scripted group (container) (typed FeaturePython)
  n = 0.573748
FEATURE [App::DocumentObjectGroupPython] I_element007  label="I_element : 0.649"  # scripted group (container) (typed FeaturePython)
  n = 0.003357
FEATURE [App::DocumentObjectGroupPython] G4_SILVER_HALIDES  # scripted group (container) (typed FeaturePython)
  Dunit = g/cm3
  Dvalue = 6.47
  Group = -> [Br_element006,Ag_element004,I_element007]
  conduct = 2
  density = 1
  expand = 3
  formula = G4_SILVER_HALIDES
  name = G4_SILVER_HALIDES
  specific = 4
FEATURE [App::DocumentObjectGroupPython] Ag_element005  label="Ag_element : 003"  # scripted group (container) (typed FeaturePython)
  n = 1
  ref = Ag_element
FEATURE [App::DocumentObjectGroupPython] I_element008  label="I_element : 004"  # scripted group (container) (typed FeaturePython)
  n = 1
  ref = I_element
FEATURE [App::DocumentObjectGroupPython] G4_SILVER_IODIDE  # scripted group (container) (typed FeaturePython)
  Dunit = g/cm3
  Dvalue = 6.01
  Group = -> [Ag_element005,I_element008]
  conduct = 2
  density = 1
  expand = 3
  formula = G4_SILVER_IODIDE
  name = G4_SILVER_IODIDE
  specific = 4
FEATURE [App::DocumentObjectGroupPython] H_element095  label="H_element : 0.100"  # scripted group (container) (typed FeaturePython)
  n = 0.1
FEATURE [App::DocumentObjectGroupPython] C_element103  label="C_element : 0.204"  # scripted group (container) (typed FeaturePython)
  n = 0.204
FEATURE [App::DocumentObjectGroupPython] N_element039  label="N_element : 0.759"  # scripted group (container) (typed FeaturePython)
  n = 0.042
FEATURE [App::DocumentObjectGroupPython] O_element088  label="O_element : 0.645"  # scripted group (container) (typed FeaturePython)
  n = 0.645
FEATURE [App::DocumentObjectGroupPython] Na_element013  label="Na_element : 0.100"  # scripted group (container) (typed FeaturePython)
  n = 0.002
FEATURE [App::DocumentObjectGroupPython] P_element009  label="P_element : 0.107"  # scripted group (container) (typed FeaturePython)
  n = 0.001
FEATURE [App::DocumentObjectGroupPython] S_element020  label="S_element : 0.021"  # scripted group (container) (typed FeaturePython)
  n = 0.002
FEATURE [App::DocumentObjectGroupPython] Cl_element023  label="Cl_element : 0.590"  # scripted group (container) (typed FeaturePython)
  n = 0.003
FEATURE [App::DocumentObjectGroupPython] K_element010  label="K_element : 0.001"  # scripted group (container) (typed FeaturePython)
  n = 0.001
FEATURE [App::DocumentObjectGroupPython] G4_SKIN_ICRP  # scripted group (container) (typed FeaturePython)
  Dunit = g/cm3
  Dvalue = 1.09
  Group = -> [H_element095,C_element103,N_element039,O_element088,Na_element013,P_element009,S_element020,Cl_element023,K_element010]
  conduct = 2
  density = 1
  expand = 3
  formula = G4_SKIN_ICRP
  name = G4_SKIN_ICRP
  specific = 4
FEATURE [App::DocumentObjectGroupPython] Na_element014  label="Na_element : 2"  # scripted group (container) (typed FeaturePython)
  n = 2
  ref = Na_element
FEATURE [App::DocumentObjectGroupPython] C_element104  label="C_element : 058"  # scripted group (container) (typed FeaturePython)
  n = 1
  ref = C_element
FEATURE [App::DocumentObjectGroupPython] O_element089  label="O_element : 049"  # scripted group (container) (typed FeaturePython)
  n = 3
  ref = O_element
FEATURE [App::DocumentObjectGroupPython] G4_SODIUM_CARBONATE  # scripted group (container) (typed FeaturePython)
  Dunit = g/cm3
  Dvalue = 2.532
  Group = -> [Na_element014,C_element104,O_element089]
  conduct = 2
  density = 1
  expand = 3
  formula = G4_SODIUM_CARBONATE
  name = G4_SODIUM_CARBONATE
  specific = 4
FEATURE [App::DocumentObjectGroupPython] Na_element015  label="Na_element : 1"  # scripted group (container) (typed FeaturePython)
  n = 1
  ref = Na_element
FEATURE [App::DocumentObjectGroupPython] I_element009  label="I_element : 005"  # scripted group (container) (typed FeaturePython)
  n = 1
  ref = I_element
FEATURE [App::DocumentObjectGroupPython] G4_SODIUM_IODIDE  # scripted group (container) (typed FeaturePython)
  Dunit = g/cm3
  Dvalue = 3.667
  Group = -> [Na_element015,I_element009]
  conduct = 2
  density = 1
  expand = 3
  formula = G4_SODIUM_IODIDE
  name = G4_SODIUM_IODIDE
  specific = 4
FEATURE [App::DocumentObjectGroupPython] Na_element016  label="Na_element : 003"  # scripted group (container) (typed FeaturePython)
  n = 2
  ref = Na_element
FEATURE [App::DocumentObjectGroupPython] O_element090  label="O_element : 050"  # scripted group (container) (typed FeaturePython)
  n = 1
  ref = O_element
FEATURE [App::DocumentObjectGroupPython] G4_SODIUM_MONOXIDE  # scripted group (container) (typed FeaturePython)
  Dunit = g/cm3
  Dvalue = 2.27
  Group = -> [Na_element016,O_element090]
  conduct = 2
  density = 1
  expand = 3
  formula = G4_SODIUM_MONOXIDE
  name = G4_SODIUM_MONOXIDE
  specific = 4
FEATURE [App::DocumentObjectGroupPython] Na_element017  label="Na_element : 004"  # scripted group (container) (typed FeaturePython)
  n = 1
  ref = Na_element
FEATURE [App::DocumentObjectGroupPython] N_element040  label="N_element : 018"  # scripted group (container) (typed FeaturePython)
  n = 1
  ref = N_element
FEATURE [App::DocumentObjectGroupPython] O_element091  label="O_element : 051"  # scripted group (container) (typed FeaturePython)
  n = 3
  ref = O_element
FEATURE [App::DocumentObjectGroupPython] G4_SODIUM_NITRATE  # scripted group (container) (typed FeaturePython)
  Dunit = g/cm3
  Dvalue = 2.261
  Group = -> [Na_element017,N_element040,O_element091]
  conduct = 2
  density = 1
  expand = 3
  formula = G4_SODIUM_NITRATE
  name = G4_SODIUM_NITRATE
  specific = 4
FEATURE [App::DocumentObjectGroupPython] C_element105  label="C_element : 059"  # scripted group (container) (typed FeaturePython)
  n = 14
  ref = C_element
FEATURE [App::DocumentObjectGroupPython] H_element096  label="H_element : 053"  # scripted group (container) (typed FeaturePython)
  n = 12
  ref = H_element
FEATURE [App::DocumentObjectGroupPython] G4_STILBENE  # scripted group (container) (typed FeaturePython)
  Dunit = g/cm3
  Dvalue = 0.9707
  Group = -> [C_element105,H_element096]
  conduct = 2
  density = 1
  expand = 3
  formula = G4_STILBENE
  name = G4_STILBENE
  specific = 4
FEATURE [App::DocumentObjectGroupPython] C_element106  label="C_element : 12"  # scripted group (container) (typed FeaturePython)
  n = 12
  ref = C_element
FEATURE [App::DocumentObjectGroupPython] H_element097  label="H_element : 22"  # scripted group (container) (typed FeaturePython)
  n = 22
  ref = H_element
FEATURE [App::DocumentObjectGroupPython] O_element092  label="O_element : 11"  # scripted group (container) (typed FeaturePython)
  n = 11
  ref = O_element
FEATURE [App::DocumentObjectGroupPython] G4_SUCROSE  # scripted group (container) (typed FeaturePython)
  Dunit = g/cm3
  Dvalue = 1.5805
  Group = -> [C_element106,H_element097,O_element092]
  conduct = 2
  density = 1
  expand = 3
  formula = G4_SUCROSE
  name = G4_SUCROSE
  specific = 4
FEATURE [App::DocumentObjectGroupPython] C_element107  label="C_element : 18"  # scripted group (container) (typed FeaturePython)
  n = 18
  ref = C_element
FEATURE [App::DocumentObjectGroupPython] H_element098  label="H_element : 054"  # scripted group (container) (typed FeaturePython)
  n = 14
  ref = H_element
FEATURE [App::DocumentObjectGroupPython] G4_TERPHENYL  # scripted group (container) (typed FeaturePython)
  Dunit = g/cm3
  Dvalue = 1.24
  Group = -> [C_element107,H_element098]
  conduct = 2
  density = 1
  expand = 3
  formula = G4_TERPHENYL
  name = G4_TERPHENYL
  specific = 4
FEATURE [App::DocumentObjectGroupPython] H_element099  label="H_element : 0.146"  # scripted group (container) (typed FeaturePython)
  n = 0.106
FEATURE [App::DocumentObjectGroupPython] C_element108  label="C_element : 0.883"  # scripted group (container) (typed FeaturePython)
  n = 0.099
FEATURE [App::DocumentObjectGroupPython] N_element041  label="N_element : 0.020"  # scripted group (container) (typed FeaturePython)
  n = 0.02
FEATURE [App::DocumentObjectGroupPython] O_element093  label="O_element : 0.766"  # scripted group (container) (typed FeaturePython)
  n = 0.766
FEATURE [App::DocumentObjectGroupPython] Na_element018  label="Na_element : 0.101"  # scripted group (container) (typed FeaturePython)
  n = 0.002
FEATURE [App::DocumentObjectGroupPython] P_element010  label="P_element : 0.108"  # scripted group (container) (typed FeaturePython)
  n = 0.001
FEATURE [App::DocumentObjectGroupPython] S_element021  label="S_element : 0.022"  # scripted group (container) (typed FeaturePython)
  n = 0.002
FEATURE [App::DocumentObjectGroupPython] Cl_element024  label="Cl_element : 0.002"  # scripted group (container) (typed FeaturePython)
  n = 0.002
FEATURE [App::DocumentObjectGroupPython] K_element011  label="K_element : 0.017"  # scripted group (container) (typed FeaturePython)
  n = 0.002
FEATURE [App::DocumentObjectGroupPython] G4_TESTIS_ICRP  # scripted group (container) (typed FeaturePython)
  Dunit = g/cm3
  Dvalue = 1.04
  Group = -> [H_element099,C_element108,N_element041,O_element093,Na_element018,P_element010,S_element021,Cl_element024,K_element011]
  conduct = 2
  density = 1
  expand = 3
  formula = G4_TESTIS_ICRP
  name = G4_TESTIS_ICRP
  specific = 4
FEATURE [App::DocumentObjectGroupPython] C_element109  label="C_element : 060"  # scripted group (container) (typed FeaturePython)
  n = 2
  ref = C_element
FEATURE [App::DocumentObjectGroupPython] Cl_element025  label="Cl_element : 012"  # scripted group (container) (typed FeaturePython)
  n = 4
  ref = Cl_element
FEATURE [App::DocumentObjectGroupPython] G4_TETRACHLOROETHYLENE  # scripted group (container) (typed FeaturePython)
  Dunit = g/cm3
  Dvalue = 1.625
  Group = -> [C_element109,Cl_element025]
  conduct = 2
  density = 1
  expand = 3
  formula = G4_TETRACHLOROETHYLENE
  name = G4_TETRACHLOROETHYLENE
  specific = 4
FEATURE [App::DocumentObjectGroupPython] Tl_element001  label="Tl_element : 1"  # scripted group (container) (typed FeaturePython)
  n = 1
  ref = Tl_element
FEATURE [App::DocumentObjectGroupPython] Cl_element026  label="Cl_element : 013"  # scripted group (container) (typed FeaturePython)
  n = 1
  ref = Cl_element
FEATURE [App::DocumentObjectGroupPython] G4_THALLIUM_CHLORIDE  # scripted group (container) (typed FeaturePython)
  Dunit = g/cm3
  Dvalue = 7.004
  Group = -> [Tl_element001,Cl_element026]
  conduct = 2
  density = 1
  expand = 3
  formula = G4_THALLIUM_CHLORIDE
  name = G4_THALLIUM_CHLORIDE
  specific = 4
FEATURE [App::DocumentObjectGroupPython] H_element100  label="H_element : 0.147"  # scripted group (container) (typed FeaturePython)
  n = 0.105
FEATURE [App::DocumentObjectGroupPython] C_element110  label="C_element : 0.256"  # scripted group (container) (typed FeaturePython)
  n = 0.256
FEATURE [App::DocumentObjectGroupPython] N_element042  label="N_element : 0.760"  # scripted group (container) (typed FeaturePython)
  n = 0.027
FEATURE [App::DocumentObjectGroupPython] O_element094  label="O_element : 0.602"  # scripted group (container) (typed FeaturePython)
  n = 0.602
FEATURE [App::DocumentObjectGroupPython] Na_element019  label="Na_element : 0.102"  # scripted group (container) (typed FeaturePython)
  n = 0.001
FEATURE [App::DocumentObjectGroupPython] P_element011  label="P_element : 0.109"  # scripted group (container) (typed FeaturePython)
  n = 0.002
FEATURE [App::DocumentObjectGroupPython] S_element022  label="S_element : 0.023"  # scripted group (container) (typed FeaturePython)
  n = 0.003
FEATURE [App::DocumentObjectGroupPython] Cl_element027  label="Cl_element : 0.591"  # scripted group (container) (typed FeaturePython)
  n = 0.002
FEATURE [App::DocumentObjectGroupPython] K_element012  label="K_element : 0.018"  # scripted group (container) (typed FeaturePython)
  n = 0.002
FEATURE [App::DocumentObjectGroupPython] G4_TISSUE_SOFT_ICRP  # scripted group (container) (typed FeaturePython)
  Dunit = g/cm3
  Dvalue = 1.03
  Group = -> [H_element100,C_element110,N_element042,O_element094,Na_element019,P_element011,S_element022,Cl_element027,K_element012]
  conduct = 2
  density = 1
  expand = 3
  formula = G4_TISSUE_SOFT_ICRP
  name = G4_TISSUE_SOFT_ICRP
  specific = 4
FEATURE [App::DocumentObjectGroupPython] H_element101  label="H_element : 0.148"  # scripted group (container) (typed FeaturePython)
  n = 0.101
FEATURE [App::DocumentObjectGroupPython] C_element111  label="C_element : 0.111"  # scripted group (container) (typed FeaturePython)
  n = 0.111
FEATURE [App::DocumentObjectGroupPython] N_element043  label="N_element : 0.026"  # scripted group (container) (typed FeaturePython)
  n = 0.026
FEATURE [App::DocumentObjectGroupPython] O_element095  label="O_element : 0.762"  # scripted group (container) (typed FeaturePython)
  n = 0.762
FEATURE [App::DocumentObjectGroupPython] G4_TISSUE_SOFT_ICRU_4  label="G4_TISSUE_SOFT_ICRU-4"  # scripted group (container) (typed FeaturePython)
  Dunit = g/cm3
  Dvalue = 1
  Group = -> [H_element101,C_element111,N_element043,O_element095]
  conduct = 2
  density = 1
  expand = 3
  formula = G4_TISSUE_SOFT_ICRU-4
  name = G4_TISSUE_SOFT_ICRU-4
  specific = 4
FEATURE [App::DocumentObjectGroupPython] H_element102  label="H_element : 0.149"  # scripted group (container) (typed FeaturePython)
  n = 0.101869
FEATURE [App::DocumentObjectGroupPython] C_element112  label="C_element : 0.456"  # scripted group (container) (typed FeaturePython)
  n = 0.456179
FEATURE [App::DocumentObjectGroupPython] N_element044  label="N_element : 0.761"  # scripted group (container) (typed FeaturePython)
  n = 0.035172
FEATURE [App::DocumentObjectGroupPython] O_element096  label="O_element : 0.407"  # scripted group (container) (typed FeaturePython)
  n = 0.40678
FEATURE [App::DocumentObjectGroupPython] G4_TISSUE_METHANE  label="G4_TISSUE-METHANE"  # scripted group (container) (typed FeaturePython)
  Dunit = g/cm3
  Dvalue = 0.00106409
  Group = -> [H_element102,C_element112,N_element044,O_element096]
  conduct = 2
  density = 1
  expand = 3
  formula = G4_TISSUE-METHANE
  name = G4_TISSUE-METHANE
  specific = 4
FEATURE [App::DocumentObjectGroupPython] H_element103  label="H_element : 0.103"  # scripted group (container) (typed FeaturePython)
  n = 0.102672
FEATURE [App::DocumentObjectGroupPython] C_element113  label="C_element : 0.569"  # scripted group (container) (typed FeaturePython)
  n = 0.56894
FEATURE [App::DocumentObjectGroupPython] N_element045  label="N_element : 0.762"  # scripted group (container) (typed FeaturePython)
  n = 0.035022
FEATURE [App::DocumentObjectGroupPython] O_element097  label="O_element : 0.293"  # scripted group (container) (typed FeaturePython)
  n = 0.293366
FEATURE [App::DocumentObjectGroupPython] G4_TISSUE_PROPANE  label="G4_TISSUE-PROPANE"  # scripted group (container) (typed FeaturePython)
  Dunit = g/cm3
  Dvalue = 0.00182628
  Group = -> [H_element103,C_element113,N_element045,O_element097]
  conduct = 2
  density = 1
  expand = 3
  formula = G4_TISSUE-PROPANE
  name = G4_TISSUE-PROPANE
  specific = 4
FEATURE [App::DocumentObjectGroupPython] Ti_element003  label="Ti_element : 1"  # scripted group (container) (typed FeaturePython)
  n = 1
  ref = Ti_element
FEATURE [App::DocumentObjectGroupPython] O_element098  label="O_element : 052"  # scripted group (container) (typed FeaturePython)
  n = 2
  ref = O_element
FEATURE [App::DocumentObjectGroupPython] G4_TITANIUM_DIOXIDE  # scripted group (container) (typed FeaturePython)
  Dunit = g/cm3
  Dvalue = 4.26
  Group = -> [Ti_element003,O_element098]
  conduct = 2
  density = 1
  expand = 3
  formula = G4_TITANIUM_DIOXIDE
  name = G4_TITANIUM_DIOXIDE
  specific = 4
FEATURE [App::DocumentObjectGroupPython] C_element114  label="C_element : 061"  # scripted group (container) (typed FeaturePython)
  n = 7
  ref = C_element
FEATURE [App::DocumentObjectGroupPython] H_element104  label="H_element : 055"  # scripted group (container) (typed FeaturePython)
  n = 8
  ref = H_element
FEATURE [App::DocumentObjectGroupPython] G4_TOLUENE  # scripted group (container) (typed FeaturePython)
  Dunit = g/cm3
  Dvalue = 0.8669
  Group = -> [C_element114,H_element104]
  conduct = 2
  density = 1
  expand = 3
  formula = G4_TOLUENE
  name = G4_TOLUENE
  specific = 4
FEATURE [App::DocumentObjectGroupPython] C_element115  label="C_element : 062"  # scripted group (container) (typed FeaturePython)
  n = 2
  ref = C_element
FEATURE [App::DocumentObjectGroupPython] H_element105  label="H_element : 056"  # scripted group (container) (typed FeaturePython)
  n = 1
  ref = H_element
FEATURE [App::DocumentObjectGroupPython] Cl_element028  label="Cl_element : 014"  # scripted group (container) (typed FeaturePython)
  n = 3
  ref = Cl_element
FEATURE [App::DocumentObjectGroupPython] G4_TRICHLOROETHYLENE  # scripted group (container) (typed FeaturePython)
  Dunit = g/cm3
  Dvalue = 1.46
  Group = -> [C_element115,H_element105,Cl_element028]
  conduct = 2
  density = 1
  expand = 3
  formula = G4_TRICHLOROETHYLENE
  name = G4_TRICHLOROETHYLENE
  specific = 4
FEATURE [App::DocumentObjectGroupPython] C_element116  label="C_element : 063"  # scripted group (container) (typed FeaturePython)
  n = 6
  ref = C_element
FEATURE [App::DocumentObjectGroupPython] H_element106  label="H_element : 15"  # scripted group (container) (typed FeaturePython)
  n = 15
  ref = H_element
FEATURE [App::DocumentObjectGroupPython] O_element099  label="O_element : 053"  # scripted group (container) (typed FeaturePython)
  n = 4
  ref = O_element
FEATURE [App::DocumentObjectGroupPython] P_element012  label="P_element : 1"  # scripted group (container) (typed FeaturePython)
  n = 1
  ref = P_element
FEATURE [App::DocumentObjectGroupPython] G4_TRIETHYL_PHOSPHATE  # scripted group (container) (typed FeaturePython)
  Dunit = g/cm3
  Dvalue = 1.07
  Group = -> [C_element116,H_element106,O_element099,P_element012]
  conduct = 2
  density = 1
  expand = 3
  formula = G4_TRIETHYL_PHOSPHATE
  name = G4_TRIETHYL_PHOSPHATE
  specific = 4
FEATURE [App::DocumentObjectGroupPython] W_element003  label="W_element : 003"  # scripted group (container) (typed FeaturePython)
  n = 1
  ref = W_element
FEATURE [App::DocumentObjectGroupPython] F_element017  label="F_element : 6"  # scripted group (container) (typed FeaturePython)
  n = 6
  ref = F_element
FEATURE [App::DocumentObjectGroupPython] G4_TUNGSTEN_HEXAFLUORIDE  # scripted group (container) (typed FeaturePython)
  Dunit = g/cm3
  Dvalue = 2.4
  Group = -> [W_element003,F_element017]
  conduct = 2
  density = 1
  expand = 3
  formula = G4_TUNGSTEN_HEXAFLUORIDE
  name = G4_TUNGSTEN_HEXAFLUORIDE
  specific = 4
FEATURE [App::DocumentObjectGroupPython] U_element001  label="U_element : 1"  # scripted group (container) (typed FeaturePython)
  n = 1
  ref = U_element
FEATURE [App::DocumentObjectGroupPython] C_element117  label="C_element : 064"  # scripted group (container) (typed FeaturePython)
  n = 2
  ref = C_element
FEATURE [App::DocumentObjectGroupPython] G4_URANIUM_DICARBIDE  # scripted group (container) (typed FeaturePython)
  Dunit = g/cm3
  Dvalue = 11.28
  Group = -> [U_element001,C_element117]
  conduct = 2
  density = 1
  expand = 3
  formula = G4_URANIUM_DICARBIDE
  name = G4_URANIUM_DICARBIDE
  specific = 4
FEATURE [App::DocumentObjectGroupPython] U_element002  label="U_element : 002"  # scripted group (container) (typed FeaturePython)
  n = 1
  ref = U_element
FEATURE [App::DocumentObjectGroupPython] C_element118  label="C_element : 065"  # scripted group (container) (typed FeaturePython)
  n = 1
  ref = C_element
FEATURE [App::DocumentObjectGroupPython] G4_URANIUM_MONOCARBIDE  # scripted group (container) (typed FeaturePython)
  Dunit = g/cm3
  Dvalue = 13.63
  Group = -> [U_element002,C_element118]
  conduct = 2
  density = 1
  expand = 3
  formula = G4_URANIUM_MONOCARBIDE
  name = G4_URANIUM_MONOCARBIDE
  specific = 4
FEATURE [App::DocumentObjectGroupPython] U_element003  label="U_element : 003"  # scripted group (container) (typed FeaturePython)
  n = 1
  ref = U_element
FEATURE [App::DocumentObjectGroupPython] O_element100  label="O_element : 054"  # scripted group (container) (typed FeaturePython)
  n = 2
  ref = O_element
FEATURE [App::DocumentObjectGroupPython] G4_URANIUM_OXIDE  # scripted group (container) (typed FeaturePython)
  Dunit = g/cm3
  Dvalue = 10.96
  Group = -> [U_element003,O_element100]
  conduct = 2
  density = 1
  expand = 3
  formula = G4_URANIUM_OXIDE
  name = G4_URANIUM_OXIDE
  specific = 4
FEATURE [App::DocumentObjectGroupPython] C_element119  label="C_element : 066"  # scripted group (container) (typed FeaturePython)
  n = 1
  ref = C_element
FEATURE [App::DocumentObjectGroupPython] H_element107  label="H_element : 057"  # scripted group (container) (typed FeaturePython)
  n = 4
  ref = H_element
FEATURE [App::DocumentObjectGroupPython] N_element046  label="N_element : 019"  # scripted group (container) (typed FeaturePython)
  n = 2
  ref = N_element
FEATURE [App::DocumentObjectGroupPython] O_element101  label="O_element : 055"  # scripted group (container) (typed FeaturePython)
  n = 1
  ref = O_element
FEATURE [App::DocumentObjectGroupPython] G4_UREA  # scripted group (container) (typed FeaturePython)
  Dunit = g/cm3
  Dvalue = 1.323
  Group = -> [C_element119,H_element107,N_element046,O_element101]
  conduct = 2
  density = 1
  expand = 3
  formula = G4_UREA
  name = G4_UREA
  specific = 4
FEATURE [App::DocumentObjectGroupPython] C_element120  label="C_element : 067"  # scripted group (container) (typed FeaturePython)
  n = 5
  ref = C_element
FEATURE [App::DocumentObjectGroupPython] H_element108  label="H_element : 058"  # scripted group (container) (typed FeaturePython)
  n = 11
  ref = H_element
FEATURE [App::DocumentObjectGroupPython] N_element047  label="N_element : 020"  # scripted group (container) (typed FeaturePython)
  n = 1
  ref = N_element
FEATURE [App::DocumentObjectGroupPython] O_element102  label="O_element : 056"  # scripted group (container) (typed FeaturePython)
  n = 2
  ref = O_element
FEATURE [App::DocumentObjectGroupPython] G4_VALINE  # scripted group (container) (typed FeaturePython)
  Dunit = g/cm3
  Dvalue = 1.23
  Group = -> [C_element120,H_element108,N_element047,O_element102]
  conduct = 2
  density = 1
  expand = 3
  formula = G4_VALINE
  name = G4_VALINE
  specific = 4
FEATURE [App::DocumentObjectGroupPython] H_element109  label="H_element : 0.009"  # scripted group (container) (typed FeaturePython)
  n = 0.009417
FEATURE [App::DocumentObjectGroupPython] C_element121  label="C_element : 0.281"  # scripted group (container) (typed FeaturePython)
  n = 0.280555
FEATURE [App::DocumentObjectGroupPython] F_element018  label="F_element : 0.710"  # scripted group (container) (typed FeaturePython)
  n = 0.710028
FEATURE [App::DocumentObjectGroupPython] G4_VITON  # scripted group (container) (typed FeaturePython)
  Dunit = g/cm3
  Dvalue = 1.8
  Group = -> [H_element109,C_element121,F_element018]
  conduct = 2
  density = 1
  expand = 3
  formula = G4_VITON
  name = G4_VITON
  specific = 4
FEATURE [App::DocumentObjectGroupPython] H_element110  label="H_element : 059"  # scripted group (container) (typed FeaturePython)
  n = 2
  ref = H_element
FEATURE [App::DocumentObjectGroupPython] O_element103  label="O_element : 057"  # scripted group (container) (typed FeaturePython)
  n = 1
  ref = O_element
FEATURE [App::DocumentObjectGroupPython] G4_WATER  # scripted group (container) (typed FeaturePython)
  Dunit = g/cm3
  Dvalue = 1
  Group = -> [H_element110,O_element103]
  conduct = 2
  density = 1
  expand = 3
  formula = G4_WATER
  name = G4_WATER
  specific = 4
FEATURE [App::DocumentObjectGroupPython] H_element111  label="H_element : 060"  # scripted group (container) (typed FeaturePython)
  n = 2
  ref = H_element
FEATURE [App::DocumentObjectGroupPython] O_element104  label="O_element : 058"  # scripted group (container) (typed FeaturePython)
  n = 1
  ref = O_element
FEATURE [App::DocumentObjectGroupPython] G4_WATER_VAPOR  # scripted group (container) (typed FeaturePython)
  Dunit = g/cm3
  Dvalue = 0.000756182
  Group = -> [H_element111,O_element104]
  conduct = 2
  density = 1
  expand = 3
  formula = G4_WATER_VAPOR
  name = G4_WATER_VAPOR
  specific = 4
FEATURE [App::DocumentObjectGroupPython] C_element122  label="C_element : 068"  # scripted group (container) (typed FeaturePython)
  n = 8
  ref = C_element
FEATURE [App::DocumentObjectGroupPython] H_element112  label="H_element : 061"  # scripted group (container) (typed FeaturePython)
  n = 10
  ref = H_element
FEATURE [App::DocumentObjectGroupPython] G4_XYLENE  # scripted group (container) (typed FeaturePython)
  Dunit = g/cm3
  Dvalue = 0.87
  Group = -> [C_element122,H_element112]
  conduct = 2
  density = 1
  expand = 3
  formula = G4_XYLENE
  name = G4_XYLENE
  specific = 4
FEATURE [App::DocumentObjectGroupPython] C_element123  label="C_element : 069"  # scripted group (container) (typed FeaturePython)
  n = 1
  ref = C_element
FEATURE [App::DocumentObjectGroupPython] G4_GRAPHITE  # scripted group (container) (typed FeaturePython)
  Dunit = g/cm3
  Dvalue = 2.21
  Group = -> [C_element123]
  conduct = 2
  density = 1
  expand = 3
  formula = G4_GRAPHITE
  name = G4_GRAPHITE
  specific = 4
FEATURE [App::DocumentObjectGroupPython] NIST  # scripted group (container) (typed FeaturePython)
  Group = -> [G4_A_150_TISSUE,G4_ACETONE,G4_ACETYLENE,G4_ADENINE,G4_ADIPOSE_TISSUE_ICRP,G4_AIR001,G4_ALANINE,G4_ALUMINUM_OXIDE,G4_AMBER,G4_AMMONIA,G4_ANILINE,G4_ANTHRACENE,G4_B_100_BONE,G4_BAKELITE,G4_BARIUM_FLUORIDE,G4_BARIUM_SULFATE,G4_BENZENE,G4_BERYLLIUM_OXIDE,G4_BGO,G4_BLOOD_ICRP,G4_BONE_COMPACT_ICRU,G4_BONE_CORTICAL_ICRP,G4_BORON_CARBIDE,G4_BORON_OXIDE,G4_BRAIN_ICRP,G4_BUTANE,G4_N_BUTYL_ALCOHOL,G4_C_552,+152 more]
FEATURE [App::DocumentObjectGroupPython] H_element113  label="H_element : 062"  # scripted group (container) (typed FeaturePython)
  n = 1
  ref = H_element
FEATURE [App::DocumentObjectGroupPython] G4_H  # scripted group (container) (typed FeaturePython)
  Dunit = g/cm3
  Dvalue = 8.3748e-05
  Group = -> [H_element113]
  conduct = 2
  density = 1
  expand = 3
  formula = H
  name = G4_H
  specific = 4
FEATURE [App::DocumentObjectGroupPython] He_element001  label="He_element : 1"  # scripted group (container) (typed FeaturePython)
  n = 1
  ref = He_element
FEATURE [App::DocumentObjectGroupPython] G4_He  # scripted group (container) (typed FeaturePython)
  Dunit = g/cm3
  Dvalue = 0.000166322
  Group = -> [He_element001]
  conduct = 2
  density = 1
  expand = 3
  formula = He
  name = G4_He
  specific = 4
FEATURE [App::DocumentObjectGroupPython] Li_element008  label="Li_element : 008"  # scripted group (container) (typed FeaturePython)
  n = 1
  ref = Li_element
FEATURE [App::DocumentObjectGroupPython] G4_Li  # scripted group (container) (typed FeaturePython)
  Dunit = g/cm3
  Dvalue = 0.534
  Group = -> [Li_element008]
  conduct = 2
  density = 1
  expand = 3
  formula = Li
  name = G4_Li
  specific = 4
FEATURE [App::DocumentObjectGroupPython] Be_element002  label="Be_element : 002"  # scripted group (container) (typed FeaturePython)
  n = 1
  ref = Be_element
FEATURE [App::DocumentObjectGroupPython] G4_Be  # scripted group (container) (typed FeaturePython)
  Dunit = g/cm3
  Dvalue = 1.848
  Group = -> [Be_element002]
  conduct = 2
  density = 1
  expand = 3
  formula = Be
  name = G4_Be
  specific = 4
FEATURE [App::DocumentObjectGroupPython] B_element007  label="B_element : 007"  # scripted group (container) (typed FeaturePython)
  n = 1
  ref = B_element
FEATURE [App::DocumentObjectGroupPython] G4_B  # scripted group (container) (typed FeaturePython)
  Dunit = g/cm3
  Dvalue = 2.37
  Group = -> [B_element007]
  conduct = 2
  density = 1
  expand = 3
  formula = B
  name = G4_B
  specific = 4
FEATURE [App::DocumentObjectGroupPython] C_element124  label="C_element : 070"  # scripted group (container) (typed FeaturePython)
  n = 1
  ref = C_element
FEATURE [App::DocumentObjectGroupPython] G4_C  # scripted group (container) (typed FeaturePython)
  Dunit = g/cm3
  Dvalue = 2
  Group = -> [C_element124]
  conduct = 2
  density = 1
  expand = 3
  formula = C
  name = G4_C
  specific = 4
FEATURE [App::DocumentObjectGroupPython] N_element048  label="N_element : 021"  # scripted group (container) (typed FeaturePython)
  n = 1
  ref = N_element
FEATURE [App::DocumentObjectGroupPython] G4_N  # scripted group (container) (typed FeaturePython)
  Dunit = g/cm3
  Dvalue = 0.0011652
  Group = -> [N_element048]
  conduct = 2
  density = 1
  expand = 3
  formula = N
  name = G4_N
  specific = 4
FEATURE [App::DocumentObjectGroupPython] O_element105  label="O_element : 059"  # scripted group (container) (typed FeaturePython)
  n = 1
  ref = O_element
FEATURE [App::DocumentObjectGroupPython] G4_O  # scripted group (container) (typed FeaturePython)
  Dunit = g/cm3
  Dvalue = 0.00133151
  Group = -> [O_element105]
  conduct = 2
  density = 1
  expand = 3
  formula = O
  name = G4_O
  specific = 4
FEATURE [App::DocumentObjectGroupPython] F_element019  label="F_element : 008"  # scripted group (container) (typed FeaturePython)
  n = 1
  ref = F_element
FEATURE [App::DocumentObjectGroupPython] G4_F  # scripted group (container) (typed FeaturePython)
  Dunit = g/cm3
  Dvalue = 0.00158029
  Group = -> [F_element019]
  conduct = 2
  density = 1
  expand = 3
  formula = F
  name = G4_F
  specific = 4
FEATURE [App::DocumentObjectGroupPython] Ne_element001  label="Ne_element : 1"  # scripted group (container) (typed FeaturePython)
  n = 1
  ref = Ne_element
FEATURE [App::DocumentObjectGroupPython] G4_Ne  # scripted group (container) (typed FeaturePython)
  Dunit = g/cm3
  Dvalue = 0.000838505
  Group = -> [Ne_element001]
  conduct = 2
  density = 1
  expand = 3
  formula = Ne
  name = G4_Ne
  specific = 4
FEATURE [App::DocumentObjectGroupPython] Na_element020  label="Na_element : 005"  # scripted group (container) (typed FeaturePython)
  n = 1
  ref = Na_element
FEATURE [App::DocumentObjectGroupPython] G4_Na  # scripted group (container) (typed FeaturePython)
  Dunit = g/cm3
  Dvalue = 0.971
  Group = -> [Na_element020]
  conduct = 2
  density = 1
  expand = 3
  formula = Na
  name = G4_Na
  specific = 4
FEATURE [App::DocumentObjectGroupPython] Mg_element011  label="Mg_element : 005"  # scripted group (container) (typed FeaturePython)
  n = 1
  ref = Mg_element
FEATURE [App::DocumentObjectGroupPython] G4_Mg  # scripted group (container) (typed FeaturePython)
  Dunit = g/cm3
  Dvalue = 1.74
  Group = -> [Mg_element011]
  conduct = 2
  density = 1
  expand = 3
  formula = Mg
  name = G4_Mg
  specific = 4
FEATURE [App::DocumentObjectGroupPython] Al_element004  label="Al_element : 1"  # scripted group (container) (typed FeaturePython)
  n = 1
  ref = Al_element
FEATURE [App::DocumentObjectGroupPython] G4_Al  # scripted group (container) (typed FeaturePython)
  Dunit = g/cm3
  Dvalue = 2.699
  Group = -> [Al_element004]
  conduct = 2
  density = 1
  expand = 3
  formula = Al
  name = G4_Al
  specific = 4
FEATURE [App::DocumentObjectGroupPython] Si_element007  label="Si_element : 002"  # scripted group (container) (typed FeaturePython)
  n = 1
  ref = Si_element
FEATURE [App::DocumentObjectGroupPython] G4_Si  # scripted group (container) (typed FeaturePython)
  Dunit = g/cm3
  Dvalue = 2.33
  Group = -> [Si_element007]
  conduct = 2
  density = 1
  expand = 3
  formula = Si
  name = G4_Si
  specific = 4
FEATURE [App::DocumentObjectGroupPython] P_element013  label="P_element : 002"  # scripted group (container) (typed FeaturePython)
  n = 1
  ref = P_element
FEATURE [App::DocumentObjectGroupPython] G4_P  # scripted group (container) (typed FeaturePython)
  Dunit = g/cm3
  Dvalue = 2.2
  Group = -> [P_element013]
  conduct = 2
  density = 1
  expand = 3
  formula = P
  name = G4_P
  specific = 4
FEATURE [App::DocumentObjectGroupPython] S_element023  label="S_element : 007"  # scripted group (container) (typed FeaturePython)
  n = 1
  ref = S_element
FEATURE [App::DocumentObjectGroupPython] G4_S  # scripted group (container) (typed FeaturePython)
  Dunit = g/cm3
  Dvalue = 2
  Group = -> [S_element023]
  conduct = 2
  density = 1
  expand = 3
  formula = S
  name = G4_S
  specific = 4
FEATURE [App::DocumentObjectGroupPython] Cl_element029  label="Cl_element : 015"  # scripted group (container) (typed FeaturePython)
  n = 1
  ref = Cl_element
FEATURE [App::DocumentObjectGroupPython] G4_Cl  # scripted group (container) (typed FeaturePython)
  Dunit = g/cm3
  Dvalue = 0.00299473
  Group = -> [Cl_element029]
  conduct = 2
  density = 1
  expand = 3
  formula = Cl
  name = G4_Cl
  specific = 4
FEATURE [App::DocumentObjectGroupPython] Ar_element002  label="Ar_element : 1"  # scripted group (container) (typed FeaturePython)
  n = 1
  ref = Ar_element
FEATURE [App::DocumentObjectGroupPython] G4_Ar  # scripted group (container) (typed FeaturePython)
  Dunit = g/cm3
  Dvalue = 0.00166201
  Group = -> [Ar_element002]
  conduct = 2
  density = 1
  expand = 3
  formula = Ar
  name = G4_Ar
  specific = 4
FEATURE [App::DocumentObjectGroupPython] K_element013  label="K_element : 003"  # scripted group (container) (typed FeaturePython)
  n = 1
  ref = K_element
FEATURE [App::DocumentObjectGroupPython] G4_K  # scripted group (container) (typed FeaturePython)
  Dunit = g/cm3
  Dvalue = 0.862
  Group = -> [K_element013]
  conduct = 2
  density = 1
  expand = 3
  formula = K
  name = G4_K
  specific = 4
FEATURE [App::DocumentObjectGroupPython] Ca_element014  label="Ca_element : 007"  # scripted group (container) (typed FeaturePython)
  n = 1
  ref = Ca_element
FEATURE [App::DocumentObjectGroupPython] G4_Ca  # scripted group (container) (typed FeaturePython)
  Dunit = g/cm3
  Dvalue = 1.55
  Group = -> [Ca_element014]
  conduct = 2
  density = 1
  expand = 3
  formula = Ca
  name = G4_Ca
  specific = 4
FEATURE [App::DocumentObjectGroupPython] Sc_element001  label="Sc_element : 1"  # scripted group (container) (typed FeaturePython)
  n = 1
  ref = Sc_element
FEATURE [App::DocumentObjectGroupPython] G4_Sc  # scripted group (container) (typed FeaturePython)
  Dunit = g/cm3
  Dvalue = 2.989
  Group = -> [Sc_element001]
  conduct = 2
  density = 1
  expand = 3
  formula = Sc
  name = G4_Sc
  specific = 4
FEATURE [App::DocumentObjectGroupPython] Ti_element004  label="Ti_element : 002"  # scripted group (container) (typed FeaturePython)
  n = 1
  ref = Ti_element
FEATURE [App::DocumentObjectGroupPython] G4_Ti  # scripted group (container) (typed FeaturePython)
  Dunit = g/cm3
  Dvalue = 4.54
  Group = -> [Ti_element004]
  conduct = 2
  density = 1
  expand = 3
  formula = Ti
  name = G4_Ti
  specific = 4
FEATURE [App::DocumentObjectGroupPython] V_element001  label="V_element : 1"  # scripted group (container) (typed FeaturePython)
  n = 1
  ref = V_element
FEATURE [App::DocumentObjectGroupPython] G4_V  # scripted group (container) (typed FeaturePython)
  Dunit = g/cm3
  Dvalue = 6.11
  Group = -> [V_element001]
  conduct = 2
  density = 1
  expand = 3
  formula = V
  name = G4_V
  specific = 4
FEATURE [App::DocumentObjectGroupPython] Cr_element001  label="Cr_element : 1"  # scripted group (container) (typed FeaturePython)
  n = 1
  ref = Cr_element
FEATURE [App::DocumentObjectGroupPython] G4_Cr  # scripted group (container) (typed FeaturePython)
  Dunit = g/cm3
  Dvalue = 7.18
  Group = -> [Cr_element001]
  conduct = 2
  density = 1
  expand = 3
  formula = Cr
  name = G4_Cr
  specific = 4
FEATURE [App::DocumentObjectGroupPython] Mn_element001  label="Mn_element : 1"  # scripted group (container) (typed FeaturePython)
  n = 1
  ref = Mn_element
FEATURE [App::DocumentObjectGroupPython] G4_Mn  # scripted group (container) (typed FeaturePython)
  Dunit = g/cm3
  Dvalue = 7.44
  Group = -> [Mn_element001]
  conduct = 2
  density = 1
  expand = 3
  formula = Mn
  name = G4_Mn
  specific = 4
FEATURE [App::DocumentObjectGroupPython] Fe_element007  label="Fe_element : 004"  # scripted group (container) (typed FeaturePython)
  n = 1
  ref = Fe_element
FEATURE [App::DocumentObjectGroupPython] G4_Fe  # scripted group (container) (typed FeaturePython)
  Dunit = g/cm3
  Dvalue = 7.874
  Group = -> [Fe_element007]
  conduct = 2
  density = 1
  expand = 3
  formula = Fe
  name = G4_Fe
  specific = 4
FEATURE [App::DocumentObjectGroupPython] Co_element001  label="Co_element : 1"  # scripted group (container) (typed FeaturePython)
  n = 1
  ref = Co_element
FEATURE [App::DocumentObjectGroupPython] G4_Co  # scripted group (container) (typed FeaturePython)
  Dunit = g/cm3
  Dvalue = 8.9
  Group = -> [Co_element001]
  conduct = 2
  density = 1
  expand = 3
  formula = Co
  name = G4_Co
  specific = 4
FEATURE [App::DocumentObjectGroupPython] Ni_element001  label="Ni_element : 1"  # scripted group (container) (typed FeaturePython)
  n = 1
  ref = Ni_element
FEATURE [App::DocumentObjectGroupPython] G4_Ni  # scripted group (container) (typed FeaturePython)
  Dunit = g/cm3
  Dvalue = 8.902
  Group = -> [Ni_element001]
  conduct = 2
  density = 1
  expand = 3
  formula = Ni
  name = G4_Ni
  specific = 4
FEATURE [App::DocumentObjectGroupPython] Cu_element001  label="Cu_element : 1"  # scripted group (container) (typed FeaturePython)
  n = 1
  ref = Cu_element
FEATURE [App::DocumentObjectGroupPython] G4_Cu  # scripted group (container) (typed FeaturePython)
  Dunit = g/cm3
  Dvalue = 8.96
  Group = -> [Cu_element001]
  conduct = 2
  density = 1
  expand = 3
  formula = Cu
  name = G4_Cu
  specific = 4
FEATURE [App::DocumentObjectGroupPython] Zn_element001  label="Zn_element : 1"  # scripted group (container) (typed FeaturePython)
  n = 1
  ref = Zn_element
FEATURE [App::DocumentObjectGroupPython] G4_Zn  # scripted group (container) (typed FeaturePython)
  Dunit = g/cm3
  Dvalue = 7.133
  Group = -> [Zn_element001]
  conduct = 2
  density = 1
  expand = 3
  formula = Zn
  name = G4_Zn
  specific = 4
FEATURE [App::DocumentObjectGroupPython] Ga_element002  label="Ga_element : 002"  # scripted group (container) (typed FeaturePython)
  n = 1
  ref = Ga_element
FEATURE [App::DocumentObjectGroupPython] G4_Ga  # scripted group (container) (typed FeaturePython)
  Dunit = g/cm3
  Dvalue = 5.904
  Group = -> [Ga_element002]
  conduct = 2
  density = 1
  expand = 3
  formula = Ga
  name = G4_Ga
  specific = 4
FEATURE [App::DocumentObjectGroupPython] Ge_element002  label="Ge_element : 1"  # scripted group (container) (typed FeaturePython)
  n = 1
  ref = Ge_element
FEATURE [App::DocumentObjectGroupPython] G4_Ge  # scripted group (container) (typed FeaturePython)
  Dunit = g/cm3
  Dvalue = 5.323
  Group = -> [Ge_element002]
  conduct = 2
  density = 1
  expand = 3
  formula = Ge
  name = G4_Ge
  specific = 4
FEATURE [App::DocumentObjectGroupPython] As_element003  label="As_element : 002"  # scripted group (container) (typed FeaturePython)
  n = 1
  ref = As_element
FEATURE [App::DocumentObjectGroupPython] G4_As  # scripted group (container) (typed FeaturePython)
  Dunit = g/cm3
  Dvalue = 5.73
  Group = -> [As_element003]
  conduct = 2
  density = 1
  expand = 3
  formula = As
  name = G4_As
  specific = 4
FEATURE [App::DocumentObjectGroupPython] Se_element001  label="Se_element : 1"  # scripted group (container) (typed FeaturePython)
  n = 1
  ref = Se_element
FEATURE [App::DocumentObjectGroupPython] G4_Se  # scripted group (container) (typed FeaturePython)
  Dunit = g/cm3
  Dvalue = 4.5
  Group = -> [Se_element001]
  conduct = 2
  density = 1
  expand = 3
  formula = Se
  name = G4_Se
  specific = 4
FEATURE [App::DocumentObjectGroupPython] Br_element007  label="Br_element : 004"  # scripted group (container) (typed FeaturePython)
  n = 1
  ref = Br_element
FEATURE [App::DocumentObjectGroupPython] G4_Br  # scripted group (container) (typed FeaturePython)
  Dunit = g/cm3
  Dvalue = 0.0070721
  Group = -> [Br_element007]
  conduct = 2
  density = 1
  expand = 3
  formula = Br
  name = G4_Br
  specific = 4
FEATURE [App::DocumentObjectGroupPython] Kr_element001  label="Kr_element : 1"  # scripted group (container) (typed FeaturePython)
  n = 1
  ref = Kr_element
FEATURE [App::DocumentObjectGroupPython] G4_Kr  # scripted group (container) (typed FeaturePython)
  Dunit = g/cm3
  Dvalue = 0.00347832
  Group = -> [Kr_element001]
  conduct = 2
  density = 1
  expand = 3
  formula = Kr
  name = G4_Kr
  specific = 4
FEATURE [App::DocumentObjectGroupPython] Rb_element001  label="Rb_element : 1"  # scripted group (container) (typed FeaturePython)
  n = 1
  ref = Rb_element
FEATURE [App::DocumentObjectGroupPython] G4_Rb  # scripted group (container) (typed FeaturePython)
  Dunit = g/cm3
  Dvalue = 1.532
  Group = -> [Rb_element001]
  conduct = 2
  density = 1
  expand = 3
  formula = Rb
  name = G4_Rb
  specific = 4
FEATURE [App::DocumentObjectGroupPython] Sr_element001  label="Sr_element : 1"  # scripted group (container) (typed FeaturePython)
  n = 1
  ref = Sr_element
FEATURE [App::DocumentObjectGroupPython] G4_Sr  # scripted group (container) (typed FeaturePython)
  Dunit = g/cm3
  Dvalue = 2.54
  Group = -> [Sr_element001]
  conduct = 2
  density = 1
  expand = 3
  formula = Sr
  name = G4_Sr
  specific = 4
FEATURE [App::DocumentObjectGroupPython] Y_element001  label="Y_element : 1"  # scripted group (container) (typed FeaturePython)
  n = 1
  ref = Y_element
FEATURE [App::DocumentObjectGroupPython] G4_Y  # scripted group (container) (typed FeaturePython)
  Dunit = g/cm3
  Dvalue = 4.469
  Group = -> [Y_element001]
  conduct = 2
  density = 1
  expand = 3
  formula = Y
  name = G4_Y
  specific = 4
FEATURE [App::DocumentObjectGroupPython] Zr_element001  label="Zr_element : 1"  # scripted group (container) (typed FeaturePython)
  n = 1
  ref = Zr_element
FEATURE [App::DocumentObjectGroupPython] G4_Zr  # scripted group (container) (typed FeaturePython)
  Dunit = g/cm3
  Dvalue = 6.506
  Group = -> [Zr_element001]
  conduct = 2
  density = 1
  expand = 3
  formula = Zr
  name = G4_Zr
  specific = 4
FEATURE [App::DocumentObjectGroupPython] Nb_element001  label="Nb_element : 1"  # scripted group (container) (typed FeaturePython)
  n = 1
  ref = Nb_element
FEATURE [App::DocumentObjectGroupPython] G4_Nb  # scripted group (container) (typed FeaturePython)
  Dunit = g/cm3
  Dvalue = 8.57
  Group = -> [Nb_element001]
  conduct = 2
  density = 1
  expand = 3
  formula = Nb
  name = G4_Nb
  specific = 4
FEATURE [App::DocumentObjectGroupPython] Mo_element001  label="Mo_element : 1"  # scripted group (container) (typed FeaturePython)
  n = 1
  ref = Mo_element
FEATURE [App::DocumentObjectGroupPython] G4_Mo  # scripted group (container) (typed FeaturePython)
  Dunit = g/cm3
  Dvalue = 10.22
  Group = -> [Mo_element001]
  conduct = 2
  density = 1
  expand = 3
  formula = Mo
  name = G4_Mo
  specific = 4
FEATURE [App::DocumentObjectGroupPython] Tc_element001  label="Tc_element : 1"  # scripted group (container) (typed FeaturePython)
  n = 1
  ref = Tc_element
FEATURE [App::DocumentObjectGroupPython] G4_Tc  # scripted group (container) (typed FeaturePython)
  Dunit = g/cm3
  Dvalue = 11.5
  Group = -> [Tc_element001]
  conduct = 2
  density = 1
  expand = 3
  formula = Tc
  name = G4_Tc
  specific = 4
FEATURE [App::DocumentObjectGroupPython] Ru_element001  label="Ru_element : 1"  # scripted group (container) (typed FeaturePython)
  n = 1
  ref = Ru_element
FEATURE [App::DocumentObjectGroupPython] G4_Ru  # scripted group (container) (typed FeaturePython)
  Dunit = g/cm3
  Dvalue = 12.41
  Group = -> [Ru_element001]
  conduct = 2
  density = 1
  expand = 3
  formula = Ru
  name = G4_Ru
  specific = 4
FEATURE [App::DocumentObjectGroupPython] Rh_element001  label="Rh_element : 1"  # scripted group (container) (typed FeaturePython)
  n = 1
  ref = Rh_element
FEATURE [App::DocumentObjectGroupPython] G4_Rh  # scripted group (container) (typed FeaturePython)
  Dunit = g/cm3
  Dvalue = 12.41
  Group = -> [Rh_element001]
  conduct = 2
  density = 1
  expand = 3
  formula = Rh
  name = G4_Rh
  specific = 4
FEATURE [App::DocumentObjectGroupPython] Pd_element001  label="Pd_element : 1"  # scripted group (container) (typed FeaturePython)
  n = 1
  ref = Pd_element
FEATURE [App::DocumentObjectGroupPython] G4_Pd  # scripted group (container) (typed FeaturePython)
  Dunit = g/cm3
  Dvalue = 12.02
  Group = -> [Pd_element001]
  conduct = 2
  density = 1
  expand = 3
  formula = Pd
  name = G4_Pd
  specific = 4
FEATURE [App::DocumentObjectGroupPython] Ag_element006  label="Ag_element : 004"  # scripted group (container) (typed FeaturePython)
  n = 1
  ref = Ag_element
FEATURE [App::DocumentObjectGroupPython] G4_Ag  # scripted group (container) (typed FeaturePython)
  Dunit = g/cm3
  Dvalue = 10.5
  Group = -> [Ag_element006]
  conduct = 2
  density = 1
  expand = 3
  formula = Ag
  name = G4_Ag
  specific = 4
FEATURE [App::DocumentObjectGroupPython] Cd_element003  label="Cd_element : 003"  # scripted group (container) (typed FeaturePython)
  n = 1
  ref = Cd_element
FEATURE [App::DocumentObjectGroupPython] G4_Cd  # scripted group (container) (typed FeaturePython)
  Dunit = g/cm3
  Dvalue = 8.65
  Group = -> [Cd_element003]
  conduct = 2
  density = 1
  expand = 3
  formula = Cd
  name = G4_Cd
  specific = 4
FEATURE [App::DocumentObjectGroupPython] In_element001  label="In_element : 1"  # scripted group (container) (typed FeaturePython)
  n = 1
  ref = In_element
FEATURE [App::DocumentObjectGroupPython] G4_In  # scripted group (container) (typed FeaturePython)
  Dunit = g/cm3
  Dvalue = 7.31
  Group = -> [In_element001]
  conduct = 2
  density = 1
  expand = 3
  formula = In
  name = G4_In
  specific = 4
FEATURE [App::DocumentObjectGroupPython] Sn_element001  label="Sn_element : 1"  # scripted group (container) (typed FeaturePython)
  n = 1
  ref = Sn_element
FEATURE [App::DocumentObjectGroupPython] G4_Sn  # scripted group (container) (typed FeaturePython)
  Dunit = g/cm3
  Dvalue = 7.31
  Group = -> [Sn_element001]
  conduct = 2
  density = 1
  expand = 3
  formula = Sn
  name = G4_Sn
  specific = 4
FEATURE [App::DocumentObjectGroupPython] Sb_element001  label="Sb_element : 1"  # scripted group (container) (typed FeaturePython)
  n = 1
  ref = Sb_element
FEATURE [App::DocumentObjectGroupPython] G4_Sb  # scripted group (container) (typed FeaturePython)
  Dunit = g/cm3
  Dvalue = 6.691
  Group = -> [Sb_element001]
  conduct = 2
  density = 1
  expand = 3
  formula = Sb
  name = G4_Sb
  specific = 4
FEATURE [App::DocumentObjectGroupPython] Te_element002  label="Te_element : 002"  # scripted group (container) (typed FeaturePython)
  n = 1
  ref = Te_element
FEATURE [App::DocumentObjectGroupPython] G4_Te  # scripted group (container) (typed FeaturePython)
  Dunit = g/cm3
  Dvalue = 6.24
  Group = -> [Te_element002]
  conduct = 2
  density = 1
  expand = 3
  formula = Te
  name = G4_Te
  specific = 4
FEATURE [App::DocumentObjectGroupPython] I_element010  label="I_element : 006"  # scripted group (container) (typed FeaturePython)
  n = 1
  ref = I_element
FEATURE [App::DocumentObjectGroupPython] G4_I  # scripted group (container) (typed FeaturePython)
  Dunit = g/cm3
  Dvalue = 4.93
  Group = -> [I_element010]
  conduct = 2
  density = 1
  expand = 3
  formula = I
  name = G4_I
  specific = 4
FEATURE [App::DocumentObjectGroupPython] Xe_element001  label="Xe_element : 1"  # scripted group (container) (typed FeaturePython)
  n = 1
  ref = Xe_element
FEATURE [App::DocumentObjectGroupPython] G4_Xe  # scripted group (container) (typed FeaturePython)
  Dunit = g/cm3
  Dvalue = 0.00548536
  Group = -> [Xe_element001]
  conduct = 2
  density = 1
  expand = 3
  formula = Xe
  name = G4_Xe
  specific = 4
FEATURE [App::DocumentObjectGroupPython] Cs_element003  label="Cs_element : 003"  # scripted group (container) (typed FeaturePython)
  n = 1
  ref = Cs_element
FEATURE [App::DocumentObjectGroupPython] G4_Cs  # scripted group (container) (typed FeaturePython)
  Dunit = g/cm3
  Dvalue = 1.873
  Group = -> [Cs_element003]
  conduct = 2
  density = 1
  expand = 3
  formula = Cs
  name = G4_Cs
  specific = 4
FEATURE [App::DocumentObjectGroupPython] Ba_element003  label="Ba_element : 003"  # scripted group (container) (typed FeaturePython)
  n = 1
  ref = Ba_element
FEATURE [App::DocumentObjectGroupPython] G4_Ba  # scripted group (container) (typed FeaturePython)
  Dunit = g/cm3
  Dvalue = 3.5
  Group = -> [Ba_element003]
  conduct = 2
  density = 1
  expand = 3
  formula = Ba
  name = G4_Ba
  specific = 4
FEATURE [App::DocumentObjectGroupPython] La_element003  label="La_element : 003"  # scripted group (container) (typed FeaturePython)
  n = 1
  ref = La_element
FEATURE [App::DocumentObjectGroupPython] G4_La  # scripted group (container) (typed FeaturePython)
  Dunit = g/cm3
  Dvalue = 6.154
  Group = -> [La_element003]
  conduct = 2
  density = 1
  expand = 3
  formula = La
  name = G4_La
  specific = 4
FEATURE [App::DocumentObjectGroupPython] Ce_element002  label="Ce_element : 1"  # scripted group (container) (typed FeaturePython)
  n = 1
  ref = Ce_element
FEATURE [App::DocumentObjectGroupPython] G4_Ce  # scripted group (container) (typed FeaturePython)
  Dunit = g/cm3
  Dvalue = 6.657
  Group = -> [Ce_element002]
  conduct = 2
  density = 1
  expand = 3
  formula = Ce
  name = G4_Ce
  specific = 4
FEATURE [App::DocumentObjectGroupPython] Pr_element001  label="Pr_element : 1"  # scripted group (container) (typed FeaturePython)
  n = 1
  ref = Pr_element
FEATURE [App::DocumentObjectGroupPython] G4_Pr  # scripted group (container) (typed FeaturePython)
  Dunit = g/cm3
  Dvalue = 6.71
  Group = -> [Pr_element001]
  conduct = 2
  density = 1
  expand = 3
  formula = Pr
  name = G4_Pr
  specific = 4
FEATURE [App::DocumentObjectGroupPython] Nd_element001  label="Nd_element : 1"  # scripted group (container) (typed FeaturePython)
  n = 1
  ref = Nd_element
FEATURE [App::DocumentObjectGroupPython] G4_Nd  # scripted group (container) (typed FeaturePython)
  Dunit = g/cm3
  Dvalue = 6.9
  Group = -> [Nd_element001]
  conduct = 2
  density = 1
  expand = 3
  formula = Nd
  name = G4_Nd
  specific = 4
FEATURE [App::DocumentObjectGroupPython] Pm_element001  label="Pm_element : 1"  # scripted group (container) (typed FeaturePython)
  n = 1
  ref = Pm_element
FEATURE [App::DocumentObjectGroupPython] G4_Pm  # scripted group (container) (typed FeaturePython)
  Dunit = g/cm3
  Dvalue = 7.22
  Group = -> [Pm_element001]
  conduct = 2
  density = 1
  expand = 3
  formula = Pm
  name = G4_Pm
  specific = 4
FEATURE [App::DocumentObjectGroupPython] Sm_element001  label="Sm_element : 1"  # scripted group (container) (typed FeaturePython)
  n = 1
  ref = Sm_element
FEATURE [App::DocumentObjectGroupPython] G4_Sm  # scripted group (container) (typed FeaturePython)
  Dunit = g/cm3
  Dvalue = 7.46
  Group = -> [Sm_element001]
  conduct = 2
  density = 1
  expand = 3
  formula = Sm
  name = G4_Sm
  specific = 4
FEATURE [App::DocumentObjectGroupPython] Eu_element001  label="Eu_element : 1"  # scripted group (container) (typed FeaturePython)
  n = 1
  ref = Eu_element
FEATURE [App::DocumentObjectGroupPython] G4_Eu  # scripted group (container) (typed FeaturePython)
  Dunit = g/cm3
  Dvalue = 5.243
  Group = -> [Eu_element001]
  conduct = 2
  density = 1
  expand = 3
  formula = Eu
  name = G4_Eu
  specific = 4
FEATURE [App::DocumentObjectGroupPython] Gd_element002  label="Gd_element : 1"  # scripted group (container) (typed FeaturePython)
  n = 1
  ref = Gd_element
FEATURE [App::DocumentObjectGroupPython] G4_Gd  # scripted group (container) (typed FeaturePython)
  Dunit = g/cm3
  Dvalue = 7.9004
  Group = -> [Gd_element002]
  conduct = 2
  density = 1
  expand = 3
  formula = Gd
  name = G4_Gd
  specific = 4
FEATURE [App::DocumentObjectGroupPython] Tb_element001  label="Tb_element : 1"  # scripted group (container) (typed FeaturePython)
  n = 1
  ref = Tb_element
FEATURE [App::DocumentObjectGroupPython] G4_Tb  # scripted group (container) (typed FeaturePython)
  Dunit = g/cm3
  Dvalue = 8.229
  Group = -> [Tb_element001]
  conduct = 2
  density = 1
  expand = 3
  formula = Tb
  name = G4_Tb
  specific = 4
FEATURE [App::DocumentObjectGroupPython] Dy_element001  label="Dy_element : 1"  # scripted group (container) (typed FeaturePython)
  n = 1
  ref = Dy_element
FEATURE [App::DocumentObjectGroupPython] G4_Dy  # scripted group (container) (typed FeaturePython)
  Dunit = g/cm3
  Dvalue = 8.55
  Group = -> [Dy_element001]
  conduct = 2
  density = 1
  expand = 3
  formula = Dy
  name = G4_Dy
  specific = 4
FEATURE [App::DocumentObjectGroupPython] Ho_element001  label="Ho_element : 1"  # scripted group (container) (typed FeaturePython)
  n = 1
  ref = Ho_element
FEATURE [App::DocumentObjectGroupPython] G4_Ho  # scripted group (container) (typed FeaturePython)
  Dunit = g/cm3
  Dvalue = 8.795
  Group = -> [Ho_element001]
  conduct = 2
  density = 1
  expand = 3
  formula = Ho
  name = G4_Ho
  specific = 4
FEATURE [App::DocumentObjectGroupPython] Er_element001  label="Er_element : 1"  # scripted group (container) (typed FeaturePython)
  n = 1
  ref = Er_element
FEATURE [App::DocumentObjectGroupPython] G4_Er  # scripted group (container) (typed FeaturePython)
  Dunit = g/cm3
  Dvalue = 9.066
  Group = -> [Er_element001]
  conduct = 2
  density = 1
  expand = 3
  formula = Er
  name = G4_Er
  specific = 4
FEATURE [App::DocumentObjectGroupPython] Tm_element001  label="Tm_element : 1"  # scripted group (container) (typed FeaturePython)
  n = 1
  ref = Tm_element
FEATURE [App::DocumentObjectGroupPython] G4_Tm  # scripted group (container) (typed FeaturePython)
  Dunit = g/cm3
  Dvalue = 9.321
  Group = -> [Tm_element001]
  conduct = 2
  density = 1
  expand = 3
  formula = Tm
  name = G4_Tm
  specific = 4
FEATURE [App::DocumentObjectGroupPython] Yb_element001  label="Yb_element : 1"  # scripted group (container) (typed FeaturePython)
  n = 1
  ref = Yb_element
FEATURE [App::DocumentObjectGroupPython] G4_Yb  # scripted group (container) (typed FeaturePython)
  Dunit = g/cm3
  Dvalue = 6.73
  Group = -> [Yb_element001]
  conduct = 2
  density = 1
  expand = 3
  formula = Yb
  name = G4_Yb
  specific = 4
FEATURE [App::DocumentObjectGroupPython] Lu_element001  label="Lu_element : 1"  # scripted group (container) (typed FeaturePython)
  n = 1
  ref = Lu_element
FEATURE [App::DocumentObjectGroupPython] G4_Lu  # scripted group (container) (typed FeaturePython)
  Dunit = g/cm3
  Dvalue = 9.84
  Group = -> [Lu_element001]
  conduct = 2
  density = 1
  expand = 3
  formula = Lu
  name = G4_Lu
  specific = 4
FEATURE [App::DocumentObjectGroupPython] Hf_element001  label="Hf_element : 1"  # scripted group (container) (typed FeaturePython)
  n = 1
  ref = Hf_element
FEATURE [App::DocumentObjectGroupPython] G4_Hf  # scripted group (container) (typed FeaturePython)
  Dunit = g/cm3
  Dvalue = 13.31
  Group = -> [Hf_element001]
  conduct = 2
  density = 1
  expand = 3
  formula = Hf
  name = G4_Hf
  specific = 4
FEATURE [App::DocumentObjectGroupPython] Ta_element001  label="Ta_element : 1"  # scripted group (container) (typed FeaturePython)
  n = 1
  ref = Ta_element
FEATURE [App::DocumentObjectGroupPython] G4_Ta  # scripted group (container) (typed FeaturePython)
  Dunit = g/cm3
  Dvalue = 16.654
  Group = -> [Ta_element001]
  conduct = 2
  density = 1
  expand = 3
  formula = Ta
  name = G4_Ta
  specific = 4
FEATURE [App::DocumentObjectGroupPython] W_element004  label="W_element : 004"  # scripted group (container) (typed FeaturePython)
  n = 1
  ref = W_element
FEATURE [App::DocumentObjectGroupPython] G4_W  # scripted group (container) (typed FeaturePython)
  Dunit = g/cm3
  Dvalue = 19.3
  Group = -> [W_element004]
  conduct = 2
  density = 1
  expand = 3
  formula = W
  name = G4_W
  specific = 4
FEATURE [App::DocumentObjectGroupPython] Re_element001  label="Re_element : 1"  # scripted group (container) (typed FeaturePython)
  n = 1
  ref = Re_element
FEATURE [App::DocumentObjectGroupPython] G4_Re  # scripted group (container) (typed FeaturePython)
  Dunit = g/cm3
  Dvalue = 21.02
  Group = -> [Re_element001]
  conduct = 2
  density = 1
  expand = 3
  formula = Re
  name = G4_Re
  specific = 4
FEATURE [App::DocumentObjectGroupPython] Os_element001  label="Os_element : 1"  # scripted group (container) (typed FeaturePython)
  n = 1
  ref = Os_element
FEATURE [App::DocumentObjectGroupPython] G4_Os  # scripted group (container) (typed FeaturePython)
  Dunit = g/cm3
  Dvalue = 22.57
  Group = -> [Os_element001]
  conduct = 2
  density = 1
  expand = 3
  formula = Os
  name = G4_Os
  specific = 4
FEATURE [App::DocumentObjectGroupPython] Ir_element001  label="Ir_element : 1"  # scripted group (container) (typed FeaturePython)
  n = 1
  ref = Ir_element
FEATURE [App::DocumentObjectGroupPython] G4_Ir  # scripted group (container) (typed FeaturePython)
  Dunit = g/cm3
  Dvalue = 22.42
  Group = -> [Ir_element001]
  conduct = 2
  density = 1
  expand = 3
  formula = Ir
  name = G4_Ir
  specific = 4
FEATURE [App::DocumentObjectGroupPython] Pt_element001  label="Pt_element : 1"  # scripted group (container) (typed FeaturePython)
  n = 1
  ref = Pt_element
FEATURE [App::DocumentObjectGroupPython] G4_Pt  # scripted group (container) (typed FeaturePython)
  Dunit = g/cm3
  Dvalue = 21.45
  Group = -> [Pt_element001]
  conduct = 2
  density = 1
  expand = 3
  formula = Pt
  name = G4_Pt
  specific = 4
FEATURE [App::DocumentObjectGroupPython] Au_element001  label="Au_element : 1"  # scripted group (container) (typed FeaturePython)
  n = 1
  ref = Au_element
FEATURE [App::DocumentObjectGroupPython] G4_Au  # scripted group (container) (typed FeaturePython)
  Dunit = g/cm3
  Dvalue = 19.32
  Group = -> [Au_element001]
  conduct = 2
  density = 1
  expand = 3
  formula = Au
  name = G4_Au
  specific = 4
FEATURE [App::DocumentObjectGroupPython] Hg_element002  label="Hg_element : 002"  # scripted group (container) (typed FeaturePython)
  n = 1
  ref = Hg_element
FEATURE [App::DocumentObjectGroupPython] G4_Hg  # scripted group (container) (typed FeaturePython)
  Dunit = g/cm3
  Dvalue = 13.546
  Group = -> [Hg_element002]
  conduct = 2
  density = 1
  expand = 3
  formula = Hg
  name = G4_Hg
  specific = 4
FEATURE [App::DocumentObjectGroupPython] Tl_element002  label="Tl_element : 002"  # scripted group (container) (typed FeaturePython)
  n = 1
  ref = Tl_element
FEATURE [App::DocumentObjectGroupPython] G4_Tl  # scripted group (container) (typed FeaturePython)
  Dunit = g/cm3
  Dvalue = 11.72
  Group = -> [Tl_element002]
  conduct = 2
  density = 1
  expand = 3
  formula = Tl
  name = G4_Tl
  specific = 4
FEATURE [App::DocumentObjectGroupPython] Pb_element003  label="Pb_element : 1"  # scripted group (container) (typed FeaturePython)
  n = 1
  ref = Pb_element
FEATURE [App::DocumentObjectGroupPython] G4_Pb  # scripted group (container) (typed FeaturePython)
  Dunit = g/cm3
  Dvalue = 11.35
  Group = -> [Pb_element003]
  conduct = 2
  density = 1
  expand = 3
  formula = Pb
  name = G4_Pb
  specific = 4
FEATURE [App::DocumentObjectGroupPython] Bi_element002  label="Bi_element : 1"  # scripted group (container) (typed FeaturePython)
  n = 1
  ref = Bi_element
FEATURE [App::DocumentObjectGroupPython] G4_Bi  # scripted group (container) (typed FeaturePython)
  Dunit = g/cm3
  Dvalue = 9.747
  Group = -> [Bi_element002]
  conduct = 2
  density = 1
  expand = 3
  formula = Bi
  name = G4_Bi
  specific = 4
FEATURE [App::DocumentObjectGroupPython] Po_element001  label="Po_element : 1"  # scripted group (container) (typed FeaturePython)
  n = 1
  ref = Po_element
FEATURE [App::DocumentObjectGroupPython] G4_Po  # scripted group (container) (typed FeaturePython)
  Dunit = g/cm3
  Dvalue = 9.32
  Group = -> [Po_element001]
  conduct = 2
  density = 1
  expand = 3
  formula = Po
  name = G4_Po
  specific = 4
FEATURE [App::DocumentObjectGroupPython] At_element001  label="At_element : 1"  # scripted group (container) (typed FeaturePython)
  n = 1
  ref = At_element
FEATURE [App::DocumentObjectGroupPython] G4_At  # scripted group (container) (typed FeaturePython)
  Dunit = g/cm3
  Dvalue = 9.32
  Group = -> [At_element001]
  conduct = 2
  density = 1
  expand = 3
  formula = At
  name = G4_At
  specific = 4
FEATURE [App::DocumentObjectGroupPython] Rn_element001  label="Rn_element : 1"  # scripted group (container) (typed FeaturePython)
  n = 1
  ref = Rn_element
FEATURE [App::DocumentObjectGroupPython] G4_Rn  # scripted group (container) (typed FeaturePython)
  Dunit = g/cm3
  Dvalue = 0.00900662
  Group = -> [Rn_element001]
  conduct = 2
  density = 1
  expand = 3
  formula = Rn
  name = G4_Rn
  specific = 4
FEATURE [App::DocumentObjectGroupPython] Fr_element001  label="Fr_element : 1"  # scripted group (container) (typed FeaturePython)
  n = 1
  ref = Fr_element
FEATURE [App::DocumentObjectGroupPython] G4_Fr  # scripted group (container) (typed FeaturePython)
  Dunit = g/cm3
  Dvalue = 1
  Group = -> [Fr_element001]
  conduct = 2
  density = 1
  expand = 3
  formula = Fr
  name = G4_Fr
  specific = 4
FEATURE [App::DocumentObjectGroupPython] Ra_element001  label="Ra_element : 1"  # scripted group (container) (typed FeaturePython)
  n = 1
  ref = Ra_element
FEATURE [App::DocumentObjectGroupPython] G4_Ra  # scripted group (container) (typed FeaturePython)
  Dunit = g/cm3
  Dvalue = 5
  Group = -> [Ra_element001]
  conduct = 2
  density = 1
  expand = 3
  formula = Ra
  name = G4_Ra
  specific = 4
FEATURE [App::DocumentObjectGroupPython] Ac_element001  label="Ac_element : 1"  # scripted group (container) (typed FeaturePython)
  n = 1
  ref = Ac_element
FEATURE [App::DocumentObjectGroupPython] G4_Ac  # scripted group (container) (typed FeaturePython)
  Dunit = g/cm3
  Dvalue = 10.07
  Group = -> [Ac_element001]
  conduct = 2
  density = 1
  expand = 3
  formula = Ac
  name = G4_Ac
  specific = 4
FEATURE [App::DocumentObjectGroupPython] Th_element001  label="Th_element : 1"  # scripted group (container) (typed FeaturePython)
  n = 1
  ref = Th_element
FEATURE [App::DocumentObjectGroupPython] G4_Th  # scripted group (container) (typed FeaturePython)
  Dunit = g/cm3
  Dvalue = 11.72
  Group = -> [Th_element001]
  conduct = 2
  density = 1
  expand = 3
  formula = Th
  name = G4_Th
  specific = 4
FEATURE [App::DocumentObjectGroupPython] Pa_element001  label="Pa_element : 1"  # scripted group (container) (typed FeaturePython)
  n = 1
  ref = Pa_element
FEATURE [App::DocumentObjectGroupPython] G4_Pa  # scripted group (container) (typed FeaturePython)
  Dunit = g/cm3
  Dvalue = 15.37
  Group = -> [Pa_element001]
  conduct = 2
  density = 1
  expand = 3
  formula = Pa
  name = G4_Pa
  specific = 4
FEATURE [App::DocumentObjectGroupPython] U_element004  label="U_element : 004"  # scripted group (container) (typed FeaturePython)
  n = 1
  ref = U_element
FEATURE [App::DocumentObjectGroupPython] G4_U  # scripted group (container) (typed FeaturePython)
  Dunit = g/cm3
  Dvalue = 18.95
  Group = -> [U_element004]
  conduct = 2
  density = 1
  expand = 3
  formula = U
  name = G4_U
  specific = 4
FEATURE [App::DocumentObjectGroupPython] Np_element001  label="Np_element : 1"  # scripted group (container) (typed FeaturePython)
  n = 1
  ref = Np_element
FEATURE [App::DocumentObjectGroupPython] G4_Np  # scripted group (container) (typed FeaturePython)
  Dunit = g/cm3
  Dvalue = 20.25
  Group = -> [Np_element001]
  conduct = 2
  density = 1
  expand = 3
  formula = Np
  name = G4_Np
  specific = 4
FEATURE [App::DocumentObjectGroupPython] Pu_element002  label="Pu_element : 002"  # scripted group (container) (typed FeaturePython)
  n = 1
  ref = Pu_element
FEATURE [App::DocumentObjectGroupPython] G4_Pu  # scripted group (container) (typed FeaturePython)
  Dunit = g/cm3
  Dvalue = 19.84
  Group = -> [Pu_element002]
  conduct = 2
  density = 1
  expand = 3
  formula = Pu
  name = G4_Pu
  specific = 4
FEATURE [App::DocumentObjectGroupPython] Am_element001  label="Am_element : 1"  # scripted group (container) (typed FeaturePython)
  n = 1
  ref = Am_element
FEATURE [App::DocumentObjectGroupPython] G4_Am  # scripted group (container) (typed FeaturePython)
  Dunit = g/cm3
  Dvalue = 13.67
  Group = -> [Am_element001]
  conduct = 2
  density = 1
  expand = 3
  formula = Am
  name = G4_Am
  specific = 4
FEATURE [App::DocumentObjectGroupPython] Cm_element001  label="Cm_element : 1"  # scripted group (container) (typed FeaturePython)
  n = 1
  ref = Cm_element
FEATURE [App::DocumentObjectGroupPython] G4_Cm  # scripted group (container) (typed FeaturePython)
  Dunit = g/cm3
  Dvalue = 13.51
  Group = -> [Cm_element001]
  conduct = 2
  density = 1
  expand = 3
  formula = Cm
  name = G4_Cm
  specific = 4
FEATURE [App::DocumentObjectGroupPython] Bk_element001  label="Bk_element : 1"  # scripted group (container) (typed FeaturePython)
  n = 1
  ref = Bk_element
FEATURE [App::DocumentObjectGroupPython] G4_Bk  # scripted group (container) (typed FeaturePython)
  Dunit = g/cm3
  Dvalue = 14
  Group = -> [Bk_element001]
  conduct = 2
  density = 1
  expand = 3
  formula = Bk
  name = G4_Bk
  specific = 4
FEATURE [App::DocumentObjectGroupPython] Cf_element001  label="Cf_element : 1"  # scripted group (container) (typed FeaturePython)
  n = 1
  ref = Cf_element
FEATURE [App::DocumentObjectGroupPython] G4_Cf  # scripted group (container) (typed FeaturePython)
  Dunit = g/cm3
  Dvalue = 10
  Group = -> [Cf_element001]
  conduct = 2
  density = 1
  expand = 3
  formula = Cf
  name = G4_Cf
  specific = 4
FEATURE [App::DocumentObjectGroupPython] Element  # scripted group (container) (typed FeaturePython)
  Group = -> [G4_H,G4_He,G4_Li,G4_Be,G4_B,G4_C,G4_N,G4_O,G4_F,G4_Ne,G4_Na,G4_Mg,G4_Al,G4_Si,G4_P,G4_S,G4_Cl,G4_Ar,G4_K,G4_Ca,G4_Sc,G4_Ti,G4_V,G4_Cr,G4_Mn,G4_Fe,G4_Co,G4_Ni,G4_Cu,G4_Zn,G4_Ga,G4_Ge,G4_As,G4_Se,G4_Br,G4_Kr,G4_Rb,G4_Sr,G4_Y,G4_Zr,G4_Nb,G4_Mo,G4_Tc,G4_Ru,G4_Rh,G4_Pd,G4_Ag,G4_Cd,G4_In,G4_Sn,G4_Sb,G4_Te,G4_I,G4_Xe,G4_Cs,G4_Ba,G4_La,G4_Ce,G4_Pr,G4_Nd,G4_Pm,G4_Sm,G4_Eu,G4_Gd,G4_Tb,G4_Dy,G4_Ho,G4_Er,+30 more]
FEATURE [App::DocumentObjectGroupPython] H_element114  label="H_element : 063"  # scripted group (container) (typed FeaturePython)
  n = 2
  ref = H_element
FEATURE [App::DocumentObjectGroupPython] G4_lH2  # scripted group (container) (typed FeaturePython)
  Dunit = g/cm3
  Dvalue = 0.0708
  Group = -> [H_element114]
  conduct = 2
  density = 1
  expand = 3
  formula = G4_lH2
  name = G4_lH2
  specific = 4
FEATURE [App::DocumentObjectGroupPython] N_element049  label="N_element : 022"  # scripted group (container) (typed FeaturePython)
  n = 2
  ref = N_element
FEATURE [App::DocumentObjectGroupPython] G4_lN2  # scripted group (container) (typed FeaturePython)
  Dunit = g/cm3
  Dvalue = 0.807
  Group = -> [N_element049]
  conduct = 2
  density = 1
  expand = 3
  formula = G4_lN2
  name = G4_lN2
  specific = 4
FEATURE [App::DocumentObjectGroupPython] O_element106  label="O_element : 060"  # scripted group (container) (typed FeaturePython)
  n = 2
  ref = O_element
FEATURE [App::DocumentObjectGroupPython] G4_lO2  # scripted group (container) (typed FeaturePython)
  Dunit = g/cm3
  Dvalue = 1.141
  Group = -> [O_element106]
  conduct = 2
  density = 1
  expand = 3
  formula = G4_lO2
  name = G4_lO2
  specific = 4
FEATURE [App::DocumentObjectGroupPython] Ar  label="Ar : 1"  # scripted group (container) (typed FeaturePython)
  n = 1
  ref = Ar
FEATURE [App::DocumentObjectGroupPython] G4_lAr  # scripted group (container) (typed FeaturePython)
  Dunit = g/cm3
  Dvalue = 1.396
  Group = -> [Ar]
  conduct = 2
  density = 1
  expand = 3
  formula = G4_lAr
  name = G4_lAr
  specific = 4
FEATURE [App::DocumentObjectGroupPython] Br  label="Br : 1"  # scripted group (container) (typed FeaturePython)
  n = 1
  ref = Br
FEATURE [App::DocumentObjectGroupPython] G4_lBr  # scripted group (container) (typed FeaturePython)
  Dunit = g/cm3
  Dvalue = 3.1028
  Group = -> [Br]
  conduct = 2
  density = 1
  expand = 3
  formula = G4_lBr
  name = G4_lBr
  specific = 4
FEATURE [App::DocumentObjectGroupPython] Kr  label="Kr : 1"  # scripted group (container) (typed FeaturePython)
  n = 1
  ref = Kr
FEATURE [App::DocumentObjectGroupPython] G4_lKr  # scripted group (container) (typed FeaturePython)
  Dunit = g/cm3
  Dvalue = 2.418
  Group = -> [Kr]
  conduct = 2
  density = 1
  expand = 3
  formula = G4_lKr
  name = G4_lKr
  specific = 4
FEATURE [App::DocumentObjectGroupPython] Xe  label="Xe : 1"  # scripted group (container) (typed FeaturePython)
  n = 1
  ref = Xe
FEATURE [App::DocumentObjectGroupPython] G4_lXe  # scripted group (container) (typed FeaturePython)
  Dunit = g/cm3
  Dvalue = 2.953
  Group = -> [Xe]
  conduct = 2
  density = 1
  expand = 3
  formula = G4_lXe
  name = G4_lXe
  specific = 4
FEATURE [App::DocumentObjectGroupPython] O_element107  label="O_element : 061"  # scripted group (container) (typed FeaturePython)
  n = 4
  ref = O_element
FEATURE [App::DocumentObjectGroupPython] Pb_element004  label="Pb_element : 002"  # scripted group (container) (typed FeaturePython)
  n = 1
  ref = Pb_element
FEATURE [App::DocumentObjectGroupPython] W_element005  label="W_element : 005"  # scripted group (container) (typed FeaturePython)
  n = 1
  ref = W_element
FEATURE [App::DocumentObjectGroupPython] G4_PbWO4  # scripted group (container) (typed FeaturePython)
  Dunit = g/cm3
  Dvalue = 8.28
  Group = -> [O_element107,Pb_element004,W_element005]
  conduct = 2
  density = 1
  expand = 3
  formula = G4_PbWO4
  name = G4_PbWO4
  specific = 4
FEATURE [App::DocumentObjectGroupPython] alactic  label="alactic : 1"  # scripted group (container) (typed FeaturePython)
  n = 1
  ref = alactic
FEATURE [App::DocumentObjectGroupPython] G4_Galactic  # scripted group (container) (typed FeaturePython)
  Dunit = g/cm3
  Dvalue = 0
  Group = -> [alactic]
  conduct = 2
  density = 1
  expand = 3
  formula = G4_Galactic
  name = G4_Galactic
  specific = 4
FEATURE [App::DocumentObjectGroupPython] RAPHITE_POROUS  label="RAPHITE_POROUS : 1"  # scripted group (container) (typed FeaturePython)
  n = 1
  ref = RAPHITE_POROUS
FEATURE [App::DocumentObjectGroupPython] G4_GRAPHITE_POROUS  # scripted group (container) (typed FeaturePython)
  Dunit = g/cm3
  Dvalue = 1.7
  Group = -> [RAPHITE_POROUS]
  conduct = 2
  density = 1
  expand = 3
  formula = G4_GRAPHITE_POROUS
  name = G4_GRAPHITE_POROUS
  specific = 4
FEATURE [App::DocumentObjectGroupPython] H_element115  label="H_element : 0.150"  # scripted group (container) (typed FeaturePython)
  n = 0.080538
FEATURE [App::DocumentObjectGroupPython] C_element125  label="C_element : 0.600"  # scripted group (container) (typed FeaturePython)
  n = 0.599848
FEATURE [App::DocumentObjectGroupPython] O_element108  label="O_element : 0.320"  # scripted group (container) (typed FeaturePython)
  n = 0.319614
FEATURE [App::DocumentObjectGroupPython] G4_LUCITE  # scripted group (container) (typed FeaturePython)
  Dunit = g/cm3
  Dvalue = 1.19
  Group = -> [H_element115,C_element125,O_element108]
  conduct = 2
  density = 1
  expand = 3
  formula = G4_LUCITE
  name = G4_LUCITE
  specific = 4
FEATURE [App::DocumentObjectGroupPython] Cu_element002  label="Cu_element : 62"  # scripted group (container) (typed FeaturePython)
  n = 62
  ref = Cu_element
FEATURE [App::DocumentObjectGroupPython] Zn_element002  label="Zn_element : 35"  # scripted group (container) (typed FeaturePython)
  n = 35
  ref = Zn_element
FEATURE [App::DocumentObjectGroupPython] Pb_element005  label="Pb_element : 3"  # scripted group (container) (typed FeaturePython)
  n = 3
  ref = Pb_element
FEATURE [App::DocumentObjectGroupPython] G4_BRASS  # scripted group (container) (typed FeaturePython)
  Dunit = g/cm3
  Dvalue = 8.52
  Group = -> [Cu_element002,Zn_element002,Pb_element005]
  conduct = 2
  density = 1
  expand = 3
  formula = G4_BRASS
  name = G4_BRASS
  specific = 4
FEATURE [App::DocumentObjectGroupPython] Cu_element003  label="Cu_element : 89"  # scripted group (container) (typed FeaturePython)
  n = 89
  ref = Cu_element
FEATURE [App::DocumentObjectGroupPython] Zn_element003  label="Zn_element : 9"  # scripted group (container) (typed FeaturePython)
  n = 9
  ref = Zn_element
FEATURE [App::DocumentObjectGroupPython] Pb_element006  label="Pb_element : 2"  # scripted group (container) (typed FeaturePython)
  n = 2
  ref = Pb_element
FEATURE [App::DocumentObjectGroupPython] G4_BRONZE  # scripted group (container) (typed FeaturePython)
  Dunit = g/cm3
  Dvalue = 8.82
  Group = -> [Cu_element003,Zn_element003,Pb_element006]
  conduct = 2
  density = 1
  expand = 3
  formula = G4_BRONZE
  name = G4_BRONZE
  specific = 4
FEATURE [App::DocumentObjectGroupPython] Fe_element008  label="Fe_element : 74"  # scripted group (container) (typed FeaturePython)
  n = 74
  ref = Fe_element
FEATURE [App::DocumentObjectGroupPython] Cr_element002  label="Cr_element : 18"  # scripted group (container) (typed FeaturePython)
  n = 18
  ref = Cr_element
FEATURE [App::DocumentObjectGroupPython] Ni_element002  label="Ni_element : 8"  # scripted group (container) (typed FeaturePython)
  n = 8
  ref = Ni_element
FEATURE [App::DocumentObjectGroupPython] G4_STAINLESS_STEEL  label="G4_STAINLESS-STEEL"  # scripted group (container) (typed FeaturePython)
  Dunit = g/cm3
  Dvalue = 8
  Group = -> [Fe_element008,Cr_element002,Ni_element002]
  conduct = 2
  density = 1
  expand = 3
  formula = G4_STAINLESS-STEEL
  name = G4_STAINLESS-STEEL
  specific = 4
FEATURE [App::DocumentObjectGroupPython] H_element116  label="H_element : 064"  # scripted group (container) (typed FeaturePython)
  n = 18
  ref = H_element
FEATURE [App::DocumentObjectGroupPython] C_element126  label="C_element : 071"  # scripted group (container) (typed FeaturePython)
  n = 12
  ref = C_element
FEATURE [App::DocumentObjectGroupPython] O_element109  label="O_element : 062"  # scripted group (container) (typed FeaturePython)
  n = 7
  ref = O_element
FEATURE [App::DocumentObjectGroupPython] G4_CR39  # scripted group (container) (typed FeaturePython)
  Dunit = g/cm3
  Dvalue = 1.32
  Group = -> [H_element116,C_element126,O_element109]
  conduct = 2
  density = 1
  expand = 3
  formula = G4_CR39
  name = G4_CR39
  specific = 4
FEATURE [App::DocumentObjectGroupPython] H_element117  label="H_element : 38"  # scripted group (container) (typed FeaturePython)
  n = 38
  ref = H_element
FEATURE [App::DocumentObjectGroupPython] C_element127  label="C_element : 072"  # scripted group (container) (typed FeaturePython)
  n = 18
  ref = C_element
FEATURE [App::DocumentObjectGroupPython] O_element110  label="O_element : 063"  # scripted group (container) (typed FeaturePython)
  n = 1
  ref = O_element
FEATURE [App::DocumentObjectGroupPython] G4_OCTADECANOL  # scripted group (container) (typed FeaturePython)
  Dunit = g/cm3
  Dvalue = 0.812
  Group = -> [H_element117,C_element127,O_element110]
  conduct = 2
  density = 1
  expand = 3
  formula = G4_OCTADECANOL
  name = G4_OCTADECANOL
  specific = 4
FEATURE [App::DocumentObjectGroupPython] HEP  # scripted group (container) (typed FeaturePython)
  Group = -> [G4_lH2,G4_lN2,G4_lO2,G4_lAr,G4_lBr,G4_lKr,G4_lXe,G4_PbWO4,G4_Galactic,G4_GRAPHITE_POROUS,G4_LUCITE,G4_BRASS,G4_BRONZE,G4_STAINLESS_STEEL,G4_CR39,G4_OCTADECANOL]
FEATURE [App::DocumentObjectGroupPython] C_element128  label="C_element : 073"  # scripted group (container) (typed FeaturePython)
  n = 14
  ref = C_element
FEATURE [App::DocumentObjectGroupPython] H_element118  label="H_element : 065"  # scripted group (container) (typed FeaturePython)
  n = 10
  ref = H_element
FEATURE [App::DocumentObjectGroupPython] O_element111  label="O_element : 064"  # scripted group (container) (typed FeaturePython)
  n = 2
  ref = O_element
FEATURE [App::DocumentObjectGroupPython] N_element050  label="N_element : 023"  # scripted group (container) (typed FeaturePython)
  n = 2
  ref = N_element
FEATURE [App::DocumentObjectGroupPython] G4_KEVLAR  # scripted group (container) (typed FeaturePython)
  Dunit = g/cm3
  Dvalue = 1.44
  Group = -> [C_element128,H_element118,O_element111,N_element050]
  conduct = 2
  density = 1
  expand = 3
  formula = G4_KEVLAR
  name = G4_KEVLAR
  specific = 4
FEATURE [App::DocumentObjectGroupPython] C_element129  label="C_element : 074"  # scripted group (container) (typed FeaturePython)
  n = 10
  ref = C_element
FEATURE [App::DocumentObjectGroupPython] H_element119  label="H_element : 066"  # scripted group (container) (typed FeaturePython)
  n = 8
  ref = H_element
FEATURE [App::DocumentObjectGroupPython] O_element112  label="O_element : 065"  # scripted group (container) (typed FeaturePython)
  n = 4
  ref = O_element
FEATURE [App::DocumentObjectGroupPython] G4_DACRON  # scripted group (container) (typed FeaturePython)
  Dunit = g/cm3
  Dvalue = 1.4
  Group = -> [C_element129,H_element119,O_element112]
  conduct = 2
  density = 1
  expand = 3
  formula = G4_DACRON
  name = G4_DACRON
  specific = 4
FEATURE [App::DocumentObjectGroupPython] C_element130  label="C_element : 075"  # scripted group (container) (typed FeaturePython)
  n = 4
  ref = C_element
FEATURE [App::DocumentObjectGroupPython] H_element120  label="H_element : 067"  # scripted group (container) (typed FeaturePython)
  n = 5
  ref = H_element
FEATURE [App::DocumentObjectGroupPython] Cl_element030  label="Cl_element : 016"  # scripted group (container) (typed FeaturePython)
  n = 1
  ref = Cl_element
FEATURE [App::DocumentObjectGroupPython] G4_NEOPRENE  # scripted group (container) (typed FeaturePython)
  Dunit = g/cm3
  Dvalue = 1.23
  Group = -> [C_element130,H_element120,Cl_element030]
  conduct = 2
  density = 1
  expand = 3
  formula = G4_NEOPRENE
  name = G4_NEOPRENE
  specific = 4
FEATURE [App::DocumentObjectGroupPython] Space  # scripted group (container) (typed FeaturePython)
  Group = -> [G4_KEVLAR,G4_DACRON,G4_NEOPRENE]
FEATURE [App::DocumentObjectGroupPython] H_element121  label="H_element : 068"  # scripted group (container) (typed FeaturePython)
  n = 5
  ref = H_element
FEATURE [App::DocumentObjectGroupPython] C_element131  label="C_element : 076"  # scripted group (container) (typed FeaturePython)
  n = 4
  ref = C_element
FEATURE [App::DocumentObjectGroupPython] N_element051  label="N_element : 3"  # scripted group (container) (typed FeaturePython)
  n = 3
  ref = N_element
FEATURE [App::DocumentObjectGroupPython] O_element113  label="O_element : 066"  # scripted group (container) (typed FeaturePython)
  n = 1
  ref = O_element
FEATURE [App::DocumentObjectGroupPython] G4_CYTOSINE  # scripted group (container) (typed FeaturePython)
  Dunit = g/cm3
  Dvalue = 1.55
  Group = -> [H_element121,C_element131,N_element051,O_element113]
  conduct = 2
  density = 1
  expand = 3
  formula = G4_CYTOSINE
  name = G4_CYTOSINE
  specific = 4
FEATURE [App::DocumentObjectGroupPython] H_element122  label="H_element : 069"  # scripted group (container) (typed FeaturePython)
  n = 6
  ref = H_element
FEATURE [App::DocumentObjectGroupPython] C_element132  label="C_element : 077"  # scripted group (container) (typed FeaturePython)
  n = 5
  ref = C_element
FEATURE [App::DocumentObjectGroupPython] N_element052  label="N_element : 024"  # scripted group (container) (typed FeaturePython)
  n = 2
  ref = N_element
FEATURE [App::DocumentObjectGroupPython] O_element114  label="O_element : 067"  # scripted group (container) (typed FeaturePython)
  n = 2
  ref = O_element
FEATURE [App::DocumentObjectGroupPython] G4_THYMINE  # scripted group (container) (typed FeaturePython)
  Dunit = g/cm3
  Dvalue = 1.23
  Group = -> [H_element122,C_element132,N_element052,O_element114]
  conduct = 2
  density = 1
  expand = 3
  formula = G4_THYMINE
  name = G4_THYMINE
  specific = 4
FEATURE [App::DocumentObjectGroupPython] H_element123  label="H_element : 070"  # scripted group (container) (typed FeaturePython)
  n = 4
  ref = H_element
FEATURE [App::DocumentObjectGroupPython] C_element133  label="C_element : 078"  # scripted group (container) (typed FeaturePython)
  n = 4
  ref = C_element
FEATURE [App::DocumentObjectGroupPython] N_element053  label="N_element : 025"  # scripted group (container) (typed FeaturePython)
  n = 2
  ref = N_element
FEATURE [App::DocumentObjectGroupPython] O_element115  label="O_element : 068"  # scripted group (container) (typed FeaturePython)
  n = 2
  ref = O_element
FEATURE [App::DocumentObjectGroupPython] G4_URACIL  # scripted group (container) (typed FeaturePython)
  Dunit = g/cm3
  Dvalue = 1.32
  Group = -> [H_element123,C_element133,N_element053,O_element115]
  conduct = 2
  density = 1
  expand = 3
  formula = G4_URACIL
  name = G4_URACIL
  specific = 4
FEATURE [App::DocumentObjectGroupPython] H_element124  label="H_element : 071"  # scripted group (container) (typed FeaturePython)
  n = 4
  ref = H_element
FEATURE [App::DocumentObjectGroupPython] C_element134  label="C_element : 079"  # scripted group (container) (typed FeaturePython)
  n = 5
  ref = C_element
FEATURE [App::DocumentObjectGroupPython] N_element054  label="N_element : 026"  # scripted group (container) (typed FeaturePython)
  n = 5
  ref = N_element
FEATURE [App::DocumentObjectGroupPython] G4_DNA_ADENINE  # scripted group (container) (typed FeaturePython)
  Dunit = g/cm3
  Dvalue = 1
  Group = -> [H_element124,C_element134,N_element054]
  conduct = 2
  density = 1
  expand = 3
  formula = G4_DNA_ADENINE
  name = G4_DNA_ADENINE
  specific = 4
FEATURE [App::DocumentObjectGroupPython] H_element125  label="H_element : 072"  # scripted group (container) (typed FeaturePython)
  n = 4
  ref = H_element
FEATURE [App::DocumentObjectGroupPython] C_element135  label="C_element : 080"  # scripted group (container) (typed FeaturePython)
  n = 5
  ref = C_element
FEATURE [App::DocumentObjectGroupPython] N_element055  label="N_element : 027"  # scripted group (container) (typed FeaturePython)
  n = 5
  ref = N_element
FEATURE [App::DocumentObjectGroupPython] O_element116  label="O_element : 069"  # scripted group (container) (typed FeaturePython)
  n = 1
  ref = O_element
FEATURE [App::DocumentObjectGroupPython] G4_DNA_GUANINE  # scripted group (container) (typed FeaturePython)
  Dunit = g/cm3
  Dvalue = 1
  Group = -> [H_element125,C_element135,N_element055,O_element116]
  conduct = 2
  density = 1
  expand = 3
  formula = G4_DNA_GUANINE
  name = G4_DNA_GUANINE
  specific = 4
FEATURE [App::DocumentObjectGroupPython] H_element126  label="H_element : 073"  # scripted group (container) (typed FeaturePython)
  n = 4
  ref = H_element
FEATURE [App::DocumentObjectGroupPython] C_element136  label="C_element : 081"  # scripted group (container) (typed FeaturePython)
  n = 4
  ref = C_element
FEATURE [App::DocumentObjectGroupPython] N_element056  label="N_element : 028"  # scripted group (container) (typed FeaturePython)
  n = 3
  ref = N_element
FEATURE [App::DocumentObjectGroupPython] O_element117  label="O_element : 070"  # scripted group (container) (typed FeaturePython)
  n = 1
  ref = O_element
FEATURE [App::DocumentObjectGroupPython] G4_DNA_CYTOSINE  # scripted group (container) (typed FeaturePython)
  Dunit = g/cm3
  Dvalue = 1
  Group = -> [H_element126,C_element136,N_element056,O_element117]
  conduct = 2
  density = 1
  expand = 3
  formula = G4_DNA_CYTOSINE
  name = G4_DNA_CYTOSINE
  specific = 4
FEATURE [App::DocumentObjectGroupPython] H_element127  label="H_element : 074"  # scripted group (container) (typed FeaturePython)
  n = 5
  ref = H_element
FEATURE [App::DocumentObjectGroupPython] C_element137  label="C_element : 082"  # scripted group (container) (typed FeaturePython)
  n = 5
  ref = C_element
FEATURE [App::DocumentObjectGroupPython] N_element057  label="N_element : 029"  # scripted group (container) (typed FeaturePython)
  n = 2
  ref = N_element
FEATURE [App::DocumentObjectGroupPython] O_element118  label="O_element : 071"  # scripted group (container) (typed FeaturePython)
  n = 2
  ref = O_element
FEATURE [App::DocumentObjectGroupPython] G4_DNA_THYMINE  # scripted group (container) (typed FeaturePython)
  Dunit = g/cm3
  Dvalue = 1
  Group = -> [H_element127,C_element137,N_element057,O_element118]
  conduct = 2
  density = 1
  expand = 3
  formula = G4_DNA_THYMINE
  name = G4_DNA_THYMINE
  specific = 4
FEATURE [App::DocumentObjectGroupPython] H_element128  label="H_element : 075"  # scripted group (container) (typed FeaturePython)
  n = 3
  ref = H_element
FEATURE [App::DocumentObjectGroupPython] C_element138  label="C_element : 083"  # scripted group (container) (typed FeaturePython)
  n = 4
  ref = C_element
FEATURE [App::DocumentObjectGroupPython] N_element058  label="N_element : 030"  # scripted group (container) (typed FeaturePython)
  n = 2
  ref = N_element
FEATURE [App::DocumentObjectGroupPython] O_element119  label="O_element : 072"  # scripted group (container) (typed FeaturePython)
  n = 2
  ref = O_element
FEATURE [App::DocumentObjectGroupPython] G4_DNA_URACIL  # scripted group (container) (typed FeaturePython)
  Dunit = g/cm3
  Dvalue = 1
  Group = -> [H_element128,C_element138,N_element058,O_element119]
  conduct = 2
  density = 1
  expand = 3
  formula = G4_DNA_URACIL
  name = G4_DNA_URACIL
  specific = 4
FEATURE [App::DocumentObjectGroupPython] H_element129  label="H_element : 076"  # scripted group (container) (typed FeaturePython)
  n = 10
  ref = H_element
FEATURE [App::DocumentObjectGroupPython] C_element139  label="C_element : 084"  # scripted group (container) (typed FeaturePython)
  n = 10
  ref = C_element
FEATURE [App::DocumentObjectGroupPython] N_element059  label="N_element : 031"  # scripted group (container) (typed FeaturePython)
  n = 5
  ref = N_element
FEATURE [App::DocumentObjectGroupPython] O_element120  label="O_element : 073"  # scripted group (container) (typed FeaturePython)
  n = 4
  ref = O_element
FEATURE [App::DocumentObjectGroupPython] G4_DNA_ADENOSINE  # scripted group (container) (typed FeaturePython)
  Dunit = g/cm3
  Dvalue = 1
  Group = -> [H_element129,C_element139,N_element059,O_element120]
  conduct = 2
  density = 1
  expand = 3
  formula = G4_DNA_ADENOSINE
  name = G4_DNA_ADENOSINE
  specific = 4
FEATURE [App::DocumentObjectGroupPython] H_element130  label="H_element : 077"  # scripted group (container) (typed FeaturePython)
  n = 10
  ref = H_element
FEATURE [App::DocumentObjectGroupPython] C_element140  label="C_element : 085"  # scripted group (container) (typed FeaturePython)
  n = 10
  ref = C_element
FEATURE [App::DocumentObjectGroupPython] N_element060  label="N_element : 032"  # scripted group (container) (typed FeaturePython)
  n = 5
  ref = N_element
FEATURE [App::DocumentObjectGroupPython] O_element121  label="O_element : 074"  # scripted group (container) (typed FeaturePython)
  n = 5
  ref = O_element
FEATURE [App::DocumentObjectGroupPython] G4_DNA_GUANOSINE  # scripted group (container) (typed FeaturePython)
  Dunit = g/cm3
  Dvalue = 1
  Group = -> [H_element130,C_element140,N_element060,O_element121]
  conduct = 2
  density = 1
  expand = 3
  formula = G4_DNA_GUANOSINE
  name = G4_DNA_GUANOSINE
  specific = 4
FEATURE [App::DocumentObjectGroupPython] H_element131  label="H_element : 078"  # scripted group (container) (typed FeaturePython)
  n = 10
  ref = H_element
FEATURE [App::DocumentObjectGroupPython] C_element141  label="C_element : 086"  # scripted group (container) (typed FeaturePython)
  n = 9
  ref = C_element
FEATURE [App::DocumentObjectGroupPython] N_element061  label="N_element : 033"  # scripted group (container) (typed FeaturePython)
  n = 3
  ref = N_element
FEATURE [App::DocumentObjectGroupPython] O_element122  label="O_element : 075"  # scripted group (container) (typed FeaturePython)
  n = 5
  ref = O_element
FEATURE [App::DocumentObjectGroupPython] G4_DNA_CYTIDINE  # scripted group (container) (typed FeaturePython)
  Dunit = g/cm3
  Dvalue = 1
  Group = -> [H_element131,C_element141,N_element061,O_element122]
  conduct = 2
  density = 1
  expand = 3
  formula = G4_DNA_CYTIDINE
  name = G4_DNA_CYTIDINE
  specific = 4
FEATURE [App::DocumentObjectGroupPython] H_element132  label="H_element : 079"  # scripted group (container) (typed FeaturePython)
  n = 9
  ref = H_element
FEATURE [App::DocumentObjectGroupPython] C_element142  label="C_element : 087"  # scripted group (container) (typed FeaturePython)
  n = 9
  ref = C_element
FEATURE [App::DocumentObjectGroupPython] N_element062  label="N_element : 034"  # scripted group (container) (typed FeaturePython)
  n = 2
  ref = N_element
FEATURE [App::DocumentObjectGroupPython] O_element123  label="O_element : 076"  # scripted group (container) (typed FeaturePython)
  n = 6
  ref = O_element
FEATURE [App::DocumentObjectGroupPython] G4_DNA_URIDINE  # scripted group (container) (typed FeaturePython)
  Dunit = g/cm3
  Dvalue = 1
  Group = -> [H_element132,C_element142,N_element062,O_element123]
  conduct = 2
  density = 1
  expand = 3
  formula = G4_DNA_URIDINE
  name = G4_DNA_URIDINE
  specific = 4
FEATURE [App::DocumentObjectGroupPython] H_element133  label="H_element : 080"  # scripted group (container) (typed FeaturePython)
  n = 11
  ref = H_element
FEATURE [App::DocumentObjectGroupPython] C_element143  label="C_element : 088"  # scripted group (container) (typed FeaturePython)
  n = 10
  ref = C_element
FEATURE [App::DocumentObjectGroupPython] N_element063  label="N_element : 035"  # scripted group (container) (typed FeaturePython)
  n = 2
  ref = N_element
FEATURE [App::DocumentObjectGroupPython] O_element124  label="O_element : 077"  # scripted group (container) (typed FeaturePython)
  n = 6
  ref = O_element
FEATURE [App::DocumentObjectGroupPython] G4_DNA_METHYLURIDINE  # scripted group (container) (typed FeaturePython)
  Dunit = g/cm3
  Dvalue = 1
  Group = -> [H_element133,C_element143,N_element063,O_element124]
  conduct = 2
  density = 1
  expand = 3
  formula = G4_DNA_METHYLURIDINE
  name = G4_DNA_METHYLURIDINE
  specific = 4
FEATURE [App::DocumentObjectGroupPython] P_element014  label="P_element : 003"  # scripted group (container) (typed FeaturePython)
  n = 1
  ref = P_element
FEATURE [App::DocumentObjectGroupPython] O_element125  label="O_element : 078"  # scripted group (container) (typed FeaturePython)
  n = 3
  ref = O_element
FEATURE [App::DocumentObjectGroupPython] G4_DNA_MONOPHOSPHATE  # scripted group (container) (typed FeaturePython)
  Dunit = g/cm3
  Dvalue = 1
  Group = -> [P_element014,O_element125]
  conduct = 2
  density = 1
  expand = 3
  formula = G4_DNA_MONOPHOSPHATE
  name = G4_DNA_MONOPHOSPHATE
  specific = 4
FEATURE [App::DocumentObjectGroupPython] H_element134  label="H_element : 081"  # scripted group (container) (typed FeaturePython)
  n = 10
  ref = H_element
FEATURE [App::DocumentObjectGroupPython] C_element144  label="C_element : 089"  # scripted group (container) (typed FeaturePython)
  n = 10
  ref = C_element
FEATURE [App::DocumentObjectGroupPython] N_element064  label="N_element : 036"  # scripted group (container) (typed FeaturePython)
  n = 5
  ref = N_element
FEATURE [App::DocumentObjectGroupPython] O_element126  label="O_element : 079"  # scripted group (container) (typed FeaturePython)
  n = 7
  ref = O_element
FEATURE [App::DocumentObjectGroupPython] P_element015  label="P_element : 004"  # scripted group (container) (typed FeaturePython)
  n = 1
  ref = P_element
FEATURE [App::DocumentObjectGroupPython] G4_DNA_A  # scripted group (container) (typed FeaturePython)
  Dunit = g/cm3
  Dvalue = 1
  Group = -> [H_element134,C_element144,N_element064,O_element126,P_element015]
  conduct = 2
  density = 1
  expand = 3
  formula = G4_DNA_A
  name = G4_DNA_A
  specific = 4
FEATURE [App::DocumentObjectGroupPython] H_element135  label="H_element : 082"  # scripted group (container) (typed FeaturePython)
  n = 10
  ref = H_element
FEATURE [App::DocumentObjectGroupPython] C_element145  label="C_element : 090"  # scripted group (container) (typed FeaturePython)
  n = 10
  ref = C_element
FEATURE [App::DocumentObjectGroupPython] N_element065  label="N_element : 037"  # scripted group (container) (typed FeaturePython)
  n = 5
  ref = N_element
FEATURE [App::DocumentObjectGroupPython] O_element127  label="O_element : 8"  # scripted group (container) (typed FeaturePython)
  n = 8
  ref = O_element
FEATURE [App::DocumentObjectGroupPython] P_element016  label="P_element : 005"  # scripted group (container) (typed FeaturePython)
  n = 1
  ref = P_element
FEATURE [App::DocumentObjectGroupPython] G4_DNA_G  # scripted group (container) (typed FeaturePython)
  Dunit = g/cm3
  Dvalue = 1
  Group = -> [H_element135,C_element145,N_element065,O_element127,P_element016]
  conduct = 2
  density = 1
  expand = 3
  formula = G4_DNA_G
  name = G4_DNA_G
  specific = 4
FEATURE [App::DocumentObjectGroupPython] H_element136  label="H_element : 083"  # scripted group (container) (typed FeaturePython)
  n = 10
  ref = H_element
FEATURE [App::DocumentObjectGroupPython] C_element146  label="C_element : 091"  # scripted group (container) (typed FeaturePython)
  n = 9
  ref = C_element
FEATURE [App::DocumentObjectGroupPython] N_element066  label="N_element : 038"  # scripted group (container) (typed FeaturePython)
  n = 3
  ref = N_element
FEATURE [App::DocumentObjectGroupPython] O_element128  label="O_element : 080"  # scripted group (container) (typed FeaturePython)
  n = 8
  ref = O_element
FEATURE [App::DocumentObjectGroupPython] P_element017  label="P_element : 006"  # scripted group (container) (typed FeaturePython)
  n = 1
  ref = P_element
FEATURE [App::DocumentObjectGroupPython] G4_DNA_C  # scripted group (container) (typed FeaturePython)
  Dunit = g/cm3
  Dvalue = 1
  Group = -> [H_element136,C_element146,N_element066,O_element128,P_element017]
  conduct = 2
  density = 1
  expand = 3
  formula = G4_DNA_C
  name = G4_DNA_C
  specific = 4
FEATURE [App::DocumentObjectGroupPython] H_element137  label="H_element : 084"  # scripted group (container) (typed FeaturePython)
  n = 9
  ref = H_element
FEATURE [App::DocumentObjectGroupPython] C_element147  label="C_element : 092"  # scripted group (container) (typed FeaturePython)
  n = 9
  ref = C_element
FEATURE [App::DocumentObjectGroupPython] N_element067  label="N_element : 039"  # scripted group (container) (typed FeaturePython)
  n = 2
  ref = N_element
FEATURE [App::DocumentObjectGroupPython] O_element129  label="O_element : 9"  # scripted group (container) (typed FeaturePython)
  n = 9
  ref = O_element
FEATURE [App::DocumentObjectGroupPython] P_element018  label="P_element : 007"  # scripted group (container) (typed FeaturePython)
  n = 1
  ref = P_element
FEATURE [App::DocumentObjectGroupPython] G4_DNA_U  # scripted group (container) (typed FeaturePython)
  Dunit = g/cm3
  Dvalue = 1
  Group = -> [H_element137,C_element147,N_element067,O_element129,P_element018]
  conduct = 2
  density = 1
  expand = 3
  formula = G4_DNA_U
  name = G4_DNA_U
  specific = 4
FEATURE [App::DocumentObjectGroupPython] H_element138  label="H_element : 085"  # scripted group (container) (typed FeaturePython)
  n = 11
  ref = H_element
FEATURE [App::DocumentObjectGroupPython] C_element148  label="C_element : 093"  # scripted group (container) (typed FeaturePython)
  n = 10
  ref = C_element
FEATURE [App::DocumentObjectGroupPython] N_element068  label="N_element : 040"  # scripted group (container) (typed FeaturePython)
  n = 2
  ref = N_element
FEATURE [App::DocumentObjectGroupPython] O_element130  label="O_element : 081"  # scripted group (container) (typed FeaturePython)
  n = 9
  ref = O_element
FEATURE [App::DocumentObjectGroupPython] P_element019  label="P_element : 008"  # scripted group (container) (typed FeaturePython)
  n = 1
  ref = P_element
FEATURE [App::DocumentObjectGroupPython] G4_DNA_MU  # scripted group (container) (typed FeaturePython)
  Dunit = g/cm3
  Dvalue = 1
  Group = -> [H_element138,C_element148,N_element068,O_element130,P_element019]
  conduct = 2
  density = 1
  expand = 3
  formula = G4_DNA_MU
  name = G4_DNA_MU
  specific = 4
FEATURE [App::DocumentObjectGroupPython] BioChemical  # scripted group (container) (typed FeaturePython)
  Group = -> [G4_CYTOSINE,G4_THYMINE,G4_URACIL,G4_DNA_ADENINE,G4_DNA_GUANINE,G4_DNA_CYTOSINE,G4_DNA_THYMINE,G4_DNA_URACIL,G4_DNA_ADENOSINE,G4_DNA_GUANOSINE,G4_DNA_CYTIDINE,G4_DNA_URIDINE,G4_DNA_METHYLURIDINE,G4_DNA_MONOPHOSPHATE,G4_DNA_A,G4_DNA_G,G4_DNA_C,G4_DNA_U,G4_DNA_MU]
FEATURE [App::DocumentObjectGroupPython] G4Materials  # scripted group (container) (typed FeaturePython)
  Group = -> [NIST,Element,HEP,Space,BioChemical]
  version = 1
FEATURE [App::DocumentObjectGroupPython] Geant4  # scripted group (container) (typed FeaturePython)
  Group = -> [G4Isotopes,G4Elements,G4Materials]
FEATURE [App::DocumentObjectGroupPython] Materials  # scripted group (container) (typed FeaturePython)
  Group = -> [LYSO,Air,Glass,Geant4]
FEATURE [Part::FeaturePython] GDMLBox_World  # WARN: FeaturePython — macro-defined, semantics opaque (R4)
  lunit = 2
  material = 1
  x = 50
  y = 50
  z = 50
FEATURE [Part::FeaturePython] GDMLBox_Obj  # WARN: FeaturePython — macro-defined, semantics opaque (R4)
  lunit = 2
  material = 0
  x = 2
  y = 2
  z = 15
FEATURE [Part::FeaturePython] GDMLBox_GlassPlate  # WARN: FeaturePython — macro-defined, semantics opaque (R4)
  lunit = 2
  material = 2
  x = 2
  y = 2
  z = 2
FEATURE [App::Part] Det
  CopyNumber = 0
  Group = -> [GDMLBox_GlassPlate]
  Origin = -> Origin002
  Placement = pos=(0,0,8.5) rot=(0,0,1;0rad)
  SensDet = PhotonDetector
  SkinSurface = 0
FEATURE [App::FeaturePython] ScintWrap0  # WARN: FeaturePython — macro-defined, semantics opaque (R4)
  PV1 = Obj
  PV2 = Det
  Surface = ScintWrap
FEATURE [App::Part] Obj
  Group = -> [GDMLBox_Obj,Det,ScintWrap0]
  Origin = -> Origin001
  SensDet = Radiator
  SkinSurface = 0
FEATURE [Part::FeaturePython] Array  # Draft array (typed FeaturePython)
  AlwaysSyncPlacement = false
  Angle = 360
  ArrayType = 0
  Axis = (0,0,1)
  Base = -> Obj
  Center = (0,0,0)
  Count = 4
  ExpandArray = false
  Fuse = false
  IntervalAxis = (0,0,0)
  IntervalX = (3,0,0)
  IntervalY = (0,3,0)
  IntervalZ = (0,0,0)
  NumberCircles = 3
  NumberPolar = 5
  NumberX = 2
  NumberY = 2
  NumberZ = 1
  PlacementList = 4 placements: [(0,0,0),(0,3,0),(3,0,0),(3,3,0)]
  RadialDistance = 50
  ScaleList = (4) [(1,1,1),(1,1,1),(1,1,1),(1,1,1)]
  Symmetry = 1
  TangentialDistance = 25
  exportFlag = false
FEATURE [Part::FeaturePython] GDMLBox_Obj001  # WARN: FeaturePython — macro-defined, semantics opaque (R4)
  CopyNumber = 1
  lunit = 2
  material = 0
  x = 2
  y = 2
  z = 15
FEATURE [Part::FeaturePython] GDMLBox_GlassPlate001  # WARN: FeaturePython — macro-defined, semantics opaque (R4)
  CopyNumber = 1
  lunit = 2
  material = 2
  x = 2
  y = 2
  z = 2
FEATURE [App::Part] Det001
  CopyNumber = 1
  Group = -> [GDMLBox_GlassPlate001]
  Origin = -> Origin005
  Placement = pos=(0,0,8.5) rot=(0,0,1;0rad)
FEATURE [App::FeaturePython] ScintWrap001  # WARN: FeaturePython — macro-defined, semantics opaque (R4)
  PV1 = Obj001
  PV2 = Det001
  Surface = ScintWrap
FEATURE [App::Part] Obj001
  CopyNumber = 1
  Group = -> [GDMLBox_Obj001,Det001,ScintWrap001]
  Origin = -> Origin004
FEATURE [App::Link] Link_Obj001
  CopyNumber = 2
  LinkedObject = -> Obj001
FEATURE [App::Link] Link_Obj001001
  CopyNumber = 3
  LinkPlacement = pos=(0,3,0) rot=(0,0,1;0rad)
  LinkedObject = -> Obj001
  Placement = pos=(0,3,0) rot=(0,0,1;0rad)
FEATURE [App::Link] Link_Obj001002
  CopyNumber = 4
  LinkPlacement = pos=(3,0,0) rot=(0,0,1;0rad)
  LinkedObject = -> Obj001
  Placement = pos=(3,0,0) rot=(0,0,1;0rad)
FEATURE [App::Link] Link_Obj001003
  CopyNumber = 5
  LinkPlacement = pos=(3,3,0) rot=(0,0,1;0rad)
  LinkedObject = -> Obj001
  Placement = pos=(3,3,0) rot=(0,0,1;0rad)
FEATURE [App::Part] Array001
  Group = -> [Obj001,Link_Obj001,Link_Obj001001,Link_Obj001002,Link_Obj001003]
  Origin = -> Origin003
FEATURE [App::Part] Part
  Group = -> [Obj,Array,Array001]
  Origin = -> Origin006
FEATURE [App::Part] World
  Group = -> [GDMLBox_World,Part]
  Origin = -> Origin
